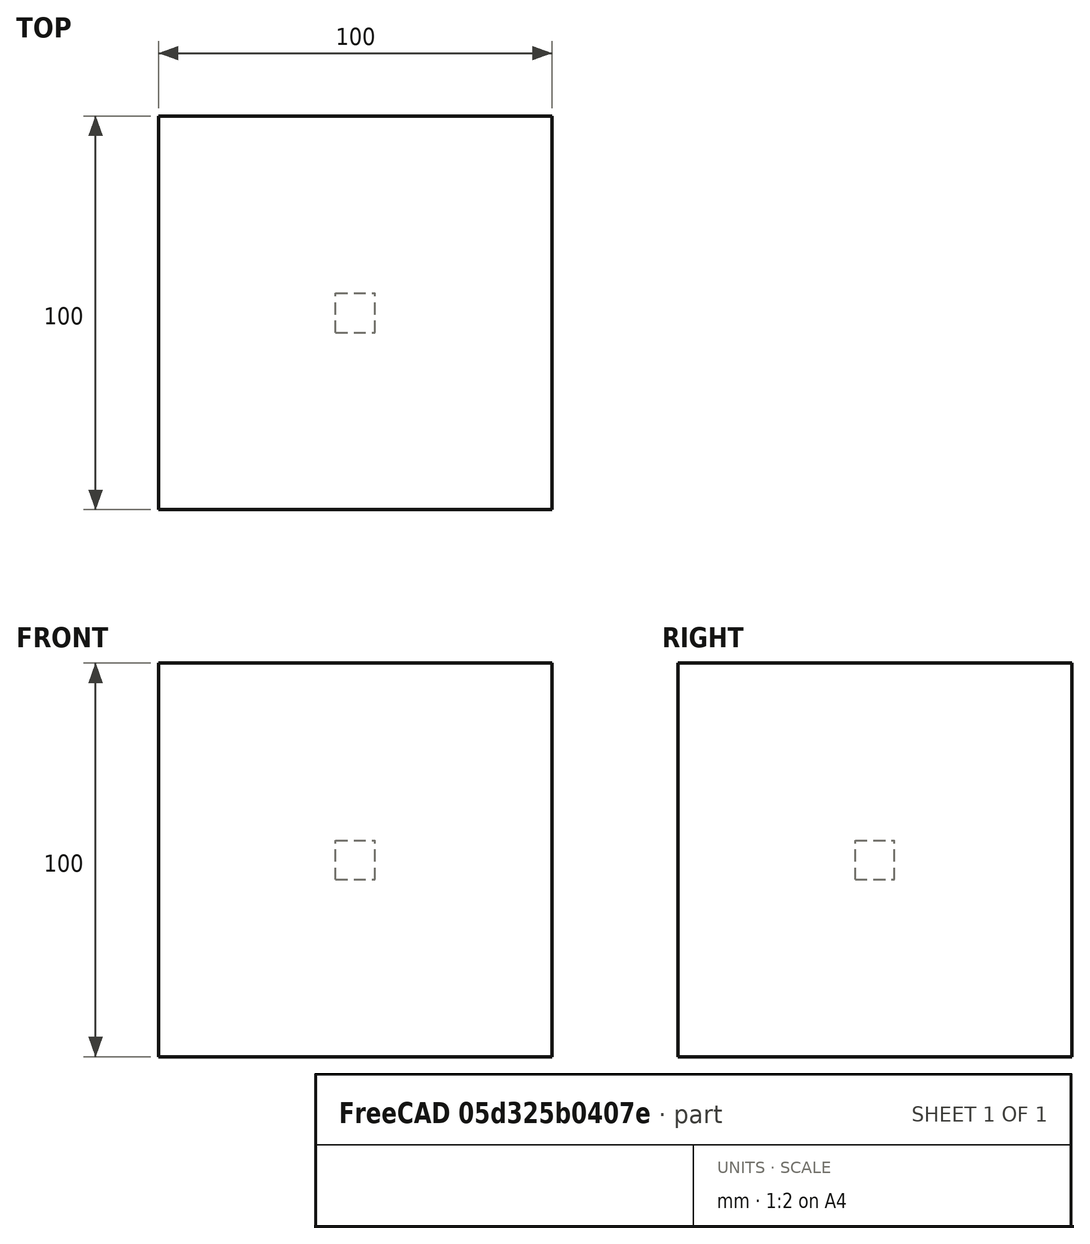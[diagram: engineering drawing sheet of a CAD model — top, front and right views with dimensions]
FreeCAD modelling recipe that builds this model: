
FCSTD DOCUMENT  (FreeCAD 0.20R29603 (Git))
Label: testCase2
License: All rights reserved
LicenseURL: http://en.wikipedia.org/wiki/All_rights_reserved
objects: App::DocumentObjectGroupPython×1251, Part::FeaturePython×3, App::Part×2
note: 2 computed .brp shape members not serialized (recipe doc carries the construction recipe); baked Part::Feature solids carry a one-line shape summary decoded from their .brp

FEATURE [App::DocumentObjectGroupPython] HALFPI  # scripted group (container) (typed FeaturePython)
  name = HALFPI
  value = pi/2.
FEATURE [App::DocumentObjectGroupPython] PI  # scripted group (container) (typed FeaturePython)
  name = PI
  value = 1.*pi
FEATURE [App::DocumentObjectGroupPython] TWOPI  # scripted group (container) (typed FeaturePython)
  name = TWOPI
  value = 2.*pi
FEATURE [App::DocumentObjectGroupPython] Constants  # scripted group (container) (typed FeaturePython)
  Group = -> [HALFPI,PI,TWOPI]
FEATURE [App::DocumentObjectGroupPython] Variables  # scripted group (container) (typed FeaturePython)
FEATURE [App::DocumentObjectGroupPython] Quantities  # scripted group (container) (typed FeaturePython)
FEATURE [App::DocumentObjectGroupPython] Isotopes  # scripted group (container) (typed FeaturePython)
FEATURE [App::DocumentObjectGroupPython] Elements  # scripted group (container) (typed FeaturePython)
FEATURE [App::DocumentObjectGroupPython] Matrix  # scripted group (container) (typed FeaturePython)
FEATURE [App::DocumentObjectGroupPython] Surfaces  # scripted group (container) (typed FeaturePython)
FEATURE [App::DocumentObjectGroupPython] Opticals  # scripted group (container) (typed FeaturePython)
  Group = -> [Matrix,Surfaces]
FEATURE [App::DocumentObjectGroupPython] G4Isotopes  # scripted group (container) (typed FeaturePython)
FEATURE [App::DocumentObjectGroupPython] H_element  # scripted group (container) (typed FeaturePython)
  Z = 1
  atom_value = 1.008
  formula = H
  name = H_element
FEATURE [App::DocumentObjectGroupPython] He_element  # scripted group (container) (typed FeaturePython)
  Z = 2
  atom_value = 4.0026
  formula = He
  name = He_element
FEATURE [App::DocumentObjectGroupPython] Li_element  # scripted group (container) (typed FeaturePython)
  Z = 3
  atom_value = 6.94
  formula = Li
  name = Li_element
FEATURE [App::DocumentObjectGroupPython] Be_element  # scripted group (container) (typed FeaturePython)
  Z = 4
  atom_value = 9.01218
  formula = Be
  name = Be_element
FEATURE [App::DocumentObjectGroupPython] B_element  # scripted group (container) (typed FeaturePython)
  Z = 5
  atom_value = 10.81
  formula = B
  name = B_element
FEATURE [App::DocumentObjectGroupPython] C_element  # scripted group (container) (typed FeaturePython)
  Z = 6
  atom_value = 12.011
  formula = C
  name = C_element
FEATURE [App::DocumentObjectGroupPython] N_element  # scripted group (container) (typed FeaturePython)
  Z = 7
  atom_value = 14.007
  formula = N
  name = N_element
FEATURE [App::DocumentObjectGroupPython] O_element  # scripted group (container) (typed FeaturePython)
  Z = 8
  atom_value = 15.999
  formula = O
  name = O_element
FEATURE [App::DocumentObjectGroupPython] F_element  # scripted group (container) (typed FeaturePython)
  Z = 9
  atom_value = 18.9984
  formula = F
  name = F_element
FEATURE [App::DocumentObjectGroupPython] Ne_element  # scripted group (container) (typed FeaturePython)
  Z = 10
  atom_value = 20.1797
  formula = Ne
  name = Ne_element
FEATURE [App::DocumentObjectGroupPython] Na_element  # scripted group (container) (typed FeaturePython)
  Z = 11
  atom_value = 22.9898
  formula = Na
  name = Na_element
FEATURE [App::DocumentObjectGroupPython] Mg_element  # scripted group (container) (typed FeaturePython)
  Z = 12
  atom_value = 24.305
  formula = Mg
  name = Mg_element
FEATURE [App::DocumentObjectGroupPython] Al_element  # scripted group (container) (typed FeaturePython)
  Z = 13
  atom_value = 26.9815
  formula = Al
  name = Al_element
FEATURE [App::DocumentObjectGroupPython] Si_element  # scripted group (container) (typed FeaturePython)
  Z = 14
  atom_value = 28.085
  formula = Si
  name = Si_element
FEATURE [App::DocumentObjectGroupPython] P_element  # scripted group (container) (typed FeaturePython)
  Z = 15
  atom_value = 30.9738
  formula = P
  name = P_element
FEATURE [App::DocumentObjectGroupPython] S_element  # scripted group (container) (typed FeaturePython)
  Z = 16
  atom_value = 32.06
  formula = S
  name = S_element
FEATURE [App::DocumentObjectGroupPython] Cl_element  # scripted group (container) (typed FeaturePython)
  Z = 17
  atom_value = 35.45
  formula = Cl
  name = Cl_element
FEATURE [App::DocumentObjectGroupPython] Ar_element  # scripted group (container) (typed FeaturePython)
  Z = 18
  atom_value = 39.95
  formula = Ar
  name = Ar_element
FEATURE [App::DocumentObjectGroupPython] K_element  # scripted group (container) (typed FeaturePython)
  Z = 19
  atom_value = 39.0983
  formula = K
  name = K_element
FEATURE [App::DocumentObjectGroupPython] Ca_element  # scripted group (container) (typed FeaturePython)
  Z = 20
  atom_value = 40.078
  formula = Ca
  name = Ca_element
FEATURE [App::DocumentObjectGroupPython] Sc_element  # scripted group (container) (typed FeaturePython)
  Z = 21
  atom_value = 44.9559
  formula = Sc
  name = Sc_element
FEATURE [App::DocumentObjectGroupPython] Ti_element  # scripted group (container) (typed FeaturePython)
  Z = 22
  atom_value = 47.867
  formula = Ti
  name = Ti_element
FEATURE [App::DocumentObjectGroupPython] V_element  # scripted group (container) (typed FeaturePython)
  Z = 23
  atom_value = 50.9415
  formula = V
  name = V_element
FEATURE [App::DocumentObjectGroupPython] Cr_element  # scripted group (container) (typed FeaturePython)
  Z = 24
  atom_value = 51.9961
  formula = Cr
  name = Cr_element
FEATURE [App::DocumentObjectGroupPython] Mn_element  # scripted group (container) (typed FeaturePython)
  Z = 25
  atom_value = 54.938
  formula = Mn
  name = Mn_element
FEATURE [App::DocumentObjectGroupPython] Fe_element  # scripted group (container) (typed FeaturePython)
  Z = 26
  atom_value = 55.845
  formula = Fe
  name = Fe_element
FEATURE [App::DocumentObjectGroupPython] Co_element  # scripted group (container) (typed FeaturePython)
  Z = 27
  atom_value = 58.9332
  formula = Co
  name = Co_element
FEATURE [App::DocumentObjectGroupPython] Ni_element  # scripted group (container) (typed FeaturePython)
  Z = 28
  atom_value = 58.6934
  formula = Ni
  name = Ni_element
FEATURE [App::DocumentObjectGroupPython] Cu_element  # scripted group (container) (typed FeaturePython)
  Z = 29
  atom_value = 63.546
  formula = Cu
  name = Cu_element
FEATURE [App::DocumentObjectGroupPython] Zn_element  # scripted group (container) (typed FeaturePython)
  Z = 30
  atom_value = 65.38
  formula = Zn
  name = Zn_element
FEATURE [App::DocumentObjectGroupPython] Ga_element  # scripted group (container) (typed FeaturePython)
  Z = 31
  atom_value = 69.723
  formula = Ga
  name = Ga_element
FEATURE [App::DocumentObjectGroupPython] Ge_element  # scripted group (container) (typed FeaturePython)
  Z = 32
  atom_value = 72.63
  formula = Ge
  name = Ge_element
FEATURE [App::DocumentObjectGroupPython] As_element  # scripted group (container) (typed FeaturePython)
  Z = 33
  atom_value = 74.9216
  formula = As
  name = As_element
FEATURE [App::DocumentObjectGroupPython] Se_element  # scripted group (container) (typed FeaturePython)
  Z = 34
  atom_value = 78.971
  formula = Se
  name = Se_element
FEATURE [App::DocumentObjectGroupPython] Br_element  # scripted group (container) (typed FeaturePython)
  Z = 35
  atom_value = 79.904
  formula = Br
  name = Br_element
FEATURE [App::DocumentObjectGroupPython] Kr_element  # scripted group (container) (typed FeaturePython)
  Z = 36
  atom_value = 83.798
  formula = Kr
  name = Kr_element
FEATURE [App::DocumentObjectGroupPython] Rb_element  # scripted group (container) (typed FeaturePython)
  Z = 37
  atom_value = 85.4678
  formula = Rb
  name = Rb_element
FEATURE [App::DocumentObjectGroupPython] Sr_element  # scripted group (container) (typed FeaturePython)
  Z = 38
  atom_value = 87.62
  formula = Sr
  name = Sr_element
FEATURE [App::DocumentObjectGroupPython] Y_element  # scripted group (container) (typed FeaturePython)
  Z = 39
  atom_value = 88.9058
  formula = Y
  name = Y_element
FEATURE [App::DocumentObjectGroupPython] Zr_element  # scripted group (container) (typed FeaturePython)
  Z = 40
  atom_value = 91.224
  formula = Zr
  name = Zr_element
FEATURE [App::DocumentObjectGroupPython] Nb_element  # scripted group (container) (typed FeaturePython)
  Z = 41
  atom_value = 92.9064
  formula = Nb
  name = Nb_element
FEATURE [App::DocumentObjectGroupPython] Mo_element  # scripted group (container) (typed FeaturePython)
  Z = 42
  atom_value = 95.95
  formula = Mo
  name = Mo_element
FEATURE [App::DocumentObjectGroupPython] Tc_element  # scripted group (container) (typed FeaturePython)
  Z = 43
  atom_value = 97
  formula = Tc
  name = Tc_element
FEATURE [App::DocumentObjectGroupPython] Ru_element  # scripted group (container) (typed FeaturePython)
  Z = 44
  atom_value = 101.07
  formula = Ru
  name = Ru_element
FEATURE [App::DocumentObjectGroupPython] Rh_element  # scripted group (container) (typed FeaturePython)
  Z = 45
  atom_value = 102.905
  formula = Rh
  name = Rh_element
FEATURE [App::DocumentObjectGroupPython] Pd_element  # scripted group (container) (typed FeaturePython)
  Z = 46
  atom_value = 106.42
  formula = Pd
  name = Pd_element
FEATURE [App::DocumentObjectGroupPython] Ag_element  # scripted group (container) (typed FeaturePython)
  Z = 47
  atom_value = 107.868
  formula = Ag
  name = Ag_element
FEATURE [App::DocumentObjectGroupPython] Cd_element  # scripted group (container) (typed FeaturePython)
  Z = 48
  atom_value = 112.414
  formula = Cd
  name = Cd_element
FEATURE [App::DocumentObjectGroupPython] In_element  # scripted group (container) (typed FeaturePython)
  Z = 49
  atom_value = 114.818
  formula = In
  name = In_element
FEATURE [App::DocumentObjectGroupPython] Sn_element  # scripted group (container) (typed FeaturePython)
  Z = 50
  atom_value = 118.71
  formula = Sn
  name = Sn_element
FEATURE [App::DocumentObjectGroupPython] Sb_element  # scripted group (container) (typed FeaturePython)
  Z = 51
  atom_value = 121.76
  formula = Sb
  name = Sb_element
FEATURE [App::DocumentObjectGroupPython] Te_element  # scripted group (container) (typed FeaturePython)
  Z = 52
  atom_value = 127.6
  formula = Te
  name = Te_element
FEATURE [App::DocumentObjectGroupPython] I_element  # scripted group (container) (typed FeaturePython)
  Z = 53
  atom_value = 126.904
  formula = I
  name = I_element
FEATURE [App::DocumentObjectGroupPython] Xe_element  # scripted group (container) (typed FeaturePython)
  Z = 54
  atom_value = 131.293
  formula = Xe
  name = Xe_element
FEATURE [App::DocumentObjectGroupPython] Cs_element  # scripted group (container) (typed FeaturePython)
  Z = 55
  atom_value = 132.905
  formula = Cs
  name = Cs_element
FEATURE [App::DocumentObjectGroupPython] Ba_element  # scripted group (container) (typed FeaturePython)
  Z = 56
  atom_value = 137.327
  formula = Ba
  name = Ba_element
FEATURE [App::DocumentObjectGroupPython] La_element  # scripted group (container) (typed FeaturePython)
  Z = 57
  atom_value = 138.905
  formula = La
  name = La_element
FEATURE [App::DocumentObjectGroupPython] Ce_element  # scripted group (container) (typed FeaturePython)
  Z = 58
  atom_value = 140.116
  formula = Ce
  name = Ce_element
FEATURE [App::DocumentObjectGroupPython] Pr_element  # scripted group (container) (typed FeaturePython)
  Z = 59
  atom_value = 140.908
  formula = Pr
  name = Pr_element
FEATURE [App::DocumentObjectGroupPython] Nd_element  # scripted group (container) (typed FeaturePython)
  Z = 60
  atom_value = 144.242
  formula = Nd
  name = Nd_element
FEATURE [App::DocumentObjectGroupPython] Pm_element  # scripted group (container) (typed FeaturePython)
  Z = 61
  atom_value = 145
  formula = Pm
  name = Pm_element
FEATURE [App::DocumentObjectGroupPython] Sm_element  # scripted group (container) (typed FeaturePython)
  Z = 62
  atom_value = 150.36
  formula = Sm
  name = Sm_element
FEATURE [App::DocumentObjectGroupPython] Eu_element  # scripted group (container) (typed FeaturePython)
  Z = 63
  atom_value = 151.964
  formula = Eu
  name = Eu_element
FEATURE [App::DocumentObjectGroupPython] Gd_element  # scripted group (container) (typed FeaturePython)
  Z = 64
  atom_value = 157.25
  formula = Gd
  name = Gd_element
FEATURE [App::DocumentObjectGroupPython] Tb_element  # scripted group (container) (typed FeaturePython)
  Z = 65
  atom_value = 158.925
  formula = Tb
  name = Tb_element
FEATURE [App::DocumentObjectGroupPython] Dy_element  # scripted group (container) (typed FeaturePython)
  Z = 66
  atom_value = 162.5
  formula = Dy
  name = Dy_element
FEATURE [App::DocumentObjectGroupPython] Ho_element  # scripted group (container) (typed FeaturePython)
  Z = 67
  atom_value = 164.93
  formula = Ho
  name = Ho_element
FEATURE [App::DocumentObjectGroupPython] Er_element  # scripted group (container) (typed FeaturePython)
  Z = 68
  atom_value = 167.259
  formula = Er
  name = Er_element
FEATURE [App::DocumentObjectGroupPython] Tm_element  # scripted group (container) (typed FeaturePython)
  Z = 69
  atom_value = 168.934
  formula = Tm
  name = Tm_element
FEATURE [App::DocumentObjectGroupPython] Yb_element  # scripted group (container) (typed FeaturePython)
  Z = 70
  atom_value = 173.045
  formula = Yb
  name = Yb_element
FEATURE [App::DocumentObjectGroupPython] Lu_element  # scripted group (container) (typed FeaturePython)
  Z = 71
  atom_value = 174.967
  formula = Lu
  name = Lu_element
FEATURE [App::DocumentObjectGroupPython] Hf_element  # scripted group (container) (typed FeaturePython)
  Z = 72
  atom_value = 178.49
  formula = Hf
  name = Hf_element
FEATURE [App::DocumentObjectGroupPython] Ta_element  # scripted group (container) (typed FeaturePython)
  Z = 73
  atom_value = 180.948
  formula = Ta
  name = Ta_element
FEATURE [App::DocumentObjectGroupPython] W_element  # scripted group (container) (typed FeaturePython)
  Z = 74
  atom_value = 183.84
  formula = W
  name = W_element
FEATURE [App::DocumentObjectGroupPython] Re_element  # scripted group (container) (typed FeaturePython)
  Z = 75
  atom_value = 186.207
  formula = Re
  name = Re_element
FEATURE [App::DocumentObjectGroupPython] Os_element  # scripted group (container) (typed FeaturePython)
  Z = 76
  atom_value = 190.23
  formula = Os
  name = Os_element
FEATURE [App::DocumentObjectGroupPython] Ir_element  # scripted group (container) (typed FeaturePython)
  Z = 77
  atom_value = 192.217
  formula = Ir
  name = Ir_element
FEATURE [App::DocumentObjectGroupPython] Pt_element  # scripted group (container) (typed FeaturePython)
  Z = 78
  atom_value = 195.084
  formula = Pt
  name = Pt_element
FEATURE [App::DocumentObjectGroupPython] Au_element  # scripted group (container) (typed FeaturePython)
  Z = 79
  atom_value = 196.967
  formula = Au
  name = Au_element
FEATURE [App::DocumentObjectGroupPython] Hg_element  # scripted group (container) (typed FeaturePython)
  Z = 80
  atom_value = 200.592
  formula = Hg
  name = Hg_element
FEATURE [App::DocumentObjectGroupPython] Tl_element  # scripted group (container) (typed FeaturePython)
  Z = 81
  atom_value = 204.38
  formula = Tl
  name = Tl_element
FEATURE [App::DocumentObjectGroupPython] Pb_element  # scripted group (container) (typed FeaturePython)
  Z = 82
  atom_value = 207.2
  formula = Pb
  name = Pb_element
FEATURE [App::DocumentObjectGroupPython] Bi_element  # scripted group (container) (typed FeaturePython)
  Z = 83
  atom_value = 208.98
  formula = Bi
  name = Bi_element
FEATURE [App::DocumentObjectGroupPython] Po_element  # scripted group (container) (typed FeaturePython)
  Z = 84
  atom_value = 209
  formula = Po
  name = Po_element
FEATURE [App::DocumentObjectGroupPython] At_element  # scripted group (container) (typed FeaturePython)
  Z = 85
  atom_value = 210
  formula = At
  name = At_element
FEATURE [App::DocumentObjectGroupPython] Rn_element  # scripted group (container) (typed FeaturePython)
  Z = 86
  atom_value = 222
  formula = Rn
  name = Rn_element
FEATURE [App::DocumentObjectGroupPython] Fr_element  # scripted group (container) (typed FeaturePython)
  Z = 87
  atom_value = 223
  formula = Fr
  name = Fr_element
FEATURE [App::DocumentObjectGroupPython] Ra_element  # scripted group (container) (typed FeaturePython)
  Z = 88
  atom_value = 226
  formula = Ra
  name = Ra_element
FEATURE [App::DocumentObjectGroupPython] Ac_element  # scripted group (container) (typed FeaturePython)
  Z = 89
  atom_value = 227
  formula = Ac
  name = Ac_element
FEATURE [App::DocumentObjectGroupPython] Th_element  # scripted group (container) (typed FeaturePython)
  Z = 90
  atom_value = 232.038
  formula = Th
  name = Th_element
FEATURE [App::DocumentObjectGroupPython] Pa_element  # scripted group (container) (typed FeaturePython)
  Z = 91
  atom_value = 231.036
  formula = Pa
  name = Pa_element
FEATURE [App::DocumentObjectGroupPython] U_element  # scripted group (container) (typed FeaturePython)
  Z = 92
  atom_value = 238.029
  formula = U
  name = U_element
FEATURE [App::DocumentObjectGroupPython] Np_element  # scripted group (container) (typed FeaturePython)
  Z = 93
  atom_value = 237
  formula = Np
  name = Np_element
FEATURE [App::DocumentObjectGroupPython] Pu_element  # scripted group (container) (typed FeaturePython)
  Z = 94
  atom_value = 244
  formula = Pu
  name = Pu_element
FEATURE [App::DocumentObjectGroupPython] Am_element  # scripted group (container) (typed FeaturePython)
  Z = 95
  atom_value = 243
  formula = Am
  name = Am_element
FEATURE [App::DocumentObjectGroupPython] Cm_element  # scripted group (container) (typed FeaturePython)
  Z = 96
  atom_value = 247
  formula = Cm
  name = Cm_element
FEATURE [App::DocumentObjectGroupPython] Bk_element  # scripted group (container) (typed FeaturePython)
  Z = 97
  atom_value = 247
  formula = Bk
  name = Bk_element
FEATURE [App::DocumentObjectGroupPython] Cf_element  # scripted group (container) (typed FeaturePython)
  Z = 98
  atom_value = 251
  formula = Cf
  name = Cf_element
FEATURE [App::DocumentObjectGroupPython] G4Elements  # scripted group (container) (typed FeaturePython)
  Group = -> [H_element,He_element,Li_element,Be_element,B_element,C_element,N_element,O_element,F_element,Ne_element,Na_element,Mg_element,Al_element,Si_element,P_element,S_element,Cl_element,Ar_element,K_element,Ca_element,Sc_element,Ti_element,V_element,Cr_element,Mn_element,Fe_element,Co_element,Ni_element,Cu_element,Zn_element,Ga_element,Ge_element,As_element,Se_element,Br_element,Kr_element,Rb_element,+61 more]
FEATURE [App::DocumentObjectGroupPython] H_element001  label="H_element : 0.101"  # scripted group (container) (typed FeaturePython)
  n = 0.101327
FEATURE [App::DocumentObjectGroupPython] C_element001  label="C_element : 0.775"  # scripted group (container) (typed FeaturePython)
  n = 0.7755
FEATURE [App::DocumentObjectGroupPython] N_element001  label="N_element : 0.035"  # scripted group (container) (typed FeaturePython)
  n = 0.035057
FEATURE [App::DocumentObjectGroupPython] O_element001  label="O_element : 0.052"  # scripted group (container) (typed FeaturePython)
  n = 0.0523159
FEATURE [App::DocumentObjectGroupPython] F_element001  label="F_element : 0.017"  # scripted group (container) (typed FeaturePython)
  n = 0.017422
FEATURE [App::DocumentObjectGroupPython] Ca_element001  label="Ca_element : 0.018"  # scripted group (container) (typed FeaturePython)
  n = 0.018378
FEATURE [App::DocumentObjectGroupPython] G4_A_150_TISSUE  label="G4_A-150_TISSUE"  # scripted group (container) (typed FeaturePython)
  Dunit = g/cm3
  Dvalue = 1.127
  Group = -> [H_element001,C_element001,N_element001,O_element001,F_element001,Ca_element001]
  conduct = 2
  density = 1
  expand = 3
  formula = G4_A-150_TISSUE
  name = G4_A-150_TISSUE
  specific = 4
FEATURE [App::DocumentObjectGroupPython] C_element002  label="C_element : 3"  # scripted group (container) (typed FeaturePython)
  n = 3
  ref = C_element
FEATURE [App::DocumentObjectGroupPython] H_element002  label="H_element : 6"  # scripted group (container) (typed FeaturePython)
  n = 6
  ref = H_element
FEATURE [App::DocumentObjectGroupPython] O_element002  label="O_element : 1"  # scripted group (container) (typed FeaturePython)
  n = 1
  ref = O_element
FEATURE [App::DocumentObjectGroupPython] G4_ACETONE  # scripted group (container) (typed FeaturePython)
  Dunit = g/cm3
  Dvalue = 0.7899
  Group = -> [C_element002,H_element002,O_element002]
  conduct = 2
  density = 1
  expand = 3
  formula = G4_ACETONE
  name = G4_ACETONE
  specific = 4
FEATURE [App::DocumentObjectGroupPython] C_element003  label="C_element : 2"  # scripted group (container) (typed FeaturePython)
  n = 2
  ref = C_element
FEATURE [App::DocumentObjectGroupPython] H_element003  label="H_element : 2"  # scripted group (container) (typed FeaturePython)
  n = 2
  ref = H_element
FEATURE [App::DocumentObjectGroupPython] G4_ACETYLENE  # scripted group (container) (typed FeaturePython)
  Dunit = g/cm3
  Dvalue = 0.0010967
  Group = -> [C_element003,H_element003]
  conduct = 2
  density = 1
  expand = 3
  formula = G4_ACETYLENE
  name = G4_ACETYLENE
  specific = 4
FEATURE [App::DocumentObjectGroupPython] C_element004  label="C_element : 5"  # scripted group (container) (typed FeaturePython)
  n = 5
  ref = C_element
FEATURE [App::DocumentObjectGroupPython] H_element004  label="H_element : 5"  # scripted group (container) (typed FeaturePython)
  n = 5
  ref = H_element
FEATURE [App::DocumentObjectGroupPython] N_element002  label="N_element : 5"  # scripted group (container) (typed FeaturePython)
  n = 5
  ref = N_element
FEATURE [App::DocumentObjectGroupPython] G4_ADENINE  # scripted group (container) (typed FeaturePython)
  Dunit = g/cm3
  Dvalue = 1.6
  Group = -> [C_element004,H_element004,N_element002]
  conduct = 2
  density = 1
  expand = 3
  formula = G4_ADENINE
  name = G4_ADENINE
  specific = 4
FEATURE [App::DocumentObjectGroupPython] H_element005  label="H_element : 0.114"  # scripted group (container) (typed FeaturePython)
  n = 0.114
FEATURE [App::DocumentObjectGroupPython] C_element005  label="C_element : 0.598"  # scripted group (container) (typed FeaturePython)
  n = 0.598
FEATURE [App::DocumentObjectGroupPython] N_element003  label="N_element : 0.007"  # scripted group (container) (typed FeaturePython)
  n = 0.007
FEATURE [App::DocumentObjectGroupPython] O_element003  label="O_element : 0.278"  # scripted group (container) (typed FeaturePython)
  n = 0.278
FEATURE [App::DocumentObjectGroupPython] Na_element001  label="Na_element : 0.001"  # scripted group (container) (typed FeaturePython)
  n = 0.001
FEATURE [App::DocumentObjectGroupPython] S_element001  label="S_element : 0.001"  # scripted group (container) (typed FeaturePython)
  n = 0.001
FEATURE [App::DocumentObjectGroupPython] Cl_element001  label="Cl_element : 0.001"  # scripted group (container) (typed FeaturePython)
  n = 0.001
FEATURE [App::DocumentObjectGroupPython] G4_ADIPOSE_TISSUE_ICRP  # scripted group (container) (typed FeaturePython)
  Dunit = g/cm3
  Dvalue = 0.95
  Group = -> [H_element005,C_element005,N_element003,O_element003,Na_element001,S_element001,Cl_element001]
  conduct = 2
  density = 1
  expand = 3
  formula = G4_ADIPOSE_TISSUE_ICRP
  name = G4_ADIPOSE_TISSUE_ICRP
  specific = 4
FEATURE [App::DocumentObjectGroupPython] C_element006  label="C_element : 0.000"  # scripted group (container) (typed FeaturePython)
  n = 0.000124
FEATURE [App::DocumentObjectGroupPython] N_element004  label="N_element : 0.755"  # scripted group (container) (typed FeaturePython)
  n = 0.755268
FEATURE [App::DocumentObjectGroupPython] O_element004  label="O_element : 0.232"  # scripted group (container) (typed FeaturePython)
  n = 0.231781
FEATURE [App::DocumentObjectGroupPython] Ar_element001  label="Ar_element : 0.013"  # scripted group (container) (typed FeaturePython)
  n = 0.012827
FEATURE [App::DocumentObjectGroupPython] G4_AIR  # scripted group (container) (typed FeaturePython)
  Dunit = g/cm3
  Dvalue = 0.00120479
  Group = -> [C_element006,N_element004,O_element004,Ar_element001]
  conduct = 2
  density = 1
  expand = 3
  formula = G4_AIR
  name = G4_AIR
  specific = 4
FEATURE [App::DocumentObjectGroupPython] C_element007  label="C_element : 006"  # scripted group (container) (typed FeaturePython)
  n = 3
  ref = C_element
FEATURE [App::DocumentObjectGroupPython] H_element006  label="H_element : 7"  # scripted group (container) (typed FeaturePython)
  n = 7
  ref = H_element
FEATURE [App::DocumentObjectGroupPython] N_element005  label="N_element : 1"  # scripted group (container) (typed FeaturePython)
  n = 1
  ref = N_element
FEATURE [App::DocumentObjectGroupPython] O_element005  label="O_element : 2"  # scripted group (container) (typed FeaturePython)
  n = 2
  ref = O_element
FEATURE [App::DocumentObjectGroupPython] G4_ALANINE  # scripted group (container) (typed FeaturePython)
  Dunit = g/cm3
  Dvalue = 1.42
  Group = -> [C_element007,H_element006,N_element005,O_element005]
  conduct = 2
  density = 1
  expand = 3
  formula = G4_ALANINE
  name = G4_ALANINE
  specific = 4
FEATURE [App::DocumentObjectGroupPython] Al_element001  label="Al_element : 2"  # scripted group (container) (typed FeaturePython)
  n = 2
  ref = Al_element
FEATURE [App::DocumentObjectGroupPython] O_element006  label="O_element : 3"  # scripted group (container) (typed FeaturePython)
  n = 3
  ref = O_element
FEATURE [App::DocumentObjectGroupPython] G4_ALUMINUM_OXIDE  # scripted group (container) (typed FeaturePython)
  Dunit = g/cm3
  Dvalue = 3.97
  Group = -> [Al_element001,O_element006]
  conduct = 2
  density = 1
  expand = 3
  formula = G4_ALUMINUM_OXIDE
  name = G4_ALUMINUM_OXIDE
  specific = 4
FEATURE [App::DocumentObjectGroupPython] H_element007  label="H_element : 0.106"  # scripted group (container) (typed FeaturePython)
  n = 0.10593
FEATURE [App::DocumentObjectGroupPython] C_element008  label="C_element : 0.789"  # scripted group (container) (typed FeaturePython)
  n = 0.788974
FEATURE [App::DocumentObjectGroupPython] O_element007  label="O_element : 0.105"  # scripted group (container) (typed FeaturePython)
  n = 0.105096
FEATURE [App::DocumentObjectGroupPython] G4_AMBER  # scripted group (container) (typed FeaturePython)
  Dunit = g/cm3
  Dvalue = 1.1
  Group = -> [H_element007,C_element008,O_element007]
  conduct = 2
  density = 1
  expand = 3
  formula = G4_AMBER
  name = G4_AMBER
  specific = 4
FEATURE [App::DocumentObjectGroupPython] N_element006  label="N_element : 006"  # scripted group (container) (typed FeaturePython)
  n = 1
  ref = N_element
FEATURE [App::DocumentObjectGroupPython] H_element008  label="H_element : 3"  # scripted group (container) (typed FeaturePython)
  n = 3
  ref = H_element
FEATURE [App::DocumentObjectGroupPython] G4_AMMONIA  # scripted group (container) (typed FeaturePython)
  Dunit = g/cm3
  Dvalue = 0.000826019
  Group = -> [N_element006,H_element008]
  conduct = 2
  density = 1
  expand = 3
  formula = G4_AMMONIA
  name = G4_AMMONIA
  specific = 4
FEATURE [App::DocumentObjectGroupPython] C_element009  label="C_element : 6"  # scripted group (container) (typed FeaturePython)
  n = 6
  ref = C_element
FEATURE [App::DocumentObjectGroupPython] H_element009  label="H_element : 008"  # scripted group (container) (typed FeaturePython)
  n = 7
  ref = H_element
FEATURE [App::DocumentObjectGroupPython] N_element007  label="N_element : 007"  # scripted group (container) (typed FeaturePython)
  n = 1
  ref = N_element
FEATURE [App::DocumentObjectGroupPython] G4_ANILINE  # scripted group (container) (typed FeaturePython)
  Dunit = g/cm3
  Dvalue = 1.0235
  Group = -> [C_element009,H_element009,N_element007]
  conduct = 2
  density = 1
  expand = 3
  formula = G4_ANILINE
  name = G4_ANILINE
  specific = 4
FEATURE [App::DocumentObjectGroupPython] C_element010  label="C_element : 14"  # scripted group (container) (typed FeaturePython)
  n = 14
  ref = C_element
FEATURE [App::DocumentObjectGroupPython] H_element010  label="H_element : 10"  # scripted group (container) (typed FeaturePython)
  n = 10
  ref = H_element
FEATURE [App::DocumentObjectGroupPython] G4_ANTHRACENE  # scripted group (container) (typed FeaturePython)
  Dunit = g/cm3
  Dvalue = 1.283
  Group = -> [C_element010,H_element010]
  conduct = 2
  density = 1
  expand = 3
  formula = G4_ANTHRACENE
  name = G4_ANTHRACENE
  specific = 4
FEATURE [App::DocumentObjectGroupPython] H_element011  label="H_element : 0.065"  # scripted group (container) (typed FeaturePython)
  n = 0.0654709
FEATURE [App::DocumentObjectGroupPython] C_element011  label="C_element : 0.537"  # scripted group (container) (typed FeaturePython)
  n = 0.536944
FEATURE [App::DocumentObjectGroupPython] N_element008  label="N_element : 0.021"  # scripted group (container) (typed FeaturePython)
  n = 0.0215
FEATURE [App::DocumentObjectGroupPython] O_element008  label="O_element : 0.032"  # scripted group (container) (typed FeaturePython)
  n = 0.032085
FEATURE [App::DocumentObjectGroupPython] F_element002  label="F_element : 0.167"  # scripted group (container) (typed FeaturePython)
  n = 0.167411
FEATURE [App::DocumentObjectGroupPython] Ca_element002  label="Ca_element : 0.177"  # scripted group (container) (typed FeaturePython)
  n = 0.176589
FEATURE [App::DocumentObjectGroupPython] G4_B_100_BONE  label="G4_B-100_BONE"  # scripted group (container) (typed FeaturePython)
  Dunit = g/cm3
  Dvalue = 1.45
  Group = -> [H_element011,C_element011,N_element008,O_element008,F_element002,Ca_element002]
  conduct = 2
  density = 1
  expand = 3
  formula = G4_B-100_BONE
  name = G4_B-100_BONE
  specific = 4
FEATURE [App::DocumentObjectGroupPython] H_element012  label="H_element : 0.057"  # scripted group (container) (typed FeaturePython)
  n = 0.057441
FEATURE [App::DocumentObjectGroupPython] C_element012  label="C_element : 0.790"  # scripted group (container) (typed FeaturePython)
  n = 0.774591
FEATURE [App::DocumentObjectGroupPython] O_element009  label="O_element : 0.168"  # scripted group (container) (typed FeaturePython)
  n = 0.167968
FEATURE [App::DocumentObjectGroupPython] G4_BAKELITE  # scripted group (container) (typed FeaturePython)
  Dunit = g/cm3
  Dvalue = 1.25
  Group = -> [H_element012,C_element012,O_element009]
  conduct = 2
  density = 1
  expand = 3
  formula = G4_BAKELITE
  name = G4_BAKELITE
  specific = 4
FEATURE [App::DocumentObjectGroupPython] Ba_element001  label="Ba_element : 1"  # scripted group (container) (typed FeaturePython)
  n = 1
  ref = Ba_element
FEATURE [App::DocumentObjectGroupPython] F_element003  label="F_element : 2"  # scripted group (container) (typed FeaturePython)
  n = 2
  ref = F_element
FEATURE [App::DocumentObjectGroupPython] G4_BARIUM_FLUORIDE  # scripted group (container) (typed FeaturePython)
  Dunit = g/cm3
  Dvalue = 4.89
  Group = -> [Ba_element001,F_element003]
  conduct = 2
  density = 1
  expand = 3
  formula = G4_BARIUM_FLUORIDE
  name = G4_BARIUM_FLUORIDE
  specific = 4
FEATURE [App::DocumentObjectGroupPython] Ba_element002  label="Ba_element : 002"  # scripted group (container) (typed FeaturePython)
  n = 1
  ref = Ba_element
FEATURE [App::DocumentObjectGroupPython] S_element002  label="S_element : 1"  # scripted group (container) (typed FeaturePython)
  n = 1
  ref = S_element
FEATURE [App::DocumentObjectGroupPython] O_element010  label="O_element : 4"  # scripted group (container) (typed FeaturePython)
  n = 4
  ref = O_element
FEATURE [App::DocumentObjectGroupPython] G4_BARIUM_SULFATE  # scripted group (container) (typed FeaturePython)
  Dunit = g/cm3
  Dvalue = 4.5
  Group = -> [Ba_element002,S_element002,O_element010]
  conduct = 2
  density = 1
  expand = 3
  formula = G4_BARIUM_SULFATE
  name = G4_BARIUM_SULFATE
  specific = 4
FEATURE [App::DocumentObjectGroupPython] C_element013  label="C_element : 007"  # scripted group (container) (typed FeaturePython)
  n = 6
  ref = C_element
FEATURE [App::DocumentObjectGroupPython] H_element013  label="H_element : 009"  # scripted group (container) (typed FeaturePython)
  n = 6
  ref = H_element
FEATURE [App::DocumentObjectGroupPython] G4_BENZENE  # scripted group (container) (typed FeaturePython)
  Dunit = g/cm3
  Dvalue = 0.87865
  Group = -> [C_element013,H_element013]
  conduct = 2
  density = 1
  expand = 3
  formula = G4_BENZENE
  name = G4_BENZENE
  specific = 4
FEATURE [App::DocumentObjectGroupPython] Be_element001  label="Be_element : 1"  # scripted group (container) (typed FeaturePython)
  n = 1
  ref = Be_element
FEATURE [App::DocumentObjectGroupPython] O_element011  label="O_element : 005"  # scripted group (container) (typed FeaturePython)
  n = 1
  ref = O_element
FEATURE [App::DocumentObjectGroupPython] G4_BERYLLIUM_OXIDE  # scripted group (container) (typed FeaturePython)
  Dunit = g/cm3
  Dvalue = 3.01
  Group = -> [Be_element001,O_element011]
  conduct = 2
  density = 1
  expand = 3
  formula = G4_BERYLLIUM_OXIDE
  name = G4_BERYLLIUM_OXIDE
  specific = 4
FEATURE [App::DocumentObjectGroupPython] Bi_element001  label="Bi_element : 4"  # scripted group (container) (typed FeaturePython)
  n = 4
  ref = Bi_element
FEATURE [App::DocumentObjectGroupPython] Ge_element001  label="Ge_element : 3"  # scripted group (container) (typed FeaturePython)
  n = 3
  ref = Ge_element
FEATURE [App::DocumentObjectGroupPython] O_element012  label="O_element : 12"  # scripted group (container) (typed FeaturePython)
  n = 12
  ref = O_element
FEATURE [App::DocumentObjectGroupPython] G4_BGO  # scripted group (container) (typed FeaturePython)
  Dunit = g/cm3
  Dvalue = 7.13
  Group = -> [Bi_element001,Ge_element001,O_element012]
  conduct = 2
  density = 1
  expand = 3
  formula = G4_BGO
  name = G4_BGO
  specific = 4
FEATURE [App::DocumentObjectGroupPython] H_element014  label="H_element : 0.102"  # scripted group (container) (typed FeaturePython)
  n = 0.102
FEATURE [App::DocumentObjectGroupPython] C_element014  label="C_element : 0.110"  # scripted group (container) (typed FeaturePython)
  n = 0.11
FEATURE [App::DocumentObjectGroupPython] N_element009  label="N_element : 0.033"  # scripted group (container) (typed FeaturePython)
  n = 0.033
FEATURE [App::DocumentObjectGroupPython] O_element013  label="O_element : 0.745"  # scripted group (container) (typed FeaturePython)
  n = 0.745
FEATURE [App::DocumentObjectGroupPython] Na_element002  label="Na_element : 0.002"  # scripted group (container) (typed FeaturePython)
  n = 0.001
FEATURE [App::DocumentObjectGroupPython] P_element001  label="P_element : 0.001"  # scripted group (container) (typed FeaturePython)
  n = 0.001
FEATURE [App::DocumentObjectGroupPython] S_element003  label="S_element : 0.002"  # scripted group (container) (typed FeaturePython)
  n = 0.002
FEATURE [App::DocumentObjectGroupPython] Cl_element002  label="Cl_element : 0.003"  # scripted group (container) (typed FeaturePython)
  n = 0.003
FEATURE [App::DocumentObjectGroupPython] K_element001  label="K_element : 0.002"  # scripted group (container) (typed FeaturePython)
  n = 0.002
FEATURE [App::DocumentObjectGroupPython] Fe_element001  label="Fe_element : 0.001"  # scripted group (container) (typed FeaturePython)
  n = 0.001
FEATURE [App::DocumentObjectGroupPython] G4_BLOOD_ICRP  # scripted group (container) (typed FeaturePython)
  Dunit = g/cm3
  Dvalue = 1.06
  Group = -> [H_element014,C_element014,N_element009,O_element013,Na_element002,P_element001,S_element003,Cl_element002,K_element001,Fe_element001]
  conduct = 2
  density = 1
  expand = 3
  formula = G4_BLOOD_ICRP
  name = G4_BLOOD_ICRP
  specific = 4
FEATURE [App::DocumentObjectGroupPython] H_element015  label="H_element : 0.064"  # scripted group (container) (typed FeaturePython)
  n = 0.064
FEATURE [App::DocumentObjectGroupPython] C_element015  label="C_element : 0.278"  # scripted group (container) (typed FeaturePython)
  n = 0.278
FEATURE [App::DocumentObjectGroupPython] N_element010  label="N_element : 0.027"  # scripted group (container) (typed FeaturePython)
  n = 0.027
FEATURE [App::DocumentObjectGroupPython] O_element014  label="O_element : 0.410"  # scripted group (container) (typed FeaturePython)
  n = 0.41
FEATURE [App::DocumentObjectGroupPython] Mg_element001  label="Mg_element : 0.002"  # scripted group (container) (typed FeaturePython)
  n = 0.002
FEATURE [App::DocumentObjectGroupPython] P_element002  label="P_element : 0.070"  # scripted group (container) (typed FeaturePython)
  n = 0.07
FEATURE [App::DocumentObjectGroupPython] S_element004  label="S_element : 0.003"  # scripted group (container) (typed FeaturePython)
  n = 0.002
FEATURE [App::DocumentObjectGroupPython] Ca_element003  label="Ca_element : 0.147"  # scripted group (container) (typed FeaturePython)
  n = 0.147
FEATURE [App::DocumentObjectGroupPython] G4_BONE_COMPACT_ICRU  # scripted group (container) (typed FeaturePython)
  Dunit = g/cm3
  Dvalue = 1.85
  Group = -> [H_element015,C_element015,N_element010,O_element014,Mg_element001,P_element002,S_element004,Ca_element003]
  conduct = 2
  density = 1
  expand = 3
  formula = G4_BONE_COMPACT_ICRU
  name = G4_BONE_COMPACT_ICRU
  specific = 4
FEATURE [App::DocumentObjectGroupPython] H_element016  label="H_element : 0.034"  # scripted group (container) (typed FeaturePython)
  n = 0.034
FEATURE [App::DocumentObjectGroupPython] C_element016  label="C_element : 0.155"  # scripted group (container) (typed FeaturePython)
  n = 0.155
FEATURE [App::DocumentObjectGroupPython] N_element011  label="N_element : 0.042"  # scripted group (container) (typed FeaturePython)
  n = 0.042
FEATURE [App::DocumentObjectGroupPython] O_element015  label="O_element : 0.435"  # scripted group (container) (typed FeaturePython)
  n = 0.435
FEATURE [App::DocumentObjectGroupPython] Na_element003  label="Na_element : 0.003"  # scripted group (container) (typed FeaturePython)
  n = 0.001
FEATURE [App::DocumentObjectGroupPython] Mg_element002  label="Mg_element : 0.003"  # scripted group (container) (typed FeaturePython)
  n = 0.002
FEATURE [App::DocumentObjectGroupPython] P_element003  label="P_element : 0.103"  # scripted group (container) (typed FeaturePython)
  n = 0.103
FEATURE [App::DocumentObjectGroupPython] S_element005  label="S_element : 0.004"  # scripted group (container) (typed FeaturePython)
  n = 0.003
FEATURE [App::DocumentObjectGroupPython] Ca_element004  label="Ca_element : 0.225"  # scripted group (container) (typed FeaturePython)
  n = 0.225
FEATURE [App::DocumentObjectGroupPython] G4_BONE_CORTICAL_ICRP  # scripted group (container) (typed FeaturePython)
  Dunit = g/cm3
  Dvalue = 1.92
  Group = -> [H_element016,C_element016,N_element011,O_element015,Na_element003,Mg_element002,P_element003,S_element005,Ca_element004]
  conduct = 2
  density = 1
  expand = 3
  formula = G4_BONE_CORTICAL_ICRP
  name = G4_BONE_CORTICAL_ICRP
  specific = 4
FEATURE [App::DocumentObjectGroupPython] B_element001  label="B_element : 4"  # scripted group (container) (typed FeaturePython)
  n = 4
  ref = B_element
FEATURE [App::DocumentObjectGroupPython] C_element017  label="C_element : 1"  # scripted group (container) (typed FeaturePython)
  n = 1
  ref = C_element
FEATURE [App::DocumentObjectGroupPython] G4_BORON_CARBIDE  # scripted group (container) (typed FeaturePython)
  Dunit = g/cm3
  Dvalue = 2.52
  Group = -> [B_element001,C_element017]
  conduct = 2
  density = 1
  expand = 3
  formula = G4_BORON_CARBIDE
  name = G4_BORON_CARBIDE
  specific = 4
FEATURE [App::DocumentObjectGroupPython] B_element002  label="B_element : 2"  # scripted group (container) (typed FeaturePython)
  n = 2
  ref = B_element
FEATURE [App::DocumentObjectGroupPython] O_element016  label="O_element : 006"  # scripted group (container) (typed FeaturePython)
  n = 3
  ref = O_element
FEATURE [App::DocumentObjectGroupPython] G4_BORON_OXIDE  # scripted group (container) (typed FeaturePython)
  Dunit = g/cm3
  Dvalue = 1.812
  Group = -> [B_element002,O_element016]
  conduct = 2
  density = 1
  expand = 3
  formula = G4_BORON_OXIDE
  name = G4_BORON_OXIDE
  specific = 4
FEATURE [App::DocumentObjectGroupPython] H_element017  label="H_element : 0.107"  # scripted group (container) (typed FeaturePython)
  n = 0.107
FEATURE [App::DocumentObjectGroupPython] C_element018  label="C_element : 0.145"  # scripted group (container) (typed FeaturePython)
  n = 0.145
FEATURE [App::DocumentObjectGroupPython] N_element012  label="N_element : 0.022"  # scripted group (container) (typed FeaturePython)
  n = 0.022
FEATURE [App::DocumentObjectGroupPython] O_element017  label="O_element : 0.712"  # scripted group (container) (typed FeaturePython)
  n = 0.712
FEATURE [App::DocumentObjectGroupPython] Na_element004  label="Na_element : 0.004"  # scripted group (container) (typed FeaturePython)
  n = 0.002
FEATURE [App::DocumentObjectGroupPython] P_element004  label="P_element : 0.004"  # scripted group (container) (typed FeaturePython)
  n = 0.004
FEATURE [App::DocumentObjectGroupPython] S_element006  label="S_element : 0.005"  # scripted group (container) (typed FeaturePython)
  n = 0.002
FEATURE [App::DocumentObjectGroupPython] Cl_element003  label="Cl_element : 0.004"  # scripted group (container) (typed FeaturePython)
  n = 0.003
FEATURE [App::DocumentObjectGroupPython] K_element002  label="K_element : 0.003"  # scripted group (container) (typed FeaturePython)
  n = 0.003
FEATURE [App::DocumentObjectGroupPython] G4_BRAIN_ICRP  # scripted group (container) (typed FeaturePython)
  Dunit = g/cm3
  Dvalue = 1.04
  Group = -> [H_element017,C_element018,N_element012,O_element017,Na_element004,P_element004,S_element006,Cl_element003,K_element002]
  conduct = 2
  density = 1
  expand = 3
  formula = G4_BRAIN_ICRP
  name = G4_BRAIN_ICRP
  specific = 4
FEATURE [App::DocumentObjectGroupPython] C_element019  label="C_element : 4"  # scripted group (container) (typed FeaturePython)
  n = 4
  ref = C_element
FEATURE [App::DocumentObjectGroupPython] H_element018  label="H_element : 010"  # scripted group (container) (typed FeaturePython)
  n = 10
  ref = H_element
FEATURE [App::DocumentObjectGroupPython] G4_BUTANE  # scripted group (container) (typed FeaturePython)
  Dunit = g/cm3
  Dvalue = 0.00249343
  Group = -> [C_element019,H_element018]
  conduct = 2
  density = 1
  expand = 3
  formula = G4_BUTANE
  name = G4_BUTANE
  specific = 4
FEATURE [App::DocumentObjectGroupPython] C_element020  label="C_element : 008"  # scripted group (container) (typed FeaturePython)
  n = 4
  ref = C_element
FEATURE [App::DocumentObjectGroupPython] H_element019  label="H_element : 011"  # scripted group (container) (typed FeaturePython)
  n = 10
  ref = H_element
FEATURE [App::DocumentObjectGroupPython] O_element018  label="O_element : 007"  # scripted group (container) (typed FeaturePython)
  n = 1
  ref = O_element
FEATURE [App::DocumentObjectGroupPython] G4_N_BUTYL_ALCOHOL  label="G4_N-BUTYL_ALCOHOL"  # scripted group (container) (typed FeaturePython)
  Dunit = g/cm3
  Dvalue = 0.8098
  Group = -> [C_element020,H_element019,O_element018]
  conduct = 2
  density = 1
  expand = 3
  formula = G4_N-BUTYL_ALCOHOL
  name = G4_N-BUTYL_ALCOHOL
  specific = 4
FEATURE [App::DocumentObjectGroupPython] H_element020  label="H_element : 0.025"  # scripted group (container) (typed FeaturePython)
  n = 0.02468
FEATURE [App::DocumentObjectGroupPython] C_element021  label="C_element : 0.502"  # scripted group (container) (typed FeaturePython)
  n = 0.501611
FEATURE [App::DocumentObjectGroupPython] O_element019  label="O_element : 0.005"  # scripted group (container) (typed FeaturePython)
  n = 0.004527
FEATURE [App::DocumentObjectGroupPython] F_element004  label="F_element : 0.465"  # scripted group (container) (typed FeaturePython)
  n = 0.465209
FEATURE [App::DocumentObjectGroupPython] Si_element001  label="Si_element : 0.004"  # scripted group (container) (typed FeaturePython)
  n = 0.003973
FEATURE [App::DocumentObjectGroupPython] G4_C_552  label="G4_C-552"  # scripted group (container) (typed FeaturePython)
  Dunit = g/cm3
  Dvalue = 1.76
  Group = -> [H_element020,C_element021,O_element019,F_element004,Si_element001]
  conduct = 2
  density = 1
  expand = 3
  formula = G4_C-552
  name = G4_C-552
  specific = 4
FEATURE [App::DocumentObjectGroupPython] Cd_element001  label="Cd_element : 1"  # scripted group (container) (typed FeaturePython)
  n = 1
  ref = Cd_element
FEATURE [App::DocumentObjectGroupPython] Te_element001  label="Te_element : 1"  # scripted group (container) (typed FeaturePython)
  n = 1
  ref = Te_element
FEATURE [App::DocumentObjectGroupPython] G4_CADMIUM_TELLURIDE  # scripted group (container) (typed FeaturePython)
  Dunit = g/cm3
  Dvalue = 6.2
  Group = -> [Cd_element001,Te_element001]
  conduct = 2
  density = 1
  expand = 3
  formula = G4_CADMIUM_TELLURIDE
  name = G4_CADMIUM_TELLURIDE
  specific = 4
FEATURE [App::DocumentObjectGroupPython] Cd_element002  label="Cd_element : 002"  # scripted group (container) (typed FeaturePython)
  n = 1
  ref = Cd_element
FEATURE [App::DocumentObjectGroupPython] W_element001  label="W_element : 1"  # scripted group (container) (typed FeaturePython)
  n = 1
  ref = W_element
FEATURE [App::DocumentObjectGroupPython] O_element020  label="O_element : 008"  # scripted group (container) (typed FeaturePython)
  n = 4
  ref = O_element
FEATURE [App::DocumentObjectGroupPython] G4_CADMIUM_TUNGSTATE  # scripted group (container) (typed FeaturePython)
  Dunit = g/cm3
  Dvalue = 7.9
  Group = -> [Cd_element002,W_element001,O_element020]
  conduct = 2
  density = 1
  expand = 3
  formula = G4_CADMIUM_TUNGSTATE
  name = G4_CADMIUM_TUNGSTATE
  specific = 4
FEATURE [App::DocumentObjectGroupPython] Ca_element005  label="Ca_element : 1"  # scripted group (container) (typed FeaturePython)
  n = 1
  ref = Ca_element
FEATURE [App::DocumentObjectGroupPython] C_element022  label="C_element : 009"  # scripted group (container) (typed FeaturePython)
  n = 1
  ref = C_element
FEATURE [App::DocumentObjectGroupPython] O_element021  label="O_element : 009"  # scripted group (container) (typed FeaturePython)
  n = 3
  ref = O_element
FEATURE [App::DocumentObjectGroupPython] G4_CALCIUM_CARBONATE  # scripted group (container) (typed FeaturePython)
  Dunit = g/cm3
  Dvalue = 2.8
  Group = -> [Ca_element005,C_element022,O_element021]
  conduct = 2
  density = 1
  expand = 3
  formula = G4_CALCIUM_CARBONATE
  name = G4_CALCIUM_CARBONATE
  specific = 4
FEATURE [App::DocumentObjectGroupPython] Ca_element006  label="Ca_element : 002"  # scripted group (container) (typed FeaturePython)
  n = 1
  ref = Ca_element
FEATURE [App::DocumentObjectGroupPython] F_element005  label="F_element : 003"  # scripted group (container) (typed FeaturePython)
  n = 2
  ref = F_element
FEATURE [App::DocumentObjectGroupPython] G4_CALCIUM_FLUORIDE  # scripted group (container) (typed FeaturePython)
  Dunit = g/cm3
  Dvalue = 3.18
  Group = -> [Ca_element006,F_element005]
  conduct = 2
  density = 1
  expand = 3
  formula = G4_CALCIUM_FLUORIDE
  name = G4_CALCIUM_FLUORIDE
  specific = 4
FEATURE [App::DocumentObjectGroupPython] Ca_element007  label="Ca_element : 003"  # scripted group (container) (typed FeaturePython)
  n = 1
  ref = Ca_element
FEATURE [App::DocumentObjectGroupPython] O_element022  label="O_element : 010"  # scripted group (container) (typed FeaturePython)
  n = 1
  ref = O_element
FEATURE [App::DocumentObjectGroupPython] G4_CALCIUM_OXIDE  # scripted group (container) (typed FeaturePython)
  Dunit = g/cm3
  Dvalue = 3.3
  Group = -> [Ca_element007,O_element022]
  conduct = 2
  density = 1
  expand = 3
  formula = G4_CALCIUM_OXIDE
  name = G4_CALCIUM_OXIDE
  specific = 4
FEATURE [App::DocumentObjectGroupPython] Ca_element008  label="Ca_element : 004"  # scripted group (container) (typed FeaturePython)
  n = 1
  ref = Ca_element
FEATURE [App::DocumentObjectGroupPython] S_element007  label="S_element : 002"  # scripted group (container) (typed FeaturePython)
  n = 1
  ref = S_element
FEATURE [App::DocumentObjectGroupPython] O_element023  label="O_element : 011"  # scripted group (container) (typed FeaturePython)
  n = 4
  ref = O_element
FEATURE [App::DocumentObjectGroupPython] G4_CALCIUM_SULFATE  # scripted group (container) (typed FeaturePython)
  Dunit = g/cm3
  Dvalue = 2.96
  Group = -> [Ca_element008,S_element007,O_element023]
  conduct = 2
  density = 1
  expand = 3
  formula = G4_CALCIUM_SULFATE
  name = G4_CALCIUM_SULFATE
  specific = 4
FEATURE [App::DocumentObjectGroupPython] Ca_element009  label="Ca_element : 005"  # scripted group (container) (typed FeaturePython)
  n = 1
  ref = Ca_element
FEATURE [App::DocumentObjectGroupPython] W_element002  label="W_element : 002"  # scripted group (container) (typed FeaturePython)
  n = 1
  ref = W_element
FEATURE [App::DocumentObjectGroupPython] O_element024  label="O_element : 012"  # scripted group (container) (typed FeaturePython)
  n = 4
  ref = O_element
FEATURE [App::DocumentObjectGroupPython] G4_CALCIUM_TUNGSTATE  # scripted group (container) (typed FeaturePython)
  Dunit = g/cm3
  Dvalue = 6.062
  Group = -> [Ca_element009,W_element002,O_element024]
  conduct = 2
  density = 1
  expand = 3
  formula = G4_CALCIUM_TUNGSTATE
  name = G4_CALCIUM_TUNGSTATE
  specific = 4
FEATURE [App::DocumentObjectGroupPython] C_element023  label="C_element : 010"  # scripted group (container) (typed FeaturePython)
  n = 1
  ref = C_element
FEATURE [App::DocumentObjectGroupPython] O_element025  label="O_element : 013"  # scripted group (container) (typed FeaturePython)
  n = 2
  ref = O_element
FEATURE [App::DocumentObjectGroupPython] G4_CARBON_DIOXIDE  # scripted group (container) (typed FeaturePython)
  Dunit = g/cm3
  Dvalue = 0.00184212
  Group = -> [C_element023,O_element025]
  conduct = 2
  density = 1
  expand = 3
  formula = G4_CARBON_DIOXIDE
  name = G4_CARBON_DIOXIDE
  specific = 4
FEATURE [App::DocumentObjectGroupPython] C_element024  label="C_element : 011"  # scripted group (container) (typed FeaturePython)
  n = 1
  ref = C_element
FEATURE [App::DocumentObjectGroupPython] Cl_element004  label="Cl_element : 4"  # scripted group (container) (typed FeaturePython)
  n = 4
  ref = Cl_element
FEATURE [App::DocumentObjectGroupPython] G4_CARBON_TETRACHLORIDE  # scripted group (container) (typed FeaturePython)
  Dunit = g/cm3
  Dvalue = 1.594
  Group = -> [C_element024,Cl_element004]
  conduct = 2
  density = 1
  expand = 3
  formula = G4_CARBON_TETRACHLORIDE
  name = G4_CARBON_TETRACHLORIDE
  specific = 4
FEATURE [App::DocumentObjectGroupPython] C_element025  label="C_element : 012"  # scripted group (container) (typed FeaturePython)
  n = 6
  ref = C_element
FEATURE [App::DocumentObjectGroupPython] H_element021  label="H_element : 012"  # scripted group (container) (typed FeaturePython)
  n = 10
  ref = H_element
FEATURE [App::DocumentObjectGroupPython] O_element026  label="O_element : 5"  # scripted group (container) (typed FeaturePython)
  n = 5
  ref = O_element
FEATURE [App::DocumentObjectGroupPython] G4_CELLULOSE_CELLOPHANE  # scripted group (container) (typed FeaturePython)
  Dunit = g/cm3
  Dvalue = 1.42
  Group = -> [C_element025,H_element021,O_element026]
  conduct = 2
  density = 1
  expand = 3
  formula = G4_CELLULOSE_CELLOPHANE
  name = G4_CELLULOSE_CELLOPHANE
  specific = 4
FEATURE [App::DocumentObjectGroupPython] H_element022  label="H_element : 0.067"  # scripted group (container) (typed FeaturePython)
  n = 0.067125
FEATURE [App::DocumentObjectGroupPython] C_element026  label="C_element : 0.545"  # scripted group (container) (typed FeaturePython)
  n = 0.545403
FEATURE [App::DocumentObjectGroupPython] O_element027  label="O_element : 0.387"  # scripted group (container) (typed FeaturePython)
  n = 0.387472
FEATURE [App::DocumentObjectGroupPython] G4_CELLULOSE_BUTYRATE  # scripted group (container) (typed FeaturePython)
  Dunit = g/cm3
  Dvalue = 1.2
  Group = -> [H_element022,C_element026,O_element027]
  conduct = 2
  density = 1
  expand = 3
  formula = G4_CELLULOSE_BUTYRATE
  name = G4_CELLULOSE_BUTYRATE
  specific = 4
FEATURE [App::DocumentObjectGroupPython] H_element023  label="H_element : 0.029"  # scripted group (container) (typed FeaturePython)
  n = 0.029216
FEATURE [App::DocumentObjectGroupPython] C_element027  label="C_element : 0.271"  # scripted group (container) (typed FeaturePython)
  n = 0.271296
FEATURE [App::DocumentObjectGroupPython] N_element013  label="N_element : 0.121"  # scripted group (container) (typed FeaturePython)
  n = 0.121276
FEATURE [App::DocumentObjectGroupPython] O_element028  label="O_element : 0.578"  # scripted group (container) (typed FeaturePython)
  n = 0.578212
FEATURE [App::DocumentObjectGroupPython] G4_CELLULOSE_NITRATE  # scripted group (container) (typed FeaturePython)
  Dunit = g/cm3
  Dvalue = 1.49
  Group = -> [H_element023,C_element027,N_element013,O_element028]
  conduct = 2
  density = 1
  expand = 3
  formula = G4_CELLULOSE_NITRATE
  name = G4_CELLULOSE_NITRATE
  specific = 4
FEATURE [App::DocumentObjectGroupPython] H_element024  label="H_element : 0.108"  # scripted group (container) (typed FeaturePython)
  n = 0.107596
FEATURE [App::DocumentObjectGroupPython] N_element014  label="N_element : 0.001"  # scripted group (container) (typed FeaturePython)
  n = 0.0008
FEATURE [App::DocumentObjectGroupPython] O_element029  label="O_element : 0.875"  # scripted group (container) (typed FeaturePython)
  n = 0.874976
FEATURE [App::DocumentObjectGroupPython] S_element008  label="S_element : 0.015"  # scripted group (container) (typed FeaturePython)
  n = 0.014627
FEATURE [App::DocumentObjectGroupPython] Ce_element001  label="Ce_element : 0.002"  # scripted group (container) (typed FeaturePython)
  n = 0.002001
FEATURE [App::DocumentObjectGroupPython] G4_CERIC_SULFATE  # scripted group (container) (typed FeaturePython)
  Dunit = g/cm3
  Dvalue = 1.03
  Group = -> [H_element024,N_element014,O_element029,S_element008,Ce_element001]
  conduct = 2
  density = 1
  expand = 3
  formula = G4_CERIC_SULFATE
  name = G4_CERIC_SULFATE
  specific = 4
FEATURE [App::DocumentObjectGroupPython] Cs_element001  label="Cs_element : 1"  # scripted group (container) (typed FeaturePython)
  n = 1
  ref = Cs_element
FEATURE [App::DocumentObjectGroupPython] F_element006  label="F_element : 1"  # scripted group (container) (typed FeaturePython)
  n = 1
  ref = F_element
FEATURE [App::DocumentObjectGroupPython] G4_CESIUM_FLUORIDE  # scripted group (container) (typed FeaturePython)
  Dunit = g/cm3
  Dvalue = 4.115
  Group = -> [Cs_element001,F_element006]
  conduct = 2
  density = 1
  expand = 3
  formula = G4_CESIUM_FLUORIDE
  name = G4_CESIUM_FLUORIDE
  specific = 4
FEATURE [App::DocumentObjectGroupPython] Cs_element002  label="Cs_element : 002"  # scripted group (container) (typed FeaturePython)
  n = 1
  ref = Cs_element
FEATURE [App::DocumentObjectGroupPython] I_element001  label="I_element : 1"  # scripted group (container) (typed FeaturePython)
  n = 1
  ref = I_element
FEATURE [App::DocumentObjectGroupPython] G4_CESIUM_IODIDE  # scripted group (container) (typed FeaturePython)
  Dunit = g/cm3
  Dvalue = 4.51
  Group = -> [Cs_element002,I_element001]
  conduct = 2
  density = 1
  expand = 3
  formula = G4_CESIUM_IODIDE
  name = G4_CESIUM_IODIDE
  specific = 4
FEATURE [App::DocumentObjectGroupPython] C_element028  label="C_element : 013"  # scripted group (container) (typed FeaturePython)
  n = 6
  ref = C_element
FEATURE [App::DocumentObjectGroupPython] H_element025  label="H_element : 013"  # scripted group (container) (typed FeaturePython)
  n = 5
  ref = H_element
FEATURE [App::DocumentObjectGroupPython] Cl_element005  label="Cl_element : 1"  # scripted group (container) (typed FeaturePython)
  n = 1
  ref = Cl_element
FEATURE [App::DocumentObjectGroupPython] G4_CHLOROBENZENE  # scripted group (container) (typed FeaturePython)
  Dunit = g/cm3
  Dvalue = 1.1058
  Group = -> [C_element028,H_element025,Cl_element005]
  conduct = 2
  density = 1
  expand = 3
  formula = G4_CHLOROBENZENE
  name = G4_CHLOROBENZENE
  specific = 4
FEATURE [App::DocumentObjectGroupPython] C_element029  label="C_element : 014"  # scripted group (container) (typed FeaturePython)
  n = 1
  ref = C_element
FEATURE [App::DocumentObjectGroupPython] H_element026  label="H_element : 1"  # scripted group (container) (typed FeaturePython)
  n = 1
  ref = H_element
FEATURE [App::DocumentObjectGroupPython] Cl_element006  label="Cl_element : 3"  # scripted group (container) (typed FeaturePython)
  n = 3
  ref = Cl_element
FEATURE [App::DocumentObjectGroupPython] G4_CHLOROFORM  # scripted group (container) (typed FeaturePython)
  Dunit = g/cm3
  Dvalue = 1.4832
  Group = -> [C_element029,H_element026,Cl_element006]
  conduct = 2
  density = 1
  expand = 3
  formula = G4_CHLOROFORM
  name = G4_CHLOROFORM
  specific = 4
FEATURE [App::DocumentObjectGroupPython] H_element027  label="H_element : 0.010"  # scripted group (container) (typed FeaturePython)
  n = 0.01
FEATURE [App::DocumentObjectGroupPython] C_element030  label="C_element : 0.001"  # scripted group (container) (typed FeaturePython)
  n = 0.001
FEATURE [App::DocumentObjectGroupPython] O_element030  label="O_element : 0.529"  # scripted group (container) (typed FeaturePython)
  n = 0.529107
FEATURE [App::DocumentObjectGroupPython] Na_element005  label="Na_element : 0.016"  # scripted group (container) (typed FeaturePython)
  n = 0.016
FEATURE [App::DocumentObjectGroupPython] Mg_element003  label="Mg_element : 0.004"  # scripted group (container) (typed FeaturePython)
  n = 0.002
FEATURE [App::DocumentObjectGroupPython] Al_element002  label="Al_element : 0.034"  # scripted group (container) (typed FeaturePython)
  n = 0.033872
FEATURE [App::DocumentObjectGroupPython] Si_element002  label="Si_element : 0.337"  # scripted group (container) (typed FeaturePython)
  n = 0.337021
FEATURE [App::DocumentObjectGroupPython] K_element003  label="K_element : 0.013"  # scripted group (container) (typed FeaturePython)
  n = 0.013
FEATURE [App::DocumentObjectGroupPython] Ca_element010  label="Ca_element : 0.044"  # scripted group (container) (typed FeaturePython)
  n = 0.044
FEATURE [App::DocumentObjectGroupPython] Fe_element002  label="Fe_element : 0.014"  # scripted group (container) (typed FeaturePython)
  n = 0.014
FEATURE [App::DocumentObjectGroupPython] G4_CONCRETE  # scripted group (container) (typed FeaturePython)
  Dunit = g/cm3
  Dvalue = 2.3
  Group = -> [H_element027,C_element030,O_element030,Na_element005,Mg_element003,Al_element002,Si_element002,K_element003,Ca_element010,Fe_element002]
  conduct = 2
  density = 1
  expand = 3
  formula = G4_CONCRETE
  name = G4_CONCRETE
  specific = 4
FEATURE [App::DocumentObjectGroupPython] C_element031  label="C_element : 015"  # scripted group (container) (typed FeaturePython)
  n = 6
  ref = C_element
FEATURE [App::DocumentObjectGroupPython] H_element028  label="H_element : 12"  # scripted group (container) (typed FeaturePython)
  n = 12
  ref = H_element
FEATURE [App::DocumentObjectGroupPython] G4_CYCLOHEXANE  # scripted group (container) (typed FeaturePython)
  Dunit = g/cm3
  Dvalue = 0.779
  Group = -> [C_element031,H_element028]
  conduct = 2
  density = 1
  expand = 3
  formula = G4_CYCLOHEXANE
  name = G4_CYCLOHEXANE
  specific = 4
FEATURE [App::DocumentObjectGroupPython] C_element032  label="C_element : 016"  # scripted group (container) (typed FeaturePython)
  n = 6
  ref = C_element
FEATURE [App::DocumentObjectGroupPython] H_element029  label="H_element : 4"  # scripted group (container) (typed FeaturePython)
  n = 4
  ref = H_element
FEATURE [App::DocumentObjectGroupPython] Cl_element007  label="Cl_element : 2"  # scripted group (container) (typed FeaturePython)
  n = 2
  ref = Cl_element
FEATURE [App::DocumentObjectGroupPython] G4_1_2_DICHLOROBENZENE  label="G4_1.2-DICHLOROBENZENE"  # scripted group (container) (typed FeaturePython)
  Dunit = g/cm3
  Dvalue = 1.3048
  Group = -> [C_element032,H_element029,Cl_element007]
  conduct = 2
  density = 1
  expand = 3
  formula = G4_1.2-DICHLOROBENZENE
  name = G4_1.2-DICHLOROBENZENE
  specific = 4
FEATURE [App::DocumentObjectGroupPython] C_element033  label="C_element : 017"  # scripted group (container) (typed FeaturePython)
  n = 4
  ref = C_element
FEATURE [App::DocumentObjectGroupPython] H_element030  label="H_element : 8"  # scripted group (container) (typed FeaturePython)
  n = 8
  ref = H_element
FEATURE [App::DocumentObjectGroupPython] O_element031  label="O_element : 014"  # scripted group (container) (typed FeaturePython)
  n = 1
  ref = O_element
FEATURE [App::DocumentObjectGroupPython] Cl_element008  label="Cl_element : 005"  # scripted group (container) (typed FeaturePython)
  n = 2
  ref = Cl_element
FEATURE [App::DocumentObjectGroupPython] G4_DICHLORODIETHYL_ETHER  # scripted group (container) (typed FeaturePython)
  Dunit = g/cm3
  Dvalue = 1.2199
  Group = -> [C_element033,H_element030,O_element031,Cl_element008]
  conduct = 2
  density = 1
  expand = 3
  formula = G4_DICHLORODIETHYL_ETHER
  name = G4_DICHLORODIETHYL_ETHER
  specific = 4
FEATURE [App::DocumentObjectGroupPython] C_element034  label="C_element : 018"  # scripted group (container) (typed FeaturePython)
  n = 2
  ref = C_element
FEATURE [App::DocumentObjectGroupPython] H_element031  label="H_element : 014"  # scripted group (container) (typed FeaturePython)
  n = 4
  ref = H_element
FEATURE [App::DocumentObjectGroupPython] Cl_element009  label="Cl_element : 006"  # scripted group (container) (typed FeaturePython)
  n = 2
  ref = Cl_element
FEATURE [App::DocumentObjectGroupPython] G4_1_2_DICHLOROETHANE  label="G4_1.2-DICHLOROETHANE"  # scripted group (container) (typed FeaturePython)
  Dunit = g/cm3
  Dvalue = 1.2351
  Group = -> [C_element034,H_element031,Cl_element009]
  conduct = 2
  density = 1
  expand = 3
  formula = G4_1.2-DICHLOROETHANE
  name = G4_1.2-DICHLOROETHANE
  specific = 4
FEATURE [App::DocumentObjectGroupPython] C_element035  label="C_element : 019"  # scripted group (container) (typed FeaturePython)
  n = 4
  ref = C_element
FEATURE [App::DocumentObjectGroupPython] H_element032  label="H_element : 015"  # scripted group (container) (typed FeaturePython)
  n = 10
  ref = H_element
FEATURE [App::DocumentObjectGroupPython] O_element032  label="O_element : 015"  # scripted group (container) (typed FeaturePython)
  n = 1
  ref = O_element
FEATURE [App::DocumentObjectGroupPython] G4_DIETHYL_ETHER  # scripted group (container) (typed FeaturePython)
  Dunit = g/cm3
  Dvalue = 0.71378
  Group = -> [C_element035,H_element032,O_element032]
  conduct = 2
  density = 1
  expand = 3
  formula = G4_DIETHYL_ETHER
  name = G4_DIETHYL_ETHER
  specific = 4
FEATURE [App::DocumentObjectGroupPython] C_element036  label="C_element : 020"  # scripted group (container) (typed FeaturePython)
  n = 3
  ref = C_element
FEATURE [App::DocumentObjectGroupPython] H_element033  label="H_element : 016"  # scripted group (container) (typed FeaturePython)
  n = 7
  ref = H_element
FEATURE [App::DocumentObjectGroupPython] N_element015  label="N_element : 008"  # scripted group (container) (typed FeaturePython)
  n = 1
  ref = N_element
FEATURE [App::DocumentObjectGroupPython] O_element033  label="O_element : 016"  # scripted group (container) (typed FeaturePython)
  n = 1
  ref = O_element
FEATURE [App::DocumentObjectGroupPython] G4_N_N_DIMETHYL_FORMAMIDE  label="G4_N.N-DIMETHYL_FORMAMIDE"  # scripted group (container) (typed FeaturePython)
  Dunit = g/cm3
  Dvalue = 0.9487
  Group = -> [C_element036,H_element033,N_element015,O_element033]
  conduct = 2
  density = 1
  expand = 3
  formula = G4_N.N-DIMETHYL_FORMAMIDE
  name = G4_N.N-DIMETHYL_FORMAMIDE
  specific = 4
FEATURE [App::DocumentObjectGroupPython] C_element037  label="C_element : 021"  # scripted group (container) (typed FeaturePython)
  n = 2
  ref = C_element
FEATURE [App::DocumentObjectGroupPython] H_element034  label="H_element : 017"  # scripted group (container) (typed FeaturePython)
  n = 6
  ref = H_element
FEATURE [App::DocumentObjectGroupPython] O_element034  label="O_element : 017"  # scripted group (container) (typed FeaturePython)
  n = 1
  ref = O_element
FEATURE [App::DocumentObjectGroupPython] S_element009  label="S_element : 003"  # scripted group (container) (typed FeaturePython)
  n = 1
  ref = S_element
FEATURE [App::DocumentObjectGroupPython] G4_DIMETHYL_SULFOXIDE  # scripted group (container) (typed FeaturePython)
  Dunit = g/cm3
  Dvalue = 1.1014
  Group = -> [C_element037,H_element034,O_element034,S_element009]
  conduct = 2
  density = 1
  expand = 3
  formula = G4_DIMETHYL_SULFOXIDE
  name = G4_DIMETHYL_SULFOXIDE
  specific = 4
FEATURE [App::DocumentObjectGroupPython] C_element038  label="C_element : 022"  # scripted group (container) (typed FeaturePython)
  n = 2
  ref = C_element
FEATURE [App::DocumentObjectGroupPython] H_element035  label="H_element : 018"  # scripted group (container) (typed FeaturePython)
  n = 6
  ref = H_element
FEATURE [App::DocumentObjectGroupPython] G4_ETHANE  # scripted group (container) (typed FeaturePython)
  Dunit = g/cm3
  Dvalue = 0.00125324
  Group = -> [C_element038,H_element035]
  conduct = 2
  density = 1
  expand = 3
  formula = G4_ETHANE
  name = G4_ETHANE
  specific = 4
FEATURE [App::DocumentObjectGroupPython] C_element039  label="C_element : 023"  # scripted group (container) (typed FeaturePython)
  n = 2
  ref = C_element
FEATURE [App::DocumentObjectGroupPython] H_element036  label="H_element : 019"  # scripted group (container) (typed FeaturePython)
  n = 6
  ref = H_element
FEATURE [App::DocumentObjectGroupPython] O_element035  label="O_element : 018"  # scripted group (container) (typed FeaturePython)
  n = 1
  ref = O_element
FEATURE [App::DocumentObjectGroupPython] G4_ETHYL_ALCOHOL  # scripted group (container) (typed FeaturePython)
  Dunit = g/cm3
  Dvalue = 0.7893
  Group = -> [C_element039,H_element036,O_element035]
  conduct = 2
  density = 1
  expand = 3
  formula = G4_ETHYL_ALCOHOL
  name = G4_ETHYL_ALCOHOL
  specific = 4
FEATURE [App::DocumentObjectGroupPython] H_element037  label="H_element : 0.090"  # scripted group (container) (typed FeaturePython)
  n = 0.090027
FEATURE [App::DocumentObjectGroupPython] C_element040  label="C_element : 0.585"  # scripted group (container) (typed FeaturePython)
  n = 0.585182
FEATURE [App::DocumentObjectGroupPython] O_element036  label="O_element : 0.325"  # scripted group (container) (typed FeaturePython)
  n = 0.324791
FEATURE [App::DocumentObjectGroupPython] G4_ETHYL_CELLULOSE  # scripted group (container) (typed FeaturePython)
  Dunit = g/cm3
  Dvalue = 1.13
  Group = -> [H_element037,C_element040,O_element036]
  conduct = 2
  density = 1
  expand = 3
  formula = G4_ETHYL_CELLULOSE
  name = G4_ETHYL_CELLULOSE
  specific = 4
FEATURE [App::DocumentObjectGroupPython] C_element041  label="C_element : 024"  # scripted group (container) (typed FeaturePython)
  n = 2
  ref = C_element
FEATURE [App::DocumentObjectGroupPython] H_element038  label="H_element : 020"  # scripted group (container) (typed FeaturePython)
  n = 4
  ref = H_element
FEATURE [App::DocumentObjectGroupPython] G4_ETHYLENE  # scripted group (container) (typed FeaturePython)
  Dunit = g/cm3
  Dvalue = 0.00117497
  Group = -> [C_element041,H_element038]
  conduct = 2
  density = 1
  expand = 3
  formula = G4_ETHYLENE
  name = G4_ETHYLENE
  specific = 4
FEATURE [App::DocumentObjectGroupPython] H_element039  label="H_element : 0.096"  # scripted group (container) (typed FeaturePython)
  n = 0.096
FEATURE [App::DocumentObjectGroupPython] C_element042  label="C_element : 0.195"  # scripted group (container) (typed FeaturePython)
  n = 0.195
FEATURE [App::DocumentObjectGroupPython] N_element016  label="N_element : 0.057"  # scripted group (container) (typed FeaturePython)
  n = 0.057
FEATURE [App::DocumentObjectGroupPython] O_element037  label="O_element : 0.646"  # scripted group (container) (typed FeaturePython)
  n = 0.646
FEATURE [App::DocumentObjectGroupPython] Na_element006  label="Na_element : 0.017"  # scripted group (container) (typed FeaturePython)
  n = 0.001
FEATURE [App::DocumentObjectGroupPython] P_element005  label="P_element : 0.104"  # scripted group (container) (typed FeaturePython)
  n = 0.001
FEATURE [App::DocumentObjectGroupPython] S_element010  label="S_element : 0.016"  # scripted group (container) (typed FeaturePython)
  n = 0.003
FEATURE [App::DocumentObjectGroupPython] Cl_element010  label="Cl_element : 0.005"  # scripted group (container) (typed FeaturePython)
  n = 0.001
FEATURE [App::DocumentObjectGroupPython] G4_EYE_LENS_ICRP  # scripted group (container) (typed FeaturePython)
  Dunit = g/cm3
  Dvalue = 1.07
  Group = -> [H_element039,C_element042,N_element016,O_element037,Na_element006,P_element005,S_element010,Cl_element010]
  conduct = 2
  density = 1
  expand = 3
  formula = G4_EYE_LENS_ICRP
  name = G4_EYE_LENS_ICRP
  specific = 4
FEATURE [App::DocumentObjectGroupPython] Fe_element003  label="Fe_element : 2"  # scripted group (container) (typed FeaturePython)
  n = 2
  ref = Fe_element
FEATURE [App::DocumentObjectGroupPython] O_element038  label="O_element : 019"  # scripted group (container) (typed FeaturePython)
  n = 3
  ref = O_element
FEATURE [App::DocumentObjectGroupPython] G4_FERRIC_OXIDE  # scripted group (container) (typed FeaturePython)
  Dunit = g/cm3
  Dvalue = 5.2
  Group = -> [Fe_element003,O_element038]
  conduct = 2
  density = 1
  expand = 3
  formula = G4_FERRIC_OXIDE
  name = G4_FERRIC_OXIDE
  specific = 4
FEATURE [App::DocumentObjectGroupPython] Fe_element004  label="Fe_element : 1"  # scripted group (container) (typed FeaturePython)
  n = 1
  ref = Fe_element
FEATURE [App::DocumentObjectGroupPython] B_element003  label="B_element : 1"  # scripted group (container) (typed FeaturePython)
  n = 1
  ref = B_element
FEATURE [App::DocumentObjectGroupPython] G4_FERROBORIDE  # scripted group (container) (typed FeaturePython)
  Dunit = g/cm3
  Dvalue = 7.15
  Group = -> [Fe_element004,B_element003]
  conduct = 2
  density = 1
  expand = 3
  formula = G4_FERROBORIDE
  name = G4_FERROBORIDE
  specific = 4
FEATURE [App::DocumentObjectGroupPython] Fe_element005  label="Fe_element : 003"  # scripted group (container) (typed FeaturePython)
  n = 1
  ref = Fe_element
FEATURE [App::DocumentObjectGroupPython] O_element039  label="O_element : 020"  # scripted group (container) (typed FeaturePython)
  n = 1
  ref = O_element
FEATURE [App::DocumentObjectGroupPython] G4_FERROUS_OXIDE  # scripted group (container) (typed FeaturePython)
  Dunit = g/cm3
  Dvalue = 5.7
  Group = -> [Fe_element005,O_element039]
  conduct = 2
  density = 1
  expand = 3
  formula = G4_FERROUS_OXIDE
  name = G4_FERROUS_OXIDE
  specific = 4
FEATURE [App::DocumentObjectGroupPython] H_element040  label="H_element : 0.115"  # scripted group (container) (typed FeaturePython)
  n = 0.108259
FEATURE [App::DocumentObjectGroupPython] N_element017  label="N_element : 0.000"  # scripted group (container) (typed FeaturePython)
  n = 2.7e-05
FEATURE [App::DocumentObjectGroupPython] O_element040  label="O_element : 0.879"  # scripted group (container) (typed FeaturePython)
  n = 0.878636
FEATURE [App::DocumentObjectGroupPython] Na_element007  label="Na_element : 0.000"  # scripted group (container) (typed FeaturePython)
  n = 2.2e-05
FEATURE [App::DocumentObjectGroupPython] S_element011  label="S_element : 0.013"  # scripted group (container) (typed FeaturePython)
  n = 0.012968
FEATURE [App::DocumentObjectGroupPython] Cl_element011  label="Cl_element : 0.000"  # scripted group (container) (typed FeaturePython)
  n = 3.4e-05
FEATURE [App::DocumentObjectGroupPython] Fe_element006  label="Fe_element : 0.000"  # scripted group (container) (typed FeaturePython)
  n = 5.4e-05
FEATURE [App::DocumentObjectGroupPython] G4_FERROUS_SULFATE  # scripted group (container) (typed FeaturePython)
  Dunit = g/cm3
  Dvalue = 1.024
  Group = -> [H_element040,N_element017,O_element040,Na_element007,S_element011,Cl_element011,Fe_element006]
  conduct = 2
  density = 1
  expand = 3
  formula = G4_FERROUS_SULFATE
  name = G4_FERROUS_SULFATE
  specific = 4
FEATURE [App::DocumentObjectGroupPython] C_element043  label="C_element : 0.099"  # scripted group (container) (typed FeaturePython)
  n = 0.099335
FEATURE [App::DocumentObjectGroupPython] F_element007  label="F_element : 0.314"  # scripted group (container) (typed FeaturePython)
  n = 0.314247
FEATURE [App::DocumentObjectGroupPython] Cl_element012  label="Cl_element : 0.586"  # scripted group (container) (typed FeaturePython)
  n = 0.586418
FEATURE [App::DocumentObjectGroupPython] G4_FREON_12  label="G4_FREON-12"  # scripted group (container) (typed FeaturePython)
  Dunit = g/cm3
  Dvalue = 1.12
  Group = -> [C_element043,F_element007,Cl_element012]
  conduct = 2
  density = 1
  expand = 3
  formula = G4_FREON-12
  name = G4_FREON-12
  specific = 4
FEATURE [App::DocumentObjectGroupPython] C_element044  label="C_element : 0.057"  # scripted group (container) (typed FeaturePython)
  n = 0.057245
FEATURE [App::DocumentObjectGroupPython] F_element008  label="F_element : 0.181"  # scripted group (container) (typed FeaturePython)
  n = 0.181096
FEATURE [App::DocumentObjectGroupPython] Br_element001  label="Br_element : 0.762"  # scripted group (container) (typed FeaturePython)
  n = 0.761659
FEATURE [App::DocumentObjectGroupPython] G4_FREON_12B2  label="G4_FREON-12B2"  # scripted group (container) (typed FeaturePython)
  Dunit = g/cm3
  Dvalue = 1.8
  Group = -> [C_element044,F_element008,Br_element001]
  conduct = 2
  density = 1
  expand = 3
  formula = G4_FREON-12B2
  name = G4_FREON-12B2
  specific = 4
FEATURE [App::DocumentObjectGroupPython] C_element045  label="C_element : 0.115"  # scripted group (container) (typed FeaturePython)
  n = 0.114983
FEATURE [App::DocumentObjectGroupPython] F_element009  label="F_element : 0.546"  # scripted group (container) (typed FeaturePython)
  n = 0.545621
FEATURE [App::DocumentObjectGroupPython] Cl_element013  label="Cl_element : 0.339"  # scripted group (container) (typed FeaturePython)
  n = 0.339396
FEATURE [App::DocumentObjectGroupPython] G4_FREON_13  label="G4_FREON-13"  # scripted group (container) (typed FeaturePython)
  Dunit = g/cm3
  Dvalue = 0.95
  Group = -> [C_element045,F_element009,Cl_element013]
  conduct = 2
  density = 1
  expand = 3
  formula = G4_FREON-13
  name = G4_FREON-13
  specific = 4
FEATURE [App::DocumentObjectGroupPython] C_element046  label="C_element : 025"  # scripted group (container) (typed FeaturePython)
  n = 1
  ref = C_element
FEATURE [App::DocumentObjectGroupPython] F_element010  label="F_element : 3"  # scripted group (container) (typed FeaturePython)
  n = 3
  ref = F_element
FEATURE [App::DocumentObjectGroupPython] Br_element002  label="Br_element : 1"  # scripted group (container) (typed FeaturePython)
  n = 1
  ref = Br_element
FEATURE [App::DocumentObjectGroupPython] G4_FREON_13B1  label="G4_FREON-13B1"  # scripted group (container) (typed FeaturePython)
  Dunit = g/cm3
  Dvalue = 1.5
  Group = -> [C_element046,F_element010,Br_element002]
  conduct = 2
  density = 1
  expand = 3
  formula = G4_FREON-13B1
  name = G4_FREON-13B1
  specific = 4
FEATURE [App::DocumentObjectGroupPython] C_element047  label="C_element : 0.061"  # scripted group (container) (typed FeaturePython)
  n = 0.061309
FEATURE [App::DocumentObjectGroupPython] F_element011  label="F_element : 0.291"  # scripted group (container) (typed FeaturePython)
  n = 0.290924
FEATURE [App::DocumentObjectGroupPython] I_element002  label="I_element : 0.648"  # scripted group (container) (typed FeaturePython)
  n = 0.647767
FEATURE [App::DocumentObjectGroupPython] G4_FREON_13I1  label="G4_FREON-13I1"  # scripted group (container) (typed FeaturePython)
  Dunit = g/cm3
  Dvalue = 1.8
  Group = -> [C_element047,F_element011,I_element002]
  conduct = 2
  density = 1
  expand = 3
  formula = G4_FREON-13I1
  name = G4_FREON-13I1
  specific = 4
FEATURE [App::DocumentObjectGroupPython] Gd_element001  label="Gd_element : 2"  # scripted group (container) (typed FeaturePython)
  n = 2
  ref = Gd_element
FEATURE [App::DocumentObjectGroupPython] O_element041  label="O_element : 021"  # scripted group (container) (typed FeaturePython)
  n = 2
  ref = O_element
FEATURE [App::DocumentObjectGroupPython] S_element012  label="S_element : 004"  # scripted group (container) (typed FeaturePython)
  n = 1
  ref = S_element
FEATURE [App::DocumentObjectGroupPython] G4_GADOLINIUM_OXYSULFIDE  # scripted group (container) (typed FeaturePython)
  Dunit = g/cm3
  Dvalue = 7.44
  Group = -> [Gd_element001,O_element041,S_element012]
  conduct = 2
  density = 1
  expand = 3
  formula = G4_GADOLINIUM_OXYSULFIDE
  name = G4_GADOLINIUM_OXYSULFIDE
  specific = 4
FEATURE [App::DocumentObjectGroupPython] Ga_element001  label="Ga_element : 1"  # scripted group (container) (typed FeaturePython)
  n = 1
  ref = Ga_element
FEATURE [App::DocumentObjectGroupPython] As_element001  label="As_element : 1"  # scripted group (container) (typed FeaturePython)
  n = 1
  ref = As_element
FEATURE [App::DocumentObjectGroupPython] G4_GALLIUM_ARSENIDE  # scripted group (container) (typed FeaturePython)
  Dunit = g/cm3
  Dvalue = 5.31
  Group = -> [Ga_element001,As_element001]
  conduct = 2
  density = 1
  expand = 3
  formula = G4_GALLIUM_ARSENIDE
  name = G4_GALLIUM_ARSENIDE
  specific = 4
FEATURE [App::DocumentObjectGroupPython] H_element041  label="H_element : 0.081"  # scripted group (container) (typed FeaturePython)
  n = 0.08118
FEATURE [App::DocumentObjectGroupPython] C_element048  label="C_element : 0.416"  # scripted group (container) (typed FeaturePython)
  n = 0.41606
FEATURE [App::DocumentObjectGroupPython] N_element018  label="N_element : 0.111"  # scripted group (container) (typed FeaturePython)
  n = 0.11124
FEATURE [App::DocumentObjectGroupPython] O_element042  label="O_element : 0.381"  # scripted group (container) (typed FeaturePython)
  n = 0.38064
FEATURE [App::DocumentObjectGroupPython] S_element013  label="S_element : 0.011"  # scripted group (container) (typed FeaturePython)
  n = 0.01088
FEATURE [App::DocumentObjectGroupPython] G4_GEL_PHOTO_EMULSION  # scripted group (container) (typed FeaturePython)
  Dunit = g/cm3
  Dvalue = 1.2914
  Group = -> [H_element041,C_element048,N_element018,O_element042,S_element013]
  conduct = 2
  density = 1
  expand = 3
  formula = G4_GEL_PHOTO_EMULSION
  name = G4_GEL_PHOTO_EMULSION
  specific = 4
FEATURE [App::DocumentObjectGroupPython] B_element004  label="B_element : 0.040"  # scripted group (container) (typed FeaturePython)
  n = 0.0400639
FEATURE [App::DocumentObjectGroupPython] O_element043  label="O_element : 0.540"  # scripted group (container) (typed FeaturePython)
  n = 0.539561
FEATURE [App::DocumentObjectGroupPython] Na_element008  label="Na_element : 0.028"  # scripted group (container) (typed FeaturePython)
  n = 0.0281909
FEATURE [App::DocumentObjectGroupPython] Al_element003  label="Al_element : 0.012"  # scripted group (container) (typed FeaturePython)
  n = 0.011644
FEATURE [App::DocumentObjectGroupPython] Si_element003  label="Si_element : 0.377"  # scripted group (container) (typed FeaturePython)
  n = 0.377219
FEATURE [App::DocumentObjectGroupPython] K_element004  label="K_element : 0.014"  # scripted group (container) (typed FeaturePython)
  n = 0.00332099
FEATURE [App::DocumentObjectGroupPython] G4_Pyrex_Glass  # scripted group (container) (typed FeaturePython)
  Dunit = g/cm3
  Dvalue = 2.23
  Group = -> [B_element004,O_element043,Na_element008,Al_element003,Si_element003,K_element004]
  conduct = 2
  density = 1
  expand = 3
  formula = G4_Pyrex_Glass
  name = G4_Pyrex_Glass
  specific = 4
FEATURE [App::DocumentObjectGroupPython] O_element044  label="O_element : 0.156"  # scripted group (container) (typed FeaturePython)
  n = 0.156453
FEATURE [App::DocumentObjectGroupPython] Si_element004  label="Si_element : 0.081"  # scripted group (container) (typed FeaturePython)
  n = 0.080866
FEATURE [App::DocumentObjectGroupPython] Ti_element001  label="Ti_element : 0.008"  # scripted group (container) (typed FeaturePython)
  n = 0.008092
FEATURE [App::DocumentObjectGroupPython] As_element002  label="As_element : 0.003"  # scripted group (container) (typed FeaturePython)
  n = 0.002651
FEATURE [App::DocumentObjectGroupPython] Pb_element001  label="Pb_element : 0.752"  # scripted group (container) (typed FeaturePython)
  n = 0.751938
FEATURE [App::DocumentObjectGroupPython] G4_GLASS_LEAD  # scripted group (container) (typed FeaturePython)
  Dunit = g/cm3
  Dvalue = 6.22
  Group = -> [O_element044,Si_element004,Ti_element001,As_element002,Pb_element001]
  conduct = 2
  density = 1
  expand = 3
  formula = G4_GLASS_LEAD
  name = G4_GLASS_LEAD
  specific = 4
FEATURE [App::DocumentObjectGroupPython] O_element045  label="O_element : 0.460"  # scripted group (container) (typed FeaturePython)
  n = 0.4598
FEATURE [App::DocumentObjectGroupPython] Na_element009  label="Na_element : 0.096"  # scripted group (container) (typed FeaturePython)
  n = 0.0964411
FEATURE [App::DocumentObjectGroupPython] Si_element005  label="Si_element : 0.378"  # scripted group (container) (typed FeaturePython)
  n = 0.336553
FEATURE [App::DocumentObjectGroupPython] Ca_element011  label="Ca_element : 0.107"  # scripted group (container) (typed FeaturePython)
  n = 0.107205
FEATURE [App::DocumentObjectGroupPython] G4_GLASS_PLATE  # scripted group (container) (typed FeaturePython)
  Dunit = g/cm3
  Dvalue = 2.4
  Group = -> [O_element045,Na_element009,Si_element005,Ca_element011]
  conduct = 2
  density = 1
  expand = 3
  formula = G4_GLASS_PLATE
  name = G4_GLASS_PLATE
  specific = 4
FEATURE [App::DocumentObjectGroupPython] C_element049  label="C_element : 026"  # scripted group (container) (typed FeaturePython)
  n = 5
  ref = C_element
FEATURE [App::DocumentObjectGroupPython] H_element042  label="H_element : 021"  # scripted group (container) (typed FeaturePython)
  n = 10
  ref = H_element
FEATURE [App::DocumentObjectGroupPython] N_element019  label="N_element : 2"  # scripted group (container) (typed FeaturePython)
  n = 2
  ref = N_element
FEATURE [App::DocumentObjectGroupPython] O_element046  label="O_element : 022"  # scripted group (container) (typed FeaturePython)
  n = 3
  ref = O_element
FEATURE [App::DocumentObjectGroupPython] G4_GLUTAMINE  # scripted group (container) (typed FeaturePython)
  Dunit = g/cm3
  Dvalue = 1.46
  Group = -> [C_element049,H_element042,N_element019,O_element046]
  conduct = 2
  density = 1
  expand = 3
  formula = G4_GLUTAMINE
  name = G4_GLUTAMINE
  specific = 4
FEATURE [App::DocumentObjectGroupPython] C_element050  label="C_element : 027"  # scripted group (container) (typed FeaturePython)
  n = 3
  ref = C_element
FEATURE [App::DocumentObjectGroupPython] H_element043  label="H_element : 022"  # scripted group (container) (typed FeaturePython)
  n = 8
  ref = H_element
FEATURE [App::DocumentObjectGroupPython] O_element047  label="O_element : 023"  # scripted group (container) (typed FeaturePython)
  n = 3
  ref = O_element
FEATURE [App::DocumentObjectGroupPython] G4_GLYCEROL  # scripted group (container) (typed FeaturePython)
  Dunit = g/cm3
  Dvalue = 1.2613
  Group = -> [C_element050,H_element043,O_element047]
  conduct = 2
  density = 1
  expand = 3
  formula = G4_GLYCEROL
  name = G4_GLYCEROL
  specific = 4
FEATURE [App::DocumentObjectGroupPython] C_element051  label="C_element : 028"  # scripted group (container) (typed FeaturePython)
  n = 5
  ref = C_element
FEATURE [App::DocumentObjectGroupPython] H_element044  label="H_element : 023"  # scripted group (container) (typed FeaturePython)
  n = 5
  ref = H_element
FEATURE [App::DocumentObjectGroupPython] N_element020  label="N_element : 009"  # scripted group (container) (typed FeaturePython)
  n = 5
  ref = N_element
FEATURE [App::DocumentObjectGroupPython] O_element048  label="O_element : 024"  # scripted group (container) (typed FeaturePython)
  n = 1
  ref = O_element
FEATURE [App::DocumentObjectGroupPython] G4_GUANINE  # scripted group (container) (typed FeaturePython)
  Dunit = g/cm3
  Dvalue = 2.2
  Group = -> [C_element051,H_element044,N_element020,O_element048]
  conduct = 2
  density = 1
  expand = 3
  formula = G4_GUANINE
  name = G4_GUANINE
  specific = 4
FEATURE [App::DocumentObjectGroupPython] Ca_element012  label="Ca_element : 006"  # scripted group (container) (typed FeaturePython)
  n = 1
  ref = Ca_element
FEATURE [App::DocumentObjectGroupPython] S_element014  label="S_element : 005"  # scripted group (container) (typed FeaturePython)
  n = 1
  ref = S_element
FEATURE [App::DocumentObjectGroupPython] O_element049  label="O_element : 6"  # scripted group (container) (typed FeaturePython)
  n = 6
  ref = O_element
FEATURE [App::DocumentObjectGroupPython] H_element045  label="H_element : 024"  # scripted group (container) (typed FeaturePython)
  n = 4
  ref = H_element
FEATURE [App::DocumentObjectGroupPython] G4_GYPSUM  # scripted group (container) (typed FeaturePython)
  Dunit = g/cm3
  Dvalue = 2.32
  Group = -> [Ca_element012,S_element014,O_element049,H_element045]
  conduct = 2
  density = 1
  expand = 3
  formula = G4_GYPSUM
  name = G4_GYPSUM
  specific = 4
FEATURE [App::DocumentObjectGroupPython] C_element052  label="C_element : 7"  # scripted group (container) (typed FeaturePython)
  n = 7
  ref = C_element
FEATURE [App::DocumentObjectGroupPython] H_element046  label="H_element : 16"  # scripted group (container) (typed FeaturePython)
  n = 16
  ref = H_element
FEATURE [App::DocumentObjectGroupPython] G4_N_HEPTANE  label="G4_N-HEPTANE"  # scripted group (container) (typed FeaturePython)
  Dunit = g/cm3
  Dvalue = 0.68376
  Group = -> [C_element052,H_element046]
  conduct = 2
  density = 1
  expand = 3
  formula = G4_N-HEPTANE
  name = G4_N-HEPTANE
  specific = 4
FEATURE [App::DocumentObjectGroupPython] C_element053  label="C_element : 029"  # scripted group (container) (typed FeaturePython)
  n = 6
  ref = C_element
FEATURE [App::DocumentObjectGroupPython] H_element047  label="H_element : 14"  # scripted group (container) (typed FeaturePython)
  n = 14
  ref = H_element
FEATURE [App::DocumentObjectGroupPython] G4_N_HEXANE  label="G4_N-HEXANE"  # scripted group (container) (typed FeaturePython)
  Dunit = g/cm3
  Dvalue = 0.6603
  Group = -> [C_element053,H_element047]
  conduct = 2
  density = 1
  expand = 3
  formula = G4_N-HEXANE
  name = G4_N-HEXANE
  specific = 4
FEATURE [App::DocumentObjectGroupPython] C_element054  label="C_element : 22"  # scripted group (container) (typed FeaturePython)
  n = 22
  ref = C_element
FEATURE [App::DocumentObjectGroupPython] H_element048  label="H_element : 025"  # scripted group (container) (typed FeaturePython)
  n = 10
  ref = H_element
FEATURE [App::DocumentObjectGroupPython] N_element021  label="N_element : 010"  # scripted group (container) (typed FeaturePython)
  n = 2
  ref = N_element
FEATURE [App::DocumentObjectGroupPython] O_element050  label="O_element : 025"  # scripted group (container) (typed FeaturePython)
  n = 5
  ref = O_element
FEATURE [App::DocumentObjectGroupPython] G4_KAPTON  # scripted group (container) (typed FeaturePython)
  Dunit = g/cm3
  Dvalue = 1.42
  Group = -> [C_element054,H_element048,N_element021,O_element050]
  conduct = 2
  density = 1
  expand = 3
  formula = G4_KAPTON
  name = G4_KAPTON
  specific = 4
FEATURE [App::DocumentObjectGroupPython] La_element001  label="La_element : 1"  # scripted group (container) (typed FeaturePython)
  n = 1
  ref = La_element
FEATURE [App::DocumentObjectGroupPython] Br_element003  label="Br_element : 002"  # scripted group (container) (typed FeaturePython)
  n = 1
  ref = Br_element
FEATURE [App::DocumentObjectGroupPython] O_element051  label="O_element : 026"  # scripted group (container) (typed FeaturePython)
  n = 1
  ref = O_element
FEATURE [App::DocumentObjectGroupPython] G4_LANTHANUM_OXYBROMIDE  # scripted group (container) (typed FeaturePython)
  Dunit = g/cm3
  Dvalue = 6.28
  Group = -> [La_element001,Br_element003,O_element051]
  conduct = 2
  density = 1
  expand = 3
  formula = G4_LANTHANUM_OXYBROMIDE
  name = G4_LANTHANUM_OXYBROMIDE
  specific = 4
FEATURE [App::DocumentObjectGroupPython] La_element002  label="La_element : 2"  # scripted group (container) (typed FeaturePython)
  n = 2
  ref = La_element
FEATURE [App::DocumentObjectGroupPython] O_element052  label="O_element : 027"  # scripted group (container) (typed FeaturePython)
  n = 2
  ref = O_element
FEATURE [App::DocumentObjectGroupPython] S_element015  label="S_element : 006"  # scripted group (container) (typed FeaturePython)
  n = 1
  ref = S_element
FEATURE [App::DocumentObjectGroupPython] G4_LANTHANUM_OXYSULFIDE  # scripted group (container) (typed FeaturePython)
  Dunit = g/cm3
  Dvalue = 5.86
  Group = -> [La_element002,O_element052,S_element015]
  conduct = 2
  density = 1
  expand = 3
  formula = G4_LANTHANUM_OXYSULFIDE
  name = G4_LANTHANUM_OXYSULFIDE
  specific = 4
FEATURE [App::DocumentObjectGroupPython] O_element053  label="O_element : 0.072"  # scripted group (container) (typed FeaturePython)
  n = 0.071682
FEATURE [App::DocumentObjectGroupPython] Pb_element002  label="Pb_element : 0.928"  # scripted group (container) (typed FeaturePython)
  n = 0.928318
FEATURE [App::DocumentObjectGroupPython] G4_LEAD_OXIDE  # scripted group (container) (typed FeaturePython)
  Dunit = g/cm3
  Dvalue = 9.53
  Group = -> [O_element053,Pb_element002]
  conduct = 2
  density = 1
  expand = 3
  formula = G4_LEAD_OXIDE
  name = G4_LEAD_OXIDE
  specific = 4
FEATURE [App::DocumentObjectGroupPython] Li_element001  label="Li_element : 1"  # scripted group (container) (typed FeaturePython)
  n = 1
  ref = Li_element
FEATURE [App::DocumentObjectGroupPython] N_element022  label="N_element : 011"  # scripted group (container) (typed FeaturePython)
  n = 1
  ref = N_element
FEATURE [App::DocumentObjectGroupPython] H_element049  label="H_element : 026"  # scripted group (container) (typed FeaturePython)
  n = 2
  ref = H_element
FEATURE [App::DocumentObjectGroupPython] G4_LITHIUM_AMIDE  # scripted group (container) (typed FeaturePython)
  Dunit = g/cm3
  Dvalue = 1.178
  Group = -> [Li_element001,N_element022,H_element049]
  conduct = 2
  density = 1
  expand = 3
  formula = G4_LITHIUM_AMIDE
  name = G4_LITHIUM_AMIDE
  specific = 4
FEATURE [App::DocumentObjectGroupPython] Li_element002  label="Li_element : 2"  # scripted group (container) (typed FeaturePython)
  n = 2
  ref = Li_element
FEATURE [App::DocumentObjectGroupPython] C_element055  label="C_element : 030"  # scripted group (container) (typed FeaturePython)
  n = 1
  ref = C_element
FEATURE [App::DocumentObjectGroupPython] O_element054  label="O_element : 028"  # scripted group (container) (typed FeaturePython)
  n = 3
  ref = O_element
FEATURE [App::DocumentObjectGroupPython] G4_LITHIUM_CARBONATE  # scripted group (container) (typed FeaturePython)
  Dunit = g/cm3
  Dvalue = 2.11
  Group = -> [Li_element002,C_element055,O_element054]
  conduct = 2
  density = 1
  expand = 3
  formula = G4_LITHIUM_CARBONATE
  name = G4_LITHIUM_CARBONATE
  specific = 4
FEATURE [App::DocumentObjectGroupPython] Li_element003  label="Li_element : 003"  # scripted group (container) (typed FeaturePython)
  n = 1
  ref = Li_element
FEATURE [App::DocumentObjectGroupPython] F_element012  label="F_element : 004"  # scripted group (container) (typed FeaturePython)
  n = 1
  ref = F_element
FEATURE [App::DocumentObjectGroupPython] G4_LITHIUM_FLUORIDE  # scripted group (container) (typed FeaturePython)
  Dunit = g/cm3
  Dvalue = 2.635
  Group = -> [Li_element003,F_element012]
  conduct = 2
  density = 1
  expand = 3
  formula = G4_LITHIUM_FLUORIDE
  name = G4_LITHIUM_FLUORIDE
  specific = 4
FEATURE [App::DocumentObjectGroupPython] Li_element004  label="Li_element : 004"  # scripted group (container) (typed FeaturePython)
  n = 1
  ref = Li_element
FEATURE [App::DocumentObjectGroupPython] H_element050  label="H_element : 027"  # scripted group (container) (typed FeaturePython)
  n = 1
  ref = H_element
FEATURE [App::DocumentObjectGroupPython] G4_LITHIUM_HYDRIDE  # scripted group (container) (typed FeaturePython)
  Dunit = g/cm3
  Dvalue = 0.82
  Group = -> [Li_element004,H_element050]
  conduct = 2
  density = 1
  expand = 3
  formula = G4_LITHIUM_HYDRIDE
  name = G4_LITHIUM_HYDRIDE
  specific = 4
FEATURE [App::DocumentObjectGroupPython] Li_element005  label="Li_element : 005"  # scripted group (container) (typed FeaturePython)
  n = 1
  ref = Li_element
FEATURE [App::DocumentObjectGroupPython] I_element003  label="I_element : 002"  # scripted group (container) (typed FeaturePython)
  n = 1
  ref = I_element
FEATURE [App::DocumentObjectGroupPython] G4_LITHIUM_IODIDE  # scripted group (container) (typed FeaturePython)
  Dunit = g/cm3
  Dvalue = 3.494
  Group = -> [Li_element005,I_element003]
  conduct = 2
  density = 1
  expand = 3
  formula = G4_LITHIUM_IODIDE
  name = G4_LITHIUM_IODIDE
  specific = 4
FEATURE [App::DocumentObjectGroupPython] Li_element006  label="Li_element : 006"  # scripted group (container) (typed FeaturePython)
  n = 2
  ref = Li_element
FEATURE [App::DocumentObjectGroupPython] O_element055  label="O_element : 029"  # scripted group (container) (typed FeaturePython)
  n = 1
  ref = O_element
FEATURE [App::DocumentObjectGroupPython] G4_LITHIUM_OXIDE  # scripted group (container) (typed FeaturePython)
  Dunit = g/cm3
  Dvalue = 2.013
  Group = -> [Li_element006,O_element055]
  conduct = 2
  density = 1
  expand = 3
  formula = G4_LITHIUM_OXIDE
  name = G4_LITHIUM_OXIDE
  specific = 4
FEATURE [App::DocumentObjectGroupPython] Li_element007  label="Li_element : 007"  # scripted group (container) (typed FeaturePython)
  n = 2
  ref = Li_element
FEATURE [App::DocumentObjectGroupPython] B_element005  label="B_element : 005"  # scripted group (container) (typed FeaturePython)
  n = 4
  ref = B_element
FEATURE [App::DocumentObjectGroupPython] O_element056  label="O_element : 7"  # scripted group (container) (typed FeaturePython)
  n = 7
  ref = O_element
FEATURE [App::DocumentObjectGroupPython] G4_LITHIUM_TETRABORATE  # scripted group (container) (typed FeaturePython)
  Dunit = g/cm3
  Dvalue = 2.44
  Group = -> [Li_element007,B_element005,O_element056]
  conduct = 2
  density = 1
  expand = 3
  formula = G4_LITHIUM_TETRABORATE
  name = G4_LITHIUM_TETRABORATE
  specific = 4
FEATURE [App::DocumentObjectGroupPython] H_element051  label="H_element : 0.105"  # scripted group (container) (typed FeaturePython)
  n = 0.105
FEATURE [App::DocumentObjectGroupPython] C_element056  label="C_element : 0.083"  # scripted group (container) (typed FeaturePython)
  n = 0.083
FEATURE [App::DocumentObjectGroupPython] N_element023  label="N_element : 0.023"  # scripted group (container) (typed FeaturePython)
  n = 0.023
FEATURE [App::DocumentObjectGroupPython] O_element057  label="O_element : 0.779"  # scripted group (container) (typed FeaturePython)
  n = 0.779
FEATURE [App::DocumentObjectGroupPython] Na_element010  label="Na_element : 0.097"  # scripted group (container) (typed FeaturePython)
  n = 0.002
FEATURE [App::DocumentObjectGroupPython] P_element006  label="P_element : 0.105"  # scripted group (container) (typed FeaturePython)
  n = 0.001
FEATURE [App::DocumentObjectGroupPython] S_element016  label="S_element : 0.017"  # scripted group (container) (typed FeaturePython)
  n = 0.002
FEATURE [App::DocumentObjectGroupPython] Cl_element014  label="Cl_element : 0.587"  # scripted group (container) (typed FeaturePython)
  n = 0.003
FEATURE [App::DocumentObjectGroupPython] K_element005  label="K_element : 0.015"  # scripted group (container) (typed FeaturePython)
  n = 0.002
FEATURE [App::DocumentObjectGroupPython] G4_LUNG_ICRP  # scripted group (container) (typed FeaturePython)
  Dunit = g/cm3
  Dvalue = 1.04
  Group = -> [H_element051,C_element056,N_element023,O_element057,Na_element010,P_element006,S_element016,Cl_element014,K_element005]
  conduct = 2
  density = 1
  expand = 3
  formula = G4_LUNG_ICRP
  name = G4_LUNG_ICRP
  specific = 4
FEATURE [App::DocumentObjectGroupPython] H_element052  label="H_element : 0.116"  # scripted group (container) (typed FeaturePython)
  n = 0.114318
FEATURE [App::DocumentObjectGroupPython] C_element057  label="C_element : 0.656"  # scripted group (container) (typed FeaturePython)
  n = 0.655824
FEATURE [App::DocumentObjectGroupPython] O_element058  label="O_element : 0.092"  # scripted group (container) (typed FeaturePython)
  n = 0.0921831
FEATURE [App::DocumentObjectGroupPython] Mg_element004  label="Mg_element : 0.135"  # scripted group (container) (typed FeaturePython)
  n = 0.134792
FEATURE [App::DocumentObjectGroupPython] Ca_element013  label="Ca_element : 0.003"  # scripted group (container) (typed FeaturePython)
  n = 0.002883
FEATURE [App::DocumentObjectGroupPython] G4_M3_WAX  # scripted group (container) (typed FeaturePython)
  Dunit = g/cm3
  Dvalue = 1.05
  Group = -> [H_element052,C_element057,O_element058,Mg_element004,Ca_element013]
  conduct = 2
  density = 1
  expand = 3
  formula = G4_M3_WAX
  name = G4_M3_WAX
  specific = 4
FEATURE [App::DocumentObjectGroupPython] Mg_element005  label="Mg_element : 1"  # scripted group (container) (typed FeaturePython)
  n = 1
  ref = Mg_element
FEATURE [App::DocumentObjectGroupPython] C_element058  label="C_element : 031"  # scripted group (container) (typed FeaturePython)
  n = 1
  ref = C_element
FEATURE [App::DocumentObjectGroupPython] O_element059  label="O_element : 030"  # scripted group (container) (typed FeaturePython)
  n = 3
  ref = O_element
FEATURE [App::DocumentObjectGroupPython] G4_MAGNESIUM_CARBONATE  # scripted group (container) (typed FeaturePython)
  Dunit = g/cm3
  Dvalue = 2.958
  Group = -> [Mg_element005,C_element058,O_element059]
  conduct = 2
  density = 1
  expand = 3
  formula = G4_MAGNESIUM_CARBONATE
  name = G4_MAGNESIUM_CARBONATE
  specific = 4
FEATURE [App::DocumentObjectGroupPython] Mg_element006  label="Mg_element : 002"  # scripted group (container) (typed FeaturePython)
  n = 1
  ref = Mg_element
FEATURE [App::DocumentObjectGroupPython] F_element013  label="F_element : 005"  # scripted group (container) (typed FeaturePython)
  n = 2
  ref = F_element
FEATURE [App::DocumentObjectGroupPython] G4_MAGNESIUM_FLUORIDE  # scripted group (container) (typed FeaturePython)
  Dunit = g/cm3
  Dvalue = 3
  Group = -> [Mg_element006,F_element013]
  conduct = 2
  density = 1
  expand = 3
  formula = G4_MAGNESIUM_FLUORIDE
  name = G4_MAGNESIUM_FLUORIDE
  specific = 4
FEATURE [App::DocumentObjectGroupPython] Mg_element007  label="Mg_element : 003"  # scripted group (container) (typed FeaturePython)
  n = 1
  ref = Mg_element
FEATURE [App::DocumentObjectGroupPython] O_element060  label="O_element : 031"  # scripted group (container) (typed FeaturePython)
  n = 1
  ref = O_element
FEATURE [App::DocumentObjectGroupPython] G4_MAGNESIUM_OXIDE  # scripted group (container) (typed FeaturePython)
  Dunit = g/cm3
  Dvalue = 3.58
  Group = -> [Mg_element007,O_element060]
  conduct = 2
  density = 1
  expand = 3
  formula = G4_MAGNESIUM_OXIDE
  name = G4_MAGNESIUM_OXIDE
  specific = 4
FEATURE [App::DocumentObjectGroupPython] Mg_element008  label="Mg_element : 004"  # scripted group (container) (typed FeaturePython)
  n = 1
  ref = Mg_element
FEATURE [App::DocumentObjectGroupPython] B_element006  label="B_element : 006"  # scripted group (container) (typed FeaturePython)
  n = 4
  ref = B_element
FEATURE [App::DocumentObjectGroupPython] O_element061  label="O_element : 032"  # scripted group (container) (typed FeaturePython)
  n = 7
  ref = O_element
FEATURE [App::DocumentObjectGroupPython] G4_MAGNESIUM_TETRABORATE  # scripted group (container) (typed FeaturePython)
  Dunit = g/cm3
  Dvalue = 2.53
  Group = -> [Mg_element008,B_element006,O_element061]
  conduct = 2
  density = 1
  expand = 3
  formula = G4_MAGNESIUM_TETRABORATE
  name = G4_MAGNESIUM_TETRABORATE
  specific = 4
FEATURE [App::DocumentObjectGroupPython] Hg_element001  label="Hg_element : 1"  # scripted group (container) (typed FeaturePython)
  n = 1
  ref = Hg_element
FEATURE [App::DocumentObjectGroupPython] I_element004  label="I_element : 2"  # scripted group (container) (typed FeaturePython)
  n = 2
  ref = I_element
FEATURE [App::DocumentObjectGroupPython] G4_MERCURIC_IODIDE  # scripted group (container) (typed FeaturePython)
  Dunit = g/cm3
  Dvalue = 6.36
  Group = -> [Hg_element001,I_element004]
  conduct = 2
  density = 1
  expand = 3
  formula = G4_MERCURIC_IODIDE
  name = G4_MERCURIC_IODIDE
  specific = 4
FEATURE [App::DocumentObjectGroupPython] C_element059  label="C_element : 032"  # scripted group (container) (typed FeaturePython)
  n = 1
  ref = C_element
FEATURE [App::DocumentObjectGroupPython] H_element053  label="H_element : 028"  # scripted group (container) (typed FeaturePython)
  n = 4
  ref = H_element
FEATURE [App::DocumentObjectGroupPython] G4_METHANE  # scripted group (container) (typed FeaturePython)
  Dunit = g/cm3
  Dvalue = 0.000667151
  Group = -> [C_element059,H_element053]
  conduct = 2
  density = 1
  expand = 3
  formula = G4_METHANE
  name = G4_METHANE
  specific = 4
FEATURE [App::DocumentObjectGroupPython] C_element060  label="C_element : 033"  # scripted group (container) (typed FeaturePython)
  n = 1
  ref = C_element
FEATURE [App::DocumentObjectGroupPython] H_element054  label="H_element : 029"  # scripted group (container) (typed FeaturePython)
  n = 4
  ref = H_element
FEATURE [App::DocumentObjectGroupPython] O_element062  label="O_element : 033"  # scripted group (container) (typed FeaturePython)
  n = 1
  ref = O_element
FEATURE [App::DocumentObjectGroupPython] G4_METHANOL  # scripted group (container) (typed FeaturePython)
  Dunit = g/cm3
  Dvalue = 0.7914
  Group = -> [C_element060,H_element054,O_element062]
  conduct = 2
  density = 1
  expand = 3
  formula = G4_METHANOL
  name = G4_METHANOL
  specific = 4
FEATURE [App::DocumentObjectGroupPython] H_element055  label="H_element : 0.134"  # scripted group (container) (typed FeaturePython)
  n = 0.13404
FEATURE [App::DocumentObjectGroupPython] C_element061  label="C_element : 0.778"  # scripted group (container) (typed FeaturePython)
  n = 0.77796
FEATURE [App::DocumentObjectGroupPython] O_element063  label="O_element : 0.035"  # scripted group (container) (typed FeaturePython)
  n = 0.03502
FEATURE [App::DocumentObjectGroupPython] Mg_element009  label="Mg_element : 0.039"  # scripted group (container) (typed FeaturePython)
  n = 0.038594
FEATURE [App::DocumentObjectGroupPython] Ti_element002  label="Ti_element : 0.014"  # scripted group (container) (typed FeaturePython)
  n = 0.014386
FEATURE [App::DocumentObjectGroupPython] G4_MIX_D_WAX  # scripted group (container) (typed FeaturePython)
  Dunit = g/cm3
  Dvalue = 0.99
  Group = -> [H_element055,C_element061,O_element063,Mg_element009,Ti_element002]
  conduct = 2
  density = 1
  expand = 3
  formula = G4_MIX_D_WAX
  name = G4_MIX_D_WAX
  specific = 4
FEATURE [App::DocumentObjectGroupPython] H_element056  label="H_element : 0.135"  # scripted group (container) (typed FeaturePython)
  n = 0.081192
FEATURE [App::DocumentObjectGroupPython] C_element062  label="C_element : 0.583"  # scripted group (container) (typed FeaturePython)
  n = 0.583442
FEATURE [App::DocumentObjectGroupPython] N_element024  label="N_element : 0.018"  # scripted group (container) (typed FeaturePython)
  n = 0.017798
FEATURE [App::DocumentObjectGroupPython] O_element064  label="O_element : 0.186"  # scripted group (container) (typed FeaturePython)
  n = 0.186381
FEATURE [App::DocumentObjectGroupPython] Mg_element010  label="Mg_element : 0.130"  # scripted group (container) (typed FeaturePython)
  n = 0.130287
FEATURE [App::DocumentObjectGroupPython] Cl_element015  label="Cl_element : 0.588"  # scripted group (container) (typed FeaturePython)
  n = 0.0009
FEATURE [App::DocumentObjectGroupPython] G4_MS20_TISSUE  # scripted group (container) (typed FeaturePython)
  Dunit = g/cm3
  Dvalue = 1
  Group = -> [H_element056,C_element062,N_element024,O_element064,Mg_element010,Cl_element015]
  conduct = 2
  density = 1
  expand = 3
  formula = G4_MS20_TISSUE
  name = G4_MS20_TISSUE
  specific = 4
FEATURE [App::DocumentObjectGroupPython] H_element057  label="H_element : 0.136"  # scripted group (container) (typed FeaturePython)
  n = 0.102
FEATURE [App::DocumentObjectGroupPython] C_element063  label="C_element : 0.143"  # scripted group (container) (typed FeaturePython)
  n = 0.143
FEATURE [App::DocumentObjectGroupPython] N_element025  label="N_element : 0.034"  # scripted group (container) (typed FeaturePython)
  n = 0.034
FEATURE [App::DocumentObjectGroupPython] O_element065  label="O_element : 0.710"  # scripted group (container) (typed FeaturePython)
  n = 0.71
FEATURE [App::DocumentObjectGroupPython] Na_element011  label="Na_element : 0.098"  # scripted group (container) (typed FeaturePython)
  n = 0.001
FEATURE [App::DocumentObjectGroupPython] P_element007  label="P_element : 0.002"  # scripted group (container) (typed FeaturePython)
  n = 0.002
FEATURE [App::DocumentObjectGroupPython] S_element017  label="S_element : 0.018"  # scripted group (container) (typed FeaturePython)
  n = 0.003
FEATURE [App::DocumentObjectGroupPython] Cl_element016  label="Cl_element : 0.589"  # scripted group (container) (typed FeaturePython)
  n = 0.001
FEATURE [App::DocumentObjectGroupPython] K_element006  label="K_element : 0.004"  # scripted group (container) (typed FeaturePython)
  n = 0.004
FEATURE [App::DocumentObjectGroupPython] G4_MUSCLE_SKELETAL_ICRP  # scripted group (container) (typed FeaturePython)
  Dunit = g/cm3
  Dvalue = 1.05
  Group = -> [H_element057,C_element063,N_element025,O_element065,Na_element011,P_element007,S_element017,Cl_element016,K_element006]
  conduct = 2
  density = 1
  expand = 3
  formula = G4_MUSCLE_SKELETAL_ICRP
  name = G4_MUSCLE_SKELETAL_ICRP
  specific = 4
FEATURE [App::DocumentObjectGroupPython] H_element058  label="H_element : 0.137"  # scripted group (container) (typed FeaturePython)
  n = 0.102102
FEATURE [App::DocumentObjectGroupPython] C_element064  label="C_element : 0.123"  # scripted group (container) (typed FeaturePython)
  n = 0.123123
FEATURE [App::DocumentObjectGroupPython] N_element026  label="N_element : 0.756"  # scripted group (container) (typed FeaturePython)
  n = 0.035035
FEATURE [App::DocumentObjectGroupPython] O_element066  label="O_element : 0.730"  # scripted group (container) (typed FeaturePython)
  n = 0.72973
FEATURE [App::DocumentObjectGroupPython] Na_element012  label="Na_element : 0.099"  # scripted group (container) (typed FeaturePython)
  n = 0.001001
FEATURE [App::DocumentObjectGroupPython] P_element008  label="P_element : 0.106"  # scripted group (container) (typed FeaturePython)
  n = 0.002002
FEATURE [App::DocumentObjectGroupPython] S_element018  label="S_element : 0.019"  # scripted group (container) (typed FeaturePython)
  n = 0.004004
FEATURE [App::DocumentObjectGroupPython] K_element007  label="K_element : 0.016"  # scripted group (container) (typed FeaturePython)
  n = 0.003003
FEATURE [App::DocumentObjectGroupPython] G4_MUSCLE_STRIATED_ICRU  # scripted group (container) (typed FeaturePython)
  Dunit = g/cm3
  Dvalue = 1.04
  Group = -> [H_element058,C_element064,N_element026,O_element066,Na_element012,P_element008,S_element018,K_element007]
  conduct = 2
  density = 1
  expand = 3
  formula = G4_MUSCLE_STRIATED_ICRU
  name = G4_MUSCLE_STRIATED_ICRU
  specific = 4
FEATURE [App::DocumentObjectGroupPython] H_element059  label="H_element : 0.098"  # scripted group (container) (typed FeaturePython)
  n = 0.0982341
FEATURE [App::DocumentObjectGroupPython] C_element065  label="C_element : 0.156"  # scripted group (container) (typed FeaturePython)
  n = 0.156214
FEATURE [App::DocumentObjectGroupPython] N_element027  label="N_element : 0.757"  # scripted group (container) (typed FeaturePython)
  n = 0.035451
FEATURE [App::DocumentObjectGroupPython] O_element067  label="O_element : 0.880"  # scripted group (container) (typed FeaturePython)
  n = 0.710101
FEATURE [App::DocumentObjectGroupPython] G4_MUSCLE_WITH_SUCROSE  # scripted group (container) (typed FeaturePython)
  Dunit = g/cm3
  Dvalue = 1.11
  Group = -> [H_element059,C_element065,N_element027,O_element067]
  conduct = 2
  density = 1
  expand = 3
  formula = G4_MUSCLE_WITH_SUCROSE
  name = G4_MUSCLE_WITH_SUCROSE
  specific = 4
FEATURE [App::DocumentObjectGroupPython] H_element060  label="H_element : 0.138"  # scripted group (container) (typed FeaturePython)
  n = 0.101969
FEATURE [App::DocumentObjectGroupPython] C_element066  label="C_element : 0.120"  # scripted group (container) (typed FeaturePython)
  n = 0.120058
FEATURE [App::DocumentObjectGroupPython] N_element028  label="N_element : 0.758"  # scripted group (container) (typed FeaturePython)
  n = 0.035451
FEATURE [App::DocumentObjectGroupPython] O_element068  label="O_element : 0.743"  # scripted group (container) (typed FeaturePython)
  n = 0.742522
FEATURE [App::DocumentObjectGroupPython] G4_MUSCLE_WITHOUT_SUCROSE  # scripted group (container) (typed FeaturePython)
  Dunit = g/cm3
  Dvalue = 1.07
  Group = -> [H_element060,C_element066,N_element028,O_element068]
  conduct = 2
  density = 1
  expand = 3
  formula = G4_MUSCLE_WITHOUT_SUCROSE
  name = G4_MUSCLE_WITHOUT_SUCROSE
  specific = 4
FEATURE [App::DocumentObjectGroupPython] C_element067  label="C_element : 10"  # scripted group (container) (typed FeaturePython)
  n = 10
  ref = C_element
FEATURE [App::DocumentObjectGroupPython] H_element061  label="H_element : 030"  # scripted group (container) (typed FeaturePython)
  n = 8
  ref = H_element
FEATURE [App::DocumentObjectGroupPython] G4_NAPHTHALENE  # scripted group (container) (typed FeaturePython)
  Dunit = g/cm3
  Dvalue = 1.145
  Group = -> [C_element067,H_element061]
  conduct = 2
  density = 1
  expand = 3
  formula = G4_NAPHTHALENE
  name = G4_NAPHTHALENE
  specific = 4
FEATURE [App::DocumentObjectGroupPython] C_element068  label="C_element : 034"  # scripted group (container) (typed FeaturePython)
  n = 6
  ref = C_element
FEATURE [App::DocumentObjectGroupPython] H_element062  label="H_element : 031"  # scripted group (container) (typed FeaturePython)
  n = 5
  ref = H_element
FEATURE [App::DocumentObjectGroupPython] N_element029  label="N_element : 012"  # scripted group (container) (typed FeaturePython)
  n = 1
  ref = N_element
FEATURE [App::DocumentObjectGroupPython] O_element069  label="O_element : 034"  # scripted group (container) (typed FeaturePython)
  n = 2
  ref = O_element
FEATURE [App::DocumentObjectGroupPython] G4_NITROBENZENE  # scripted group (container) (typed FeaturePython)
  Dunit = g/cm3
  Dvalue = 1.19867
  Group = -> [C_element068,H_element062,N_element029,O_element069]
  conduct = 2
  density = 1
  expand = 3
  formula = G4_NITROBENZENE
  name = G4_NITROBENZENE
  specific = 4
FEATURE [App::DocumentObjectGroupPython] N_element030  label="N_element : 013"  # scripted group (container) (typed FeaturePython)
  n = 2
  ref = N_element
FEATURE [App::DocumentObjectGroupPython] O_element070  label="O_element : 035"  # scripted group (container) (typed FeaturePython)
  n = 1
  ref = O_element
FEATURE [App::DocumentObjectGroupPython] G4_NITROUS_OXIDE  # scripted group (container) (typed FeaturePython)
  Dunit = g/cm3
  Dvalue = 0.00183094
  Group = -> [N_element030,O_element070]
  conduct = 2
  density = 1
  expand = 3
  formula = G4_NITROUS_OXIDE
  name = G4_NITROUS_OXIDE
  specific = 4
FEATURE [App::DocumentObjectGroupPython] H_element063  label="H_element : 0.104"  # scripted group (container) (typed FeaturePython)
  n = 0.103509
FEATURE [App::DocumentObjectGroupPython] C_element069  label="C_element : 0.648"  # scripted group (container) (typed FeaturePython)
  n = 0.648416
FEATURE [App::DocumentObjectGroupPython] N_element031  label="N_element : 0.100"  # scripted group (container) (typed FeaturePython)
  n = 0.0995361
FEATURE [App::DocumentObjectGroupPython] O_element071  label="O_element : 0.149"  # scripted group (container) (typed FeaturePython)
  n = 0.148539
FEATURE [App::DocumentObjectGroupPython] G4_NYLON_8062  label="G4_NYLON-8062"  # scripted group (container) (typed FeaturePython)
  Dunit = g/cm3
  Dvalue = 1.08
  Group = -> [H_element063,C_element069,N_element031,O_element071]
  conduct = 2
  density = 1
  expand = 3
  formula = G4_NYLON-8062
  name = G4_NYLON-8062
  specific = 4
FEATURE [App::DocumentObjectGroupPython] C_element070  label="C_element : 035"  # scripted group (container) (typed FeaturePython)
  n = 6
  ref = C_element
FEATURE [App::DocumentObjectGroupPython] H_element064  label="H_element : 11"  # scripted group (container) (typed FeaturePython)
  n = 11
  ref = H_element
FEATURE [App::DocumentObjectGroupPython] N_element032  label="N_element : 014"  # scripted group (container) (typed FeaturePython)
  n = 1
  ref = N_element
FEATURE [App::DocumentObjectGroupPython] O_element072  label="O_element : 036"  # scripted group (container) (typed FeaturePython)
  n = 1
  ref = O_element
FEATURE [App::DocumentObjectGroupPython] G4_NYLON_6_6  label="G4_NYLON-6-6"  # scripted group (container) (typed FeaturePython)
  Dunit = g/cm3
  Dvalue = 1.14
  Group = -> [C_element070,H_element064,N_element032,O_element072]
  conduct = 2
  density = 1
  expand = 3
  formula = G4_NYLON-6-6
  name = G4_NYLON-6-6
  specific = 4
FEATURE [App::DocumentObjectGroupPython] H_element065  label="H_element : 0.139"  # scripted group (container) (typed FeaturePython)
  n = 0.107062
FEATURE [App::DocumentObjectGroupPython] C_element071  label="C_element : 0.680"  # scripted group (container) (typed FeaturePython)
  n = 0.680449
FEATURE [App::DocumentObjectGroupPython] N_element033  label="N_element : 0.099"  # scripted group (container) (typed FeaturePython)
  n = 0.099189
FEATURE [App::DocumentObjectGroupPython] O_element073  label="O_element : 0.113"  # scripted group (container) (typed FeaturePython)
  n = 0.1133
FEATURE [App::DocumentObjectGroupPython] G4_NYLON_6_10  label="G4_NYLON-6-10"  # scripted group (container) (typed FeaturePython)
  Dunit = g/cm3
  Dvalue = 1.14
  Group = -> [H_element065,C_element071,N_element033,O_element073]
  conduct = 2
  density = 1
  expand = 3
  formula = G4_NYLON-6-10
  name = G4_NYLON-6-10
  specific = 4
FEATURE [App::DocumentObjectGroupPython] H_element066  label="H_element : 0.140"  # scripted group (container) (typed FeaturePython)
  n = 0.115476
FEATURE [App::DocumentObjectGroupPython] C_element072  label="C_element : 0.721"  # scripted group (container) (typed FeaturePython)
  n = 0.720818
FEATURE [App::DocumentObjectGroupPython] N_element034  label="N_element : 0.076"  # scripted group (container) (typed FeaturePython)
  n = 0.0764169
FEATURE [App::DocumentObjectGroupPython] O_element074  label="O_element : 0.087"  # scripted group (container) (typed FeaturePython)
  n = 0.0872889
FEATURE [App::DocumentObjectGroupPython] G4_NYLON_11_RILSAN  label="G4_NYLON-11_RILSAN"  # scripted group (container) (typed FeaturePython)
  Dunit = g/cm3
  Dvalue = 1.425
  Group = -> [H_element066,C_element072,N_element034,O_element074]
  conduct = 2
  density = 1
  expand = 3
  formula = G4_NYLON-11_RILSAN
  name = G4_NYLON-11_RILSAN
  specific = 4
FEATURE [App::DocumentObjectGroupPython] C_element073  label="C_element : 8"  # scripted group (container) (typed FeaturePython)
  n = 8
  ref = C_element
FEATURE [App::DocumentObjectGroupPython] H_element067  label="H_element : 18"  # scripted group (container) (typed FeaturePython)
  n = 18
  ref = H_element
FEATURE [App::DocumentObjectGroupPython] G4_OCTANE  # scripted group (container) (typed FeaturePython)
  Dunit = g/cm3
  Dvalue = 0.7026
  Group = -> [C_element073,H_element067]
  conduct = 2
  density = 1
  expand = 3
  formula = G4_OCTANE
  name = G4_OCTANE
  specific = 4
FEATURE [App::DocumentObjectGroupPython] C_element074  label="C_element : 25"  # scripted group (container) (typed FeaturePython)
  n = 25
  ref = C_element
FEATURE [App::DocumentObjectGroupPython] H_element068  label="H_element : 52"  # scripted group (container) (typed FeaturePython)
  n = 52
  ref = H_element
FEATURE [App::DocumentObjectGroupPython] G4_PARAFFIN  # scripted group (container) (typed FeaturePython)
  Dunit = g/cm3
  Dvalue = 0.93
  Group = -> [C_element074,H_element068]
  conduct = 2
  density = 1
  expand = 3
  formula = G4_PARAFFIN
  name = G4_PARAFFIN
  specific = 4
FEATURE [App::DocumentObjectGroupPython] C_element075  label="C_element : 036"  # scripted group (container) (typed FeaturePython)
  n = 5
  ref = C_element
FEATURE [App::DocumentObjectGroupPython] H_element069  label="H_element : 032"  # scripted group (container) (typed FeaturePython)
  n = 12
  ref = H_element
FEATURE [App::DocumentObjectGroupPython] G4_N_PENTANE  label="G4_N-PENTANE"  # scripted group (container) (typed FeaturePython)
  Dunit = g/cm3
  Dvalue = 0.6262
  Group = -> [C_element075,H_element069]
  conduct = 2
  density = 1
  expand = 3
  formula = G4_N-PENTANE
  name = G4_N-PENTANE
  specific = 4
FEATURE [App::DocumentObjectGroupPython] H_element070  label="H_element : 0.014"  # scripted group (container) (typed FeaturePython)
  n = 0.0141
FEATURE [App::DocumentObjectGroupPython] C_element076  label="C_element : 0.072"  # scripted group (container) (typed FeaturePython)
  n = 0.072261
FEATURE [App::DocumentObjectGroupPython] N_element035  label="N_element : 0.019"  # scripted group (container) (typed FeaturePython)
  n = 0.01932
FEATURE [App::DocumentObjectGroupPython] O_element075  label="O_element : 0.066"  # scripted group (container) (typed FeaturePython)
  n = 0.066101
FEATURE [App::DocumentObjectGroupPython] S_element019  label="S_element : 0.020"  # scripted group (container) (typed FeaturePython)
  n = 0.00189
FEATURE [App::DocumentObjectGroupPython] Br_element004  label="Br_element : 0.349"  # scripted group (container) (typed FeaturePython)
  n = 0.349103
FEATURE [App::DocumentObjectGroupPython] Ag_element001  label="Ag_element : 0.474"  # scripted group (container) (typed FeaturePython)
  n = 0.474105
FEATURE [App::DocumentObjectGroupPython] I_element005  label="I_element : 0.003"  # scripted group (container) (typed FeaturePython)
  n = 0.00312
FEATURE [App::DocumentObjectGroupPython] G4_PHOTO_EMULSION  # scripted group (container) (typed FeaturePython)
  Dunit = g/cm3
  Dvalue = 3.815
  Group = -> [H_element070,C_element076,N_element035,O_element075,S_element019,Br_element004,Ag_element001,I_element005]
  conduct = 2
  density = 1
  expand = 3
  formula = G4_PHOTO_EMULSION
  name = G4_PHOTO_EMULSION
  specific = 4
FEATURE [App::DocumentObjectGroupPython] C_element077  label="C_element : 9"  # scripted group (container) (typed FeaturePython)
  n = 9
  ref = C_element
FEATURE [App::DocumentObjectGroupPython] H_element071  label="H_element : 033"  # scripted group (container) (typed FeaturePython)
  n = 10
  ref = H_element
FEATURE [App::DocumentObjectGroupPython] G4_PLASTIC_SC_VINYLTOLUENE  # scripted group (container) (typed FeaturePython)
  Dunit = g/cm3
  Dvalue = 1.032
  Group = -> [C_element077,H_element071]
  conduct = 2
  density = 1
  expand = 3
  formula = G4_PLASTIC_SC_VINYLTOLUENE
  name = G4_PLASTIC_SC_VINYLTOLUENE
  specific = 4
FEATURE [App::DocumentObjectGroupPython] Pu_element001  label="Pu_element : 1"  # scripted group (container) (typed FeaturePython)
  n = 1
  ref = Pu_element
FEATURE [App::DocumentObjectGroupPython] O_element076  label="O_element : 037"  # scripted group (container) (typed FeaturePython)
  n = 2
  ref = O_element
FEATURE [App::DocumentObjectGroupPython] G4_PLUTONIUM_DIOXIDE  # scripted group (container) (typed FeaturePython)
  Dunit = g/cm3
  Dvalue = 11.46
  Group = -> [Pu_element001,O_element076]
  conduct = 2
  density = 1
  expand = 3
  formula = G4_PLUTONIUM_DIOXIDE
  name = G4_PLUTONIUM_DIOXIDE
  specific = 4
FEATURE [App::DocumentObjectGroupPython] C_element078  label="C_element : 037"  # scripted group (container) (typed FeaturePython)
  n = 3
  ref = C_element
FEATURE [App::DocumentObjectGroupPython] H_element072  label="H_element : 034"  # scripted group (container) (typed FeaturePython)
  n = 3
  ref = H_element
FEATURE [App::DocumentObjectGroupPython] N_element036  label="N_element : 015"  # scripted group (container) (typed FeaturePython)
  n = 1
  ref = N_element
FEATURE [App::DocumentObjectGroupPython] G4_POLYACRYLONITRILE  # scripted group (container) (typed FeaturePython)
  Dunit = g/cm3
  Dvalue = 1.17
  Group = -> [C_element078,H_element072,N_element036]
  conduct = 2
  density = 1
  expand = 3
  formula = G4_POLYACRYLONITRILE
  name = G4_POLYACRYLONITRILE
  specific = 4
FEATURE [App::DocumentObjectGroupPython] C_element079  label="C_element : 16"  # scripted group (container) (typed FeaturePython)
  n = 16
  ref = C_element
FEATURE [App::DocumentObjectGroupPython] H_element073  label="H_element : 035"  # scripted group (container) (typed FeaturePython)
  n = 14
  ref = H_element
FEATURE [App::DocumentObjectGroupPython] O_element077  label="O_element : 038"  # scripted group (container) (typed FeaturePython)
  n = 3
  ref = O_element
FEATURE [App::DocumentObjectGroupPython] G4_POLYCARBONATE  # scripted group (container) (typed FeaturePython)
  Dunit = g/cm3
  Dvalue = 1.2
  Group = -> [C_element079,H_element073,O_element077]
  conduct = 2
  density = 1
  expand = 3
  formula = G4_POLYCARBONATE
  name = G4_POLYCARBONATE
  specific = 4
FEATURE [App::DocumentObjectGroupPython] C_element080  label="C_element : 038"  # scripted group (container) (typed FeaturePython)
  n = 8
  ref = C_element
FEATURE [App::DocumentObjectGroupPython] H_element074  label="H_element : 036"  # scripted group (container) (typed FeaturePython)
  n = 7
  ref = H_element
FEATURE [App::DocumentObjectGroupPython] Cl_element017  label="Cl_element : 007"  # scripted group (container) (typed FeaturePython)
  n = 1
  ref = Cl_element
FEATURE [App::DocumentObjectGroupPython] G4_POLYCHLOROSTYRENE  # scripted group (container) (typed FeaturePython)
  Dunit = g/cm3
  Dvalue = 1.3
  Group = -> [C_element080,H_element074,Cl_element017]
  conduct = 2
  density = 1
  expand = 3
  formula = G4_POLYCHLOROSTYRENE
  name = G4_POLYCHLOROSTYRENE
  specific = 4
FEATURE [App::DocumentObjectGroupPython] C_element081  label="C_element : 039"  # scripted group (container) (typed FeaturePython)
  n = 1
  ref = C_element
FEATURE [App::DocumentObjectGroupPython] H_element075  label="H_element : 037"  # scripted group (container) (typed FeaturePython)
  n = 2
  ref = H_element
FEATURE [App::DocumentObjectGroupPython] G4_POLYETHYLENE  # scripted group (container) (typed FeaturePython)
  Dunit = g/cm3
  Dvalue = 0.94
  Group = -> [C_element081,H_element075]
  conduct = 2
  density = 1
  expand = 3
  formula = G4_POLYETHYLENE
  name = G4_POLYETHYLENE
  specific = 4
FEATURE [App::DocumentObjectGroupPython] C_element082  label="C_element : 040"  # scripted group (container) (typed FeaturePython)
  n = 10
  ref = C_element
FEATURE [App::DocumentObjectGroupPython] H_element076  label="H_element : 038"  # scripted group (container) (typed FeaturePython)
  n = 8
  ref = H_element
FEATURE [App::DocumentObjectGroupPython] O_element078  label="O_element : 039"  # scripted group (container) (typed FeaturePython)
  n = 4
  ref = O_element
FEATURE [App::DocumentObjectGroupPython] G4_MYLAR  # scripted group (container) (typed FeaturePython)
  Dunit = g/cm3
  Dvalue = 1.4
  Group = -> [C_element082,H_element076,O_element078]
  conduct = 2
  density = 1
  expand = 3
  formula = G4_MYLAR
  name = G4_MYLAR
  specific = 4
FEATURE [App::DocumentObjectGroupPython] C_element083  label="C_element : 041"  # scripted group (container) (typed FeaturePython)
  n = 5
  ref = C_element
FEATURE [App::DocumentObjectGroupPython] H_element077  label="H_element : 039"  # scripted group (container) (typed FeaturePython)
  n = 8
  ref = H_element
FEATURE [App::DocumentObjectGroupPython] O_element079  label="O_element : 040"  # scripted group (container) (typed FeaturePython)
  n = 2
  ref = O_element
FEATURE [App::DocumentObjectGroupPython] G4_PLEXIGLASS  # scripted group (container) (typed FeaturePython)
  Dunit = g/cm3
  Dvalue = 1.19
  Group = -> [C_element083,H_element077,O_element079]
  conduct = 2
  density = 1
  expand = 3
  formula = G4_PLEXIGLASS
  name = G4_PLEXIGLASS
  specific = 4
FEATURE [App::DocumentObjectGroupPython] C_element084  label="C_element : 042"  # scripted group (container) (typed FeaturePython)
  n = 1
  ref = C_element
FEATURE [App::DocumentObjectGroupPython] H_element078  label="H_element : 040"  # scripted group (container) (typed FeaturePython)
  n = 2
  ref = H_element
FEATURE [App::DocumentObjectGroupPython] O_element080  label="O_element : 041"  # scripted group (container) (typed FeaturePython)
  n = 1
  ref = O_element
FEATURE [App::DocumentObjectGroupPython] G4_POLYOXYMETHYLENE  # scripted group (container) (typed FeaturePython)
  Dunit = g/cm3
  Dvalue = 1.425
  Group = -> [C_element084,H_element078,O_element080]
  conduct = 2
  density = 1
  expand = 3
  formula = G4_POLYOXYMETHYLENE
  name = G4_POLYOXYMETHYLENE
  specific = 4
FEATURE [App::DocumentObjectGroupPython] C_element085  label="C_element : 043"  # scripted group (container) (typed FeaturePython)
  n = 2
  ref = C_element
FEATURE [App::DocumentObjectGroupPython] H_element079  label="H_element : 041"  # scripted group (container) (typed FeaturePython)
  n = 4
  ref = H_element
FEATURE [App::DocumentObjectGroupPython] G4_POLYPROPYLENE  # scripted group (container) (typed FeaturePython)
  Dunit = g/cm3
  Dvalue = 0.9
  Group = -> [C_element085,H_element079]
  conduct = 2
  density = 1
  expand = 3
  formula = G4_POLYPROPYLENE
  name = G4_POLYPROPYLENE
  specific = 4
FEATURE [App::DocumentObjectGroupPython] C_element086  label="C_element : 044"  # scripted group (container) (typed FeaturePython)
  n = 8
  ref = C_element
FEATURE [App::DocumentObjectGroupPython] H_element080  label="H_element : 042"  # scripted group (container) (typed FeaturePython)
  n = 8
  ref = H_element
FEATURE [App::DocumentObjectGroupPython] G4_POLYSTYRENE  # scripted group (container) (typed FeaturePython)
  Dunit = g/cm3
  Dvalue = 1.06
  Group = -> [C_element086,H_element080]
  conduct = 2
  density = 1
  expand = 3
  formula = G4_POLYSTYRENE
  name = G4_POLYSTYRENE
  specific = 4
FEATURE [App::DocumentObjectGroupPython] C_element087  label="C_element : 045"  # scripted group (container) (typed FeaturePython)
  n = 2
  ref = C_element
FEATURE [App::DocumentObjectGroupPython] F_element014  label="F_element : 4"  # scripted group (container) (typed FeaturePython)
  n = 4
  ref = F_element
FEATURE [App::DocumentObjectGroupPython] G4_TEFLON  # scripted group (container) (typed FeaturePython)
  Dunit = g/cm3
  Dvalue = 2.2
  Group = -> [C_element087,F_element014]
  conduct = 2
  density = 1
  expand = 3
  formula = G4_TEFLON
  name = G4_TEFLON
  specific = 4
FEATURE [App::DocumentObjectGroupPython] C_element088  label="C_element : 046"  # scripted group (container) (typed FeaturePython)
  n = 2
  ref = C_element
FEATURE [App::DocumentObjectGroupPython] F_element015  label="F_element : 006"  # scripted group (container) (typed FeaturePython)
  n = 3
  ref = F_element
FEATURE [App::DocumentObjectGroupPython] Cl_element018  label="Cl_element : 008"  # scripted group (container) (typed FeaturePython)
  n = 1
  ref = Cl_element
FEATURE [App::DocumentObjectGroupPython] G4_POLYTRIFLUOROCHLOROETHYLENE  # scripted group (container) (typed FeaturePython)
  Dunit = g/cm3
  Dvalue = 2.1
  Group = -> [C_element088,F_element015,Cl_element018]
  conduct = 2
  density = 1
  expand = 3
  formula = G4_POLYTRIFLUOROCHLOROETHYLENE
  name = G4_POLYTRIFLUOROCHLOROETHYLENE
  specific = 4
FEATURE [App::DocumentObjectGroupPython] C_element089  label="C_element : 047"  # scripted group (container) (typed FeaturePython)
  n = 4
  ref = C_element
FEATURE [App::DocumentObjectGroupPython] H_element081  label="H_element : 043"  # scripted group (container) (typed FeaturePython)
  n = 6
  ref = H_element
FEATURE [App::DocumentObjectGroupPython] O_element081  label="O_element : 042"  # scripted group (container) (typed FeaturePython)
  n = 2
  ref = O_element
FEATURE [App::DocumentObjectGroupPython] G4_POLYVINYL_ACETATE  # scripted group (container) (typed FeaturePython)
  Dunit = g/cm3
  Dvalue = 1.19
  Group = -> [C_element089,H_element081,O_element081]
  conduct = 2
  density = 1
  expand = 3
  formula = G4_POLYVINYL_ACETATE
  name = G4_POLYVINYL_ACETATE
  specific = 4
FEATURE [App::DocumentObjectGroupPython] C_element090  label="C_element : 048"  # scripted group (container) (typed FeaturePython)
  n = 2
  ref = C_element
FEATURE [App::DocumentObjectGroupPython] H_element082  label="H_element : 044"  # scripted group (container) (typed FeaturePython)
  n = 4
  ref = H_element
FEATURE [App::DocumentObjectGroupPython] O_element082  label="O_element : 043"  # scripted group (container) (typed FeaturePython)
  n = 1
  ref = O_element
FEATURE [App::DocumentObjectGroupPython] G4_POLYVINYL_ALCOHOL  # scripted group (container) (typed FeaturePython)
  Dunit = g/cm3
  Dvalue = 1.3
  Group = -> [C_element090,H_element082,O_element082]
  conduct = 2
  density = 1
  expand = 3
  formula = G4_POLYVINYL_ALCOHOL
  name = G4_POLYVINYL_ALCOHOL
  specific = 4
FEATURE [App::DocumentObjectGroupPython] C_element091  label="C_element : 049"  # scripted group (container) (typed FeaturePython)
  n = 8
  ref = C_element
FEATURE [App::DocumentObjectGroupPython] H_element083  label="H_element : 045"  # scripted group (container) (typed FeaturePython)
  n = 14
  ref = H_element
FEATURE [App::DocumentObjectGroupPython] O_element083  label="O_element : 044"  # scripted group (container) (typed FeaturePython)
  n = 2
  ref = O_element
FEATURE [App::DocumentObjectGroupPython] G4_POLYVINYL_BUTYRAL  # scripted group (container) (typed FeaturePython)
  Dunit = g/cm3
  Dvalue = 1.12
  Group = -> [C_element091,H_element083,O_element083]
  conduct = 2
  density = 1
  expand = 3
  formula = G4_POLYVINYL_BUTYRAL
  name = G4_POLYVINYL_BUTYRAL
  specific = 4
FEATURE [App::DocumentObjectGroupPython] C_element092  label="C_element : 050"  # scripted group (container) (typed FeaturePython)
  n = 2
  ref = C_element
FEATURE [App::DocumentObjectGroupPython] H_element084  label="H_element : 046"  # scripted group (container) (typed FeaturePython)
  n = 3
  ref = H_element
FEATURE [App::DocumentObjectGroupPython] Cl_element019  label="Cl_element : 009"  # scripted group (container) (typed FeaturePython)
  n = 1
  ref = Cl_element
FEATURE [App::DocumentObjectGroupPython] G4_POLYVINYL_CHLORIDE  # scripted group (container) (typed FeaturePython)
  Dunit = g/cm3
  Dvalue = 1.3
  Group = -> [C_element092,H_element084,Cl_element019]
  conduct = 2
  density = 1
  expand = 3
  formula = G4_POLYVINYL_CHLORIDE
  name = G4_POLYVINYL_CHLORIDE
  specific = 4
FEATURE [App::DocumentObjectGroupPython] C_element093  label="C_element : 051"  # scripted group (container) (typed FeaturePython)
  n = 2
  ref = C_element
FEATURE [App::DocumentObjectGroupPython] H_element085  label="H_element : 047"  # scripted group (container) (typed FeaturePython)
  n = 2
  ref = H_element
FEATURE [App::DocumentObjectGroupPython] Cl_element020  label="Cl_element : 010"  # scripted group (container) (typed FeaturePython)
  n = 2
  ref = Cl_element
FEATURE [App::DocumentObjectGroupPython] G4_POLYVINYLIDENE_CHLORIDE  # scripted group (container) (typed FeaturePython)
  Dunit = g/cm3
  Dvalue = 1.7
  Group = -> [C_element093,H_element085,Cl_element020]
  conduct = 2
  density = 1
  expand = 3
  formula = G4_POLYVINYLIDENE_CHLORIDE
  name = G4_POLYVINYLIDENE_CHLORIDE
  specific = 4
FEATURE [App::DocumentObjectGroupPython] C_element094  label="C_element : 052"  # scripted group (container) (typed FeaturePython)
  n = 2
  ref = C_element
FEATURE [App::DocumentObjectGroupPython] H_element086  label="H_element : 048"  # scripted group (container) (typed FeaturePython)
  n = 2
  ref = H_element
FEATURE [App::DocumentObjectGroupPython] F_element016  label="F_element : 007"  # scripted group (container) (typed FeaturePython)
  n = 2
  ref = F_element
FEATURE [App::DocumentObjectGroupPython] G4_POLYVINYLIDENE_FLUORIDE  # scripted group (container) (typed FeaturePython)
  Dunit = g/cm3
  Dvalue = 1.76
  Group = -> [C_element094,H_element086,F_element016]
  conduct = 2
  density = 1
  expand = 3
  formula = G4_POLYVINYLIDENE_FLUORIDE
  name = G4_POLYVINYLIDENE_FLUORIDE
  specific = 4
FEATURE [App::DocumentObjectGroupPython] C_element095  label="C_element : 053"  # scripted group (container) (typed FeaturePython)
  n = 6
  ref = C_element
FEATURE [App::DocumentObjectGroupPython] H_element087  label="H_element : 9"  # scripted group (container) (typed FeaturePython)
  n = 9
  ref = H_element
FEATURE [App::DocumentObjectGroupPython] N_element037  label="N_element : 016"  # scripted group (container) (typed FeaturePython)
  n = 1
  ref = N_element
FEATURE [App::DocumentObjectGroupPython] O_element084  label="O_element : 045"  # scripted group (container) (typed FeaturePython)
  n = 1
  ref = O_element
FEATURE [App::DocumentObjectGroupPython] G4_POLYVINYL_PYRROLIDONE  # scripted group (container) (typed FeaturePython)
  Dunit = g/cm3
  Dvalue = 1.25
  Group = -> [C_element095,H_element087,N_element037,O_element084]
  conduct = 2
  density = 1
  expand = 3
  formula = G4_POLYVINYL_PYRROLIDONE
  name = G4_POLYVINYL_PYRROLIDONE
  specific = 4
FEATURE [App::DocumentObjectGroupPython] K_element008  label="K_element : 1"  # scripted group (container) (typed FeaturePython)
  n = 1
  ref = K_element
FEATURE [App::DocumentObjectGroupPython] I_element006  label="I_element : 003"  # scripted group (container) (typed FeaturePython)
  n = 1
  ref = I_element
FEATURE [App::DocumentObjectGroupPython] G4_POTASSIUM_IODIDE  # scripted group (container) (typed FeaturePython)
  Dunit = g/cm3
  Dvalue = 3.13
  Group = -> [K_element008,I_element006]
  conduct = 2
  density = 1
  expand = 3
  formula = G4_POTASSIUM_IODIDE
  name = G4_POTASSIUM_IODIDE
  specific = 4
FEATURE [App::DocumentObjectGroupPython] K_element009  label="K_element : 2"  # scripted group (container) (typed FeaturePython)
  n = 2
  ref = K_element
FEATURE [App::DocumentObjectGroupPython] O_element085  label="O_element : 046"  # scripted group (container) (typed FeaturePython)
  n = 1
  ref = O_element
FEATURE [App::DocumentObjectGroupPython] G4_POTASSIUM_OXIDE  # scripted group (container) (typed FeaturePython)
  Dunit = g/cm3
  Dvalue = 2.32
  Group = -> [K_element009,O_element085]
  conduct = 2
  density = 1
  expand = 3
  formula = G4_POTASSIUM_OXIDE
  name = G4_POTASSIUM_OXIDE
  specific = 4
FEATURE [App::DocumentObjectGroupPython] C_element096  label="C_element : 054"  # scripted group (container) (typed FeaturePython)
  n = 3
  ref = C_element
FEATURE [App::DocumentObjectGroupPython] H_element088  label="H_element : 049"  # scripted group (container) (typed FeaturePython)
  n = 8
  ref = H_element
FEATURE [App::DocumentObjectGroupPython] G4_PROPANE  # scripted group (container) (typed FeaturePython)
  Dunit = g/cm3
  Dvalue = 0.00187939
  Group = -> [C_element096,H_element088]
  conduct = 2
  density = 1
  expand = 3
  formula = G4_PROPANE
  name = G4_PROPANE
  specific = 4
FEATURE [App::DocumentObjectGroupPython] C_element097  label="C_element : 055"  # scripted group (container) (typed FeaturePython)
  n = 3
  ref = C_element
FEATURE [App::DocumentObjectGroupPython] H_element089  label="H_element : 050"  # scripted group (container) (typed FeaturePython)
  n = 8
  ref = H_element
FEATURE [App::DocumentObjectGroupPython] G4_lPROPANE  # scripted group (container) (typed FeaturePython)
  Dunit = g/cm3
  Dvalue = 0.43
  Group = -> [C_element097,H_element089]
  conduct = 2
  density = 1
  expand = 3
  formula = G4_lPROPANE
  name = G4_lPROPANE
  specific = 4
FEATURE [App::DocumentObjectGroupPython] C_element098  label="C_element : 056"  # scripted group (container) (typed FeaturePython)
  n = 3
  ref = C_element
FEATURE [App::DocumentObjectGroupPython] H_element090  label="H_element : 051"  # scripted group (container) (typed FeaturePython)
  n = 8
  ref = H_element
FEATURE [App::DocumentObjectGroupPython] O_element086  label="O_element : 047"  # scripted group (container) (typed FeaturePython)
  n = 1
  ref = O_element
FEATURE [App::DocumentObjectGroupPython] G4_N_PROPYL_ALCOHOL  label="G4_N-PROPYL_ALCOHOL"  # scripted group (container) (typed FeaturePython)
  Dunit = g/cm3
  Dvalue = 0.8035
  Group = -> [C_element098,H_element090,O_element086]
  conduct = 2
  density = 1
  expand = 3
  formula = G4_N-PROPYL_ALCOHOL
  name = G4_N-PROPYL_ALCOHOL
  specific = 4
FEATURE [App::DocumentObjectGroupPython] C_element099  label="C_element : 057"  # scripted group (container) (typed FeaturePython)
  n = 5
  ref = C_element
FEATURE [App::DocumentObjectGroupPython] H_element091  label="H_element : 052"  # scripted group (container) (typed FeaturePython)
  n = 5
  ref = H_element
FEATURE [App::DocumentObjectGroupPython] N_element038  label="N_element : 017"  # scripted group (container) (typed FeaturePython)
  n = 1
  ref = N_element
FEATURE [App::DocumentObjectGroupPython] G4_PYRIDINE  # scripted group (container) (typed FeaturePython)
  Dunit = g/cm3
  Dvalue = 0.9819
  Group = -> [C_element099,H_element091,N_element038]
  conduct = 2
  density = 1
  expand = 3
  formula = G4_PYRIDINE
  name = G4_PYRIDINE
  specific = 4
FEATURE [App::DocumentObjectGroupPython] H_element092  label="H_element : 0.144"  # scripted group (container) (typed FeaturePython)
  n = 0.143711
FEATURE [App::DocumentObjectGroupPython] C_element100  label="C_element : 0.856"  # scripted group (container) (typed FeaturePython)
  n = 0.856289
FEATURE [App::DocumentObjectGroupPython] G4_RUBBER_BUTYL  # scripted group (container) (typed FeaturePython)
  Dunit = g/cm3
  Dvalue = 0.92
  Group = -> [H_element092,C_element100]
  conduct = 2
  density = 1
  expand = 3
  formula = G4_RUBBER_BUTYL
  name = G4_RUBBER_BUTYL
  specific = 4
FEATURE [App::DocumentObjectGroupPython] H_element093  label="H_element : 0.118"  # scripted group (container) (typed FeaturePython)
  n = 0.118371
FEATURE [App::DocumentObjectGroupPython] C_element101  label="C_element : 0.882"  # scripted group (container) (typed FeaturePython)
  n = 0.881629
FEATURE [App::DocumentObjectGroupPython] G4_RUBBER_NATURAL  # scripted group (container) (typed FeaturePython)
  Dunit = g/cm3
  Dvalue = 0.92
  Group = -> [H_element093,C_element101]
  conduct = 2
  density = 1
  expand = 3
  formula = G4_RUBBER_NATURAL
  name = G4_RUBBER_NATURAL
  specific = 4
FEATURE [App::DocumentObjectGroupPython] H_element094  label="H_element : 0.145"  # scripted group (container) (typed FeaturePython)
  n = 0.05692
FEATURE [App::DocumentObjectGroupPython] C_element102  label="C_element : 0.543"  # scripted group (container) (typed FeaturePython)
  n = 0.542646
FEATURE [App::DocumentObjectGroupPython] Cl_element021  label="Cl_element : 0.400"  # scripted group (container) (typed FeaturePython)
  n = 0.400434
FEATURE [App::DocumentObjectGroupPython] G4_RUBBER_NEOPRENE  # scripted group (container) (typed FeaturePython)
  Dunit = g/cm3
  Dvalue = 1.23
  Group = -> [H_element094,C_element102,Cl_element021]
  conduct = 2
  density = 1
  expand = 3
  formula = G4_RUBBER_NEOPRENE
  name = G4_RUBBER_NEOPRENE
  specific = 4
FEATURE [App::DocumentObjectGroupPython] Si_element006  label="Si_element : 1"  # scripted group (container) (typed FeaturePython)
  n = 1
  ref = Si_element
FEATURE [App::DocumentObjectGroupPython] O_element087  label="O_element : 048"  # scripted group (container) (typed FeaturePython)
  n = 2
  ref = O_element
FEATURE [App::DocumentObjectGroupPython] G4_SILICON_DIOXIDE  # scripted group (container) (typed FeaturePython)
  Dunit = g/cm3
  Dvalue = 2.32
  Group = -> [Si_element006,O_element087]
  conduct = 2
  density = 1
  expand = 3
  formula = G4_SILICON_DIOXIDE
  name = G4_SILICON_DIOXIDE
  specific = 4
FEATURE [App::DocumentObjectGroupPython] Ag_element002  label="Ag_element : 1"  # scripted group (container) (typed FeaturePython)
  n = 1
  ref = Ag_element
FEATURE [App::DocumentObjectGroupPython] Br_element005  label="Br_element : 003"  # scripted group (container) (typed FeaturePython)
  n = 1
  ref = Br_element
FEATURE [App::DocumentObjectGroupPython] G4_SILVER_BROMIDE  # scripted group (container) (typed FeaturePython)
  Dunit = g/cm3
  Dvalue = 6.473
  Group = -> [Ag_element002,Br_element005]
  conduct = 2
  density = 1
  expand = 3
  formula = G4_SILVER_BROMIDE
  name = G4_SILVER_BROMIDE
  specific = 4
FEATURE [App::DocumentObjectGroupPython] Ag_element003  label="Ag_element : 002"  # scripted group (container) (typed FeaturePython)
  n = 1
  ref = Ag_element
FEATURE [App::DocumentObjectGroupPython] Cl_element022  label="Cl_element : 011"  # scripted group (container) (typed FeaturePython)
  n = 1
  ref = Cl_element
FEATURE [App::DocumentObjectGroupPython] G4_SILVER_CHLORIDE  # scripted group (container) (typed FeaturePython)
  Dunit = g/cm3
  Dvalue = 5.56
  Group = -> [Ag_element003,Cl_element022]
  conduct = 2
  density = 1
  expand = 3
  formula = G4_SILVER_CHLORIDE
  name = G4_SILVER_CHLORIDE
  specific = 4
FEATURE [App::DocumentObjectGroupPython] Br_element006  label="Br_element : 0.423"  # scripted group (container) (typed FeaturePython)
  n = 0.422895
FEATURE [App::DocumentObjectGroupPython] Ag_element004  label="Ag_element : 0.574"  # scripted group (container) (typed FeaturePython)
  n = 0.573748
FEATURE [App::DocumentObjectGroupPython] I_element007  label="I_element : 0.649"  # scripted group (container) (typed FeaturePython)
  n = 0.003357
FEATURE [App::DocumentObjectGroupPython] G4_SILVER_HALIDES  # scripted group (container) (typed FeaturePython)
  Dunit = g/cm3
  Dvalue = 6.47
  Group = -> [Br_element006,Ag_element004,I_element007]
  conduct = 2
  density = 1
  expand = 3
  formula = G4_SILVER_HALIDES
  name = G4_SILVER_HALIDES
  specific = 4
FEATURE [App::DocumentObjectGroupPython] Ag_element005  label="Ag_element : 003"  # scripted group (container) (typed FeaturePython)
  n = 1
  ref = Ag_element
FEATURE [App::DocumentObjectGroupPython] I_element008  label="I_element : 004"  # scripted group (container) (typed FeaturePython)
  n = 1
  ref = I_element
FEATURE [App::DocumentObjectGroupPython] G4_SILVER_IODIDE  # scripted group (container) (typed FeaturePython)
  Dunit = g/cm3
  Dvalue = 6.01
  Group = -> [Ag_element005,I_element008]
  conduct = 2
  density = 1
  expand = 3
  formula = G4_SILVER_IODIDE
  name = G4_SILVER_IODIDE
  specific = 4
FEATURE [App::DocumentObjectGroupPython] H_element095  label="H_element : 0.100"  # scripted group (container) (typed FeaturePython)
  n = 0.1
FEATURE [App::DocumentObjectGroupPython] C_element103  label="C_element : 0.204"  # scripted group (container) (typed FeaturePython)
  n = 0.204
FEATURE [App::DocumentObjectGroupPython] N_element039  label="N_element : 0.759"  # scripted group (container) (typed FeaturePython)
  n = 0.042
FEATURE [App::DocumentObjectGroupPython] O_element088  label="O_element : 0.645"  # scripted group (container) (typed FeaturePython)
  n = 0.645
FEATURE [App::DocumentObjectGroupPython] Na_element013  label="Na_element : 0.100"  # scripted group (container) (typed FeaturePython)
  n = 0.002
FEATURE [App::DocumentObjectGroupPython] P_element009  label="P_element : 0.107"  # scripted group (container) (typed FeaturePython)
  n = 0.001
FEATURE [App::DocumentObjectGroupPython] S_element020  label="S_element : 0.021"  # scripted group (container) (typed FeaturePython)
  n = 0.002
FEATURE [App::DocumentObjectGroupPython] Cl_element023  label="Cl_element : 0.590"  # scripted group (container) (typed FeaturePython)
  n = 0.003
FEATURE [App::DocumentObjectGroupPython] K_element010  label="K_element : 0.001"  # scripted group (container) (typed FeaturePython)
  n = 0.001
FEATURE [App::DocumentObjectGroupPython] G4_SKIN_ICRP  # scripted group (container) (typed FeaturePython)
  Dunit = g/cm3
  Dvalue = 1.09
  Group = -> [H_element095,C_element103,N_element039,O_element088,Na_element013,P_element009,S_element020,Cl_element023,K_element010]
  conduct = 2
  density = 1
  expand = 3
  formula = G4_SKIN_ICRP
  name = G4_SKIN_ICRP
  specific = 4
FEATURE [App::DocumentObjectGroupPython] Na_element014  label="Na_element : 2"  # scripted group (container) (typed FeaturePython)
  n = 2
  ref = Na_element
FEATURE [App::DocumentObjectGroupPython] C_element104  label="C_element : 058"  # scripted group (container) (typed FeaturePython)
  n = 1
  ref = C_element
FEATURE [App::DocumentObjectGroupPython] O_element089  label="O_element : 049"  # scripted group (container) (typed FeaturePython)
  n = 3
  ref = O_element
FEATURE [App::DocumentObjectGroupPython] G4_SODIUM_CARBONATE  # scripted group (container) (typed FeaturePython)
  Dunit = g/cm3
  Dvalue = 2.532
  Group = -> [Na_element014,C_element104,O_element089]
  conduct = 2
  density = 1
  expand = 3
  formula = G4_SODIUM_CARBONATE
  name = G4_SODIUM_CARBONATE
  specific = 4
FEATURE [App::DocumentObjectGroupPython] Na_element015  label="Na_element : 1"  # scripted group (container) (typed FeaturePython)
  n = 1
  ref = Na_element
FEATURE [App::DocumentObjectGroupPython] I_element009  label="I_element : 005"  # scripted group (container) (typed FeaturePython)
  n = 1
  ref = I_element
FEATURE [App::DocumentObjectGroupPython] G4_SODIUM_IODIDE  # scripted group (container) (typed FeaturePython)
  Dunit = g/cm3
  Dvalue = 3.667
  Group = -> [Na_element015,I_element009]
  conduct = 2
  density = 1
  expand = 3
  formula = G4_SODIUM_IODIDE
  name = G4_SODIUM_IODIDE
  specific = 4
FEATURE [App::DocumentObjectGroupPython] Na_element016  label="Na_element : 003"  # scripted group (container) (typed FeaturePython)
  n = 2
  ref = Na_element
FEATURE [App::DocumentObjectGroupPython] O_element090  label="O_element : 050"  # scripted group (container) (typed FeaturePython)
  n = 1
  ref = O_element
FEATURE [App::DocumentObjectGroupPython] G4_SODIUM_MONOXIDE  # scripted group (container) (typed FeaturePython)
  Dunit = g/cm3
  Dvalue = 2.27
  Group = -> [Na_element016,O_element090]
  conduct = 2
  density = 1
  expand = 3
  formula = G4_SODIUM_MONOXIDE
  name = G4_SODIUM_MONOXIDE
  specific = 4
FEATURE [App::DocumentObjectGroupPython] Na_element017  label="Na_element : 004"  # scripted group (container) (typed FeaturePython)
  n = 1
  ref = Na_element
FEATURE [App::DocumentObjectGroupPython] N_element040  label="N_element : 018"  # scripted group (container) (typed FeaturePython)
  n = 1
  ref = N_element
FEATURE [App::DocumentObjectGroupPython] O_element091  label="O_element : 051"  # scripted group (container) (typed FeaturePython)
  n = 3
  ref = O_element
FEATURE [App::DocumentObjectGroupPython] G4_SODIUM_NITRATE  # scripted group (container) (typed FeaturePython)
  Dunit = g/cm3
  Dvalue = 2.261
  Group = -> [Na_element017,N_element040,O_element091]
  conduct = 2
  density = 1
  expand = 3
  formula = G4_SODIUM_NITRATE
  name = G4_SODIUM_NITRATE
  specific = 4
FEATURE [App::DocumentObjectGroupPython] C_element105  label="C_element : 059"  # scripted group (container) (typed FeaturePython)
  n = 14
  ref = C_element
FEATURE [App::DocumentObjectGroupPython] H_element096  label="H_element : 053"  # scripted group (container) (typed FeaturePython)
  n = 12
  ref = H_element
FEATURE [App::DocumentObjectGroupPython] G4_STILBENE  # scripted group (container) (typed FeaturePython)
  Dunit = g/cm3
  Dvalue = 0.9707
  Group = -> [C_element105,H_element096]
  conduct = 2
  density = 1
  expand = 3
  formula = G4_STILBENE
  name = G4_STILBENE
  specific = 4
FEATURE [App::DocumentObjectGroupPython] C_element106  label="C_element : 12"  # scripted group (container) (typed FeaturePython)
  n = 12
  ref = C_element
FEATURE [App::DocumentObjectGroupPython] H_element097  label="H_element : 22"  # scripted group (container) (typed FeaturePython)
  n = 22
  ref = H_element
FEATURE [App::DocumentObjectGroupPython] O_element092  label="O_element : 11"  # scripted group (container) (typed FeaturePython)
  n = 11
  ref = O_element
FEATURE [App::DocumentObjectGroupPython] G4_SUCROSE  # scripted group (container) (typed FeaturePython)
  Dunit = g/cm3
  Dvalue = 1.5805
  Group = -> [C_element106,H_element097,O_element092]
  conduct = 2
  density = 1
  expand = 3
  formula = G4_SUCROSE
  name = G4_SUCROSE
  specific = 4
FEATURE [App::DocumentObjectGroupPython] C_element107  label="C_element : 18"  # scripted group (container) (typed FeaturePython)
  n = 18
  ref = C_element
FEATURE [App::DocumentObjectGroupPython] H_element098  label="H_element : 054"  # scripted group (container) (typed FeaturePython)
  n = 14
  ref = H_element
FEATURE [App::DocumentObjectGroupPython] G4_TERPHENYL  # scripted group (container) (typed FeaturePython)
  Dunit = g/cm3
  Dvalue = 1.24
  Group = -> [C_element107,H_element098]
  conduct = 2
  density = 1
  expand = 3
  formula = G4_TERPHENYL
  name = G4_TERPHENYL
  specific = 4
FEATURE [App::DocumentObjectGroupPython] H_element099  label="H_element : 0.146"  # scripted group (container) (typed FeaturePython)
  n = 0.106
FEATURE [App::DocumentObjectGroupPython] C_element108  label="C_element : 0.883"  # scripted group (container) (typed FeaturePython)
  n = 0.099
FEATURE [App::DocumentObjectGroupPython] N_element041  label="N_element : 0.020"  # scripted group (container) (typed FeaturePython)
  n = 0.02
FEATURE [App::DocumentObjectGroupPython] O_element093  label="O_element : 0.766"  # scripted group (container) (typed FeaturePython)
  n = 0.766
FEATURE [App::DocumentObjectGroupPython] Na_element018  label="Na_element : 0.101"  # scripted group (container) (typed FeaturePython)
  n = 0.002
FEATURE [App::DocumentObjectGroupPython] P_element010  label="P_element : 0.108"  # scripted group (container) (typed FeaturePython)
  n = 0.001
FEATURE [App::DocumentObjectGroupPython] S_element021  label="S_element : 0.022"  # scripted group (container) (typed FeaturePython)
  n = 0.002
FEATURE [App::DocumentObjectGroupPython] Cl_element024  label="Cl_element : 0.002"  # scripted group (container) (typed FeaturePython)
  n = 0.002
FEATURE [App::DocumentObjectGroupPython] K_element011  label="K_element : 0.017"  # scripted group (container) (typed FeaturePython)
  n = 0.002
FEATURE [App::DocumentObjectGroupPython] G4_TESTIS_ICRP  # scripted group (container) (typed FeaturePython)
  Dunit = g/cm3
  Dvalue = 1.04
  Group = -> [H_element099,C_element108,N_element041,O_element093,Na_element018,P_element010,S_element021,Cl_element024,K_element011]
  conduct = 2
  density = 1
  expand = 3
  formula = G4_TESTIS_ICRP
  name = G4_TESTIS_ICRP
  specific = 4
FEATURE [App::DocumentObjectGroupPython] C_element109  label="C_element : 060"  # scripted group (container) (typed FeaturePython)
  n = 2
  ref = C_element
FEATURE [App::DocumentObjectGroupPython] Cl_element025  label="Cl_element : 012"  # scripted group (container) (typed FeaturePython)
  n = 4
  ref = Cl_element
FEATURE [App::DocumentObjectGroupPython] G4_TETRACHLOROETHYLENE  # scripted group (container) (typed FeaturePython)
  Dunit = g/cm3
  Dvalue = 1.625
  Group = -> [C_element109,Cl_element025]
  conduct = 2
  density = 1
  expand = 3
  formula = G4_TETRACHLOROETHYLENE
  name = G4_TETRACHLOROETHYLENE
  specific = 4
FEATURE [App::DocumentObjectGroupPython] Tl_element001  label="Tl_element : 1"  # scripted group (container) (typed FeaturePython)
  n = 1
  ref = Tl_element
FEATURE [App::DocumentObjectGroupPython] Cl_element026  label="Cl_element : 013"  # scripted group (container) (typed FeaturePython)
  n = 1
  ref = Cl_element
FEATURE [App::DocumentObjectGroupPython] G4_THALLIUM_CHLORIDE  # scripted group (container) (typed FeaturePython)
  Dunit = g/cm3
  Dvalue = 7.004
  Group = -> [Tl_element001,Cl_element026]
  conduct = 2
  density = 1
  expand = 3
  formula = G4_THALLIUM_CHLORIDE
  name = G4_THALLIUM_CHLORIDE
  specific = 4
FEATURE [App::DocumentObjectGroupPython] H_element100  label="H_element : 0.147"  # scripted group (container) (typed FeaturePython)
  n = 0.105
FEATURE [App::DocumentObjectGroupPython] C_element110  label="C_element : 0.256"  # scripted group (container) (typed FeaturePython)
  n = 0.256
FEATURE [App::DocumentObjectGroupPython] N_element042  label="N_element : 0.760"  # scripted group (container) (typed FeaturePython)
  n = 0.027
FEATURE [App::DocumentObjectGroupPython] O_element094  label="O_element : 0.602"  # scripted group (container) (typed FeaturePython)
  n = 0.602
FEATURE [App::DocumentObjectGroupPython] Na_element019  label="Na_element : 0.102"  # scripted group (container) (typed FeaturePython)
  n = 0.001
FEATURE [App::DocumentObjectGroupPython] P_element011  label="P_element : 0.109"  # scripted group (container) (typed FeaturePython)
  n = 0.002
FEATURE [App::DocumentObjectGroupPython] S_element022  label="S_element : 0.023"  # scripted group (container) (typed FeaturePython)
  n = 0.003
FEATURE [App::DocumentObjectGroupPython] Cl_element027  label="Cl_element : 0.591"  # scripted group (container) (typed FeaturePython)
  n = 0.002
FEATURE [App::DocumentObjectGroupPython] K_element012  label="K_element : 0.018"  # scripted group (container) (typed FeaturePython)
  n = 0.002
FEATURE [App::DocumentObjectGroupPython] G4_TISSUE_SOFT_ICRP  # scripted group (container) (typed FeaturePython)
  Dunit = g/cm3
  Dvalue = 1.03
  Group = -> [H_element100,C_element110,N_element042,O_element094,Na_element019,P_element011,S_element022,Cl_element027,K_element012]
  conduct = 2
  density = 1
  expand = 3
  formula = G4_TISSUE_SOFT_ICRP
  name = G4_TISSUE_SOFT_ICRP
  specific = 4
FEATURE [App::DocumentObjectGroupPython] H_element101  label="H_element : 0.148"  # scripted group (container) (typed FeaturePython)
  n = 0.101
FEATURE [App::DocumentObjectGroupPython] C_element111  label="C_element : 0.111"  # scripted group (container) (typed FeaturePython)
  n = 0.111
FEATURE [App::DocumentObjectGroupPython] N_element043  label="N_element : 0.026"  # scripted group (container) (typed FeaturePython)
  n = 0.026
FEATURE [App::DocumentObjectGroupPython] O_element095  label="O_element : 0.762"  # scripted group (container) (typed FeaturePython)
  n = 0.762
FEATURE [App::DocumentObjectGroupPython] G4_TISSUE_SOFT_ICRU_4  label="G4_TISSUE_SOFT_ICRU-4"  # scripted group (container) (typed FeaturePython)
  Dunit = g/cm3
  Dvalue = 1
  Group = -> [H_element101,C_element111,N_element043,O_element095]
  conduct = 2
  density = 1
  expand = 3
  formula = G4_TISSUE_SOFT_ICRU-4
  name = G4_TISSUE_SOFT_ICRU-4
  specific = 4
FEATURE [App::DocumentObjectGroupPython] H_element102  label="H_element : 0.149"  # scripted group (container) (typed FeaturePython)
  n = 0.101869
FEATURE [App::DocumentObjectGroupPython] C_element112  label="C_element : 0.456"  # scripted group (container) (typed FeaturePython)
  n = 0.456179
FEATURE [App::DocumentObjectGroupPython] N_element044  label="N_element : 0.761"  # scripted group (container) (typed FeaturePython)
  n = 0.035172
FEATURE [App::DocumentObjectGroupPython] O_element096  label="O_element : 0.407"  # scripted group (container) (typed FeaturePython)
  n = 0.40678
FEATURE [App::DocumentObjectGroupPython] G4_TISSUE_METHANE  label="G4_TISSUE-METHANE"  # scripted group (container) (typed FeaturePython)
  Dunit = g/cm3
  Dvalue = 0.00106409
  Group = -> [H_element102,C_element112,N_element044,O_element096]
  conduct = 2
  density = 1
  expand = 3
  formula = G4_TISSUE-METHANE
  name = G4_TISSUE-METHANE
  specific = 4
FEATURE [App::DocumentObjectGroupPython] H_element103  label="H_element : 0.103"  # scripted group (container) (typed FeaturePython)
  n = 0.102672
FEATURE [App::DocumentObjectGroupPython] C_element113  label="C_element : 0.569"  # scripted group (container) (typed FeaturePython)
  n = 0.56894
FEATURE [App::DocumentObjectGroupPython] N_element045  label="N_element : 0.762"  # scripted group (container) (typed FeaturePython)
  n = 0.035022
FEATURE [App::DocumentObjectGroupPython] O_element097  label="O_element : 0.293"  # scripted group (container) (typed FeaturePython)
  n = 0.293366
FEATURE [App::DocumentObjectGroupPython] G4_TISSUE_PROPANE  label="G4_TISSUE-PROPANE"  # scripted group (container) (typed FeaturePython)
  Dunit = g/cm3
  Dvalue = 0.00182628
  Group = -> [H_element103,C_element113,N_element045,O_element097]
  conduct = 2
  density = 1
  expand = 3
  formula = G4_TISSUE-PROPANE
  name = G4_TISSUE-PROPANE
  specific = 4
FEATURE [App::DocumentObjectGroupPython] Ti_element003  label="Ti_element : 1"  # scripted group (container) (typed FeaturePython)
  n = 1
  ref = Ti_element
FEATURE [App::DocumentObjectGroupPython] O_element098  label="O_element : 052"  # scripted group (container) (typed FeaturePython)
  n = 2
  ref = O_element
FEATURE [App::DocumentObjectGroupPython] G4_TITANIUM_DIOXIDE  # scripted group (container) (typed FeaturePython)
  Dunit = g/cm3
  Dvalue = 4.26
  Group = -> [Ti_element003,O_element098]
  conduct = 2
  density = 1
  expand = 3
  formula = G4_TITANIUM_DIOXIDE
  name = G4_TITANIUM_DIOXIDE
  specific = 4
FEATURE [App::DocumentObjectGroupPython] C_element114  label="C_element : 061"  # scripted group (container) (typed FeaturePython)
  n = 7
  ref = C_element
FEATURE [App::DocumentObjectGroupPython] H_element104  label="H_element : 055"  # scripted group (container) (typed FeaturePython)
  n = 8
  ref = H_element
FEATURE [App::DocumentObjectGroupPython] G4_TOLUENE  # scripted group (container) (typed FeaturePython)
  Dunit = g/cm3
  Dvalue = 0.8669
  Group = -> [C_element114,H_element104]
  conduct = 2
  density = 1
  expand = 3
  formula = G4_TOLUENE
  name = G4_TOLUENE
  specific = 4
FEATURE [App::DocumentObjectGroupPython] C_element115  label="C_element : 062"  # scripted group (container) (typed FeaturePython)
  n = 2
  ref = C_element
FEATURE [App::DocumentObjectGroupPython] H_element105  label="H_element : 056"  # scripted group (container) (typed FeaturePython)
  n = 1
  ref = H_element
FEATURE [App::DocumentObjectGroupPython] Cl_element028  label="Cl_element : 014"  # scripted group (container) (typed FeaturePython)
  n = 3
  ref = Cl_element
FEATURE [App::DocumentObjectGroupPython] G4_TRICHLOROETHYLENE  # scripted group (container) (typed FeaturePython)
  Dunit = g/cm3
  Dvalue = 1.46
  Group = -> [C_element115,H_element105,Cl_element028]
  conduct = 2
  density = 1
  expand = 3
  formula = G4_TRICHLOROETHYLENE
  name = G4_TRICHLOROETHYLENE
  specific = 4
FEATURE [App::DocumentObjectGroupPython] C_element116  label="C_element : 063"  # scripted group (container) (typed FeaturePython)
  n = 6
  ref = C_element
FEATURE [App::DocumentObjectGroupPython] H_element106  label="H_element : 15"  # scripted group (container) (typed FeaturePython)
  n = 15
  ref = H_element
FEATURE [App::DocumentObjectGroupPython] O_element099  label="O_element : 053"  # scripted group (container) (typed FeaturePython)
  n = 4
  ref = O_element
FEATURE [App::DocumentObjectGroupPython] P_element012  label="P_element : 1"  # scripted group (container) (typed FeaturePython)
  n = 1
  ref = P_element
FEATURE [App::DocumentObjectGroupPython] G4_TRIETHYL_PHOSPHATE  # scripted group (container) (typed FeaturePython)
  Dunit = g/cm3
  Dvalue = 1.07
  Group = -> [C_element116,H_element106,O_element099,P_element012]
  conduct = 2
  density = 1
  expand = 3
  formula = G4_TRIETHYL_PHOSPHATE
  name = G4_TRIETHYL_PHOSPHATE
  specific = 4
FEATURE [App::DocumentObjectGroupPython] W_element003  label="W_element : 003"  # scripted group (container) (typed FeaturePython)
  n = 1
  ref = W_element
FEATURE [App::DocumentObjectGroupPython] F_element017  label="F_element : 6"  # scripted group (container) (typed FeaturePython)
  n = 6
  ref = F_element
FEATURE [App::DocumentObjectGroupPython] G4_TUNGSTEN_HEXAFLUORIDE  # scripted group (container) (typed FeaturePython)
  Dunit = g/cm3
  Dvalue = 2.4
  Group = -> [W_element003,F_element017]
  conduct = 2
  density = 1
  expand = 3
  formula = G4_TUNGSTEN_HEXAFLUORIDE
  name = G4_TUNGSTEN_HEXAFLUORIDE
  specific = 4
FEATURE [App::DocumentObjectGroupPython] U_element001  label="U_element : 1"  # scripted group (container) (typed FeaturePython)
  n = 1
  ref = U_element
FEATURE [App::DocumentObjectGroupPython] C_element117  label="C_element : 064"  # scripted group (container) (typed FeaturePython)
  n = 2
  ref = C_element
FEATURE [App::DocumentObjectGroupPython] G4_URANIUM_DICARBIDE  # scripted group (container) (typed FeaturePython)
  Dunit = g/cm3
  Dvalue = 11.28
  Group = -> [U_element001,C_element117]
  conduct = 2
  density = 1
  expand = 3
  formula = G4_URANIUM_DICARBIDE
  name = G4_URANIUM_DICARBIDE
  specific = 4
FEATURE [App::DocumentObjectGroupPython] U_element002  label="U_element : 002"  # scripted group (container) (typed FeaturePython)
  n = 1
  ref = U_element
FEATURE [App::DocumentObjectGroupPython] C_element118  label="C_element : 065"  # scripted group (container) (typed FeaturePython)
  n = 1
  ref = C_element
FEATURE [App::DocumentObjectGroupPython] G4_URANIUM_MONOCARBIDE  # scripted group (container) (typed FeaturePython)
  Dunit = g/cm3
  Dvalue = 13.63
  Group = -> [U_element002,C_element118]
  conduct = 2
  density = 1
  expand = 3
  formula = G4_URANIUM_MONOCARBIDE
  name = G4_URANIUM_MONOCARBIDE
  specific = 4
FEATURE [App::DocumentObjectGroupPython] U_element003  label="U_element : 003"  # scripted group (container) (typed FeaturePython)
  n = 1
  ref = U_element
FEATURE [App::DocumentObjectGroupPython] O_element100  label="O_element : 054"  # scripted group (container) (typed FeaturePython)
  n = 2
  ref = O_element
FEATURE [App::DocumentObjectGroupPython] G4_URANIUM_OXIDE  # scripted group (container) (typed FeaturePython)
  Dunit = g/cm3
  Dvalue = 10.96
  Group = -> [U_element003,O_element100]
  conduct = 2
  density = 1
  expand = 3
  formula = G4_URANIUM_OXIDE
  name = G4_URANIUM_OXIDE
  specific = 4
FEATURE [App::DocumentObjectGroupPython] C_element119  label="C_element : 066"  # scripted group (container) (typed FeaturePython)
  n = 1
  ref = C_element
FEATURE [App::DocumentObjectGroupPython] H_element107  label="H_element : 057"  # scripted group (container) (typed FeaturePython)
  n = 4
  ref = H_element
FEATURE [App::DocumentObjectGroupPython] N_element046  label="N_element : 019"  # scripted group (container) (typed FeaturePython)
  n = 2
  ref = N_element
FEATURE [App::DocumentObjectGroupPython] O_element101  label="O_element : 055"  # scripted group (container) (typed FeaturePython)
  n = 1
  ref = O_element
FEATURE [App::DocumentObjectGroupPython] G4_UREA  # scripted group (container) (typed FeaturePython)
  Dunit = g/cm3
  Dvalue = 1.323
  Group = -> [C_element119,H_element107,N_element046,O_element101]
  conduct = 2
  density = 1
  expand = 3
  formula = G4_UREA
  name = G4_UREA
  specific = 4
FEATURE [App::DocumentObjectGroupPython] C_element120  label="C_element : 067"  # scripted group (container) (typed FeaturePython)
  n = 5
  ref = C_element
FEATURE [App::DocumentObjectGroupPython] H_element108  label="H_element : 058"  # scripted group (container) (typed FeaturePython)
  n = 11
  ref = H_element
FEATURE [App::DocumentObjectGroupPython] N_element047  label="N_element : 020"  # scripted group (container) (typed FeaturePython)
  n = 1
  ref = N_element
FEATURE [App::DocumentObjectGroupPython] O_element102  label="O_element : 056"  # scripted group (container) (typed FeaturePython)
  n = 2
  ref = O_element
FEATURE [App::DocumentObjectGroupPython] G4_VALINE  # scripted group (container) (typed FeaturePython)
  Dunit = g/cm3
  Dvalue = 1.23
  Group = -> [C_element120,H_element108,N_element047,O_element102]
  conduct = 2
  density = 1
  expand = 3
  formula = G4_VALINE
  name = G4_VALINE
  specific = 4
FEATURE [App::DocumentObjectGroupPython] H_element109  label="H_element : 0.009"  # scripted group (container) (typed FeaturePython)
  n = 0.009417
FEATURE [App::DocumentObjectGroupPython] C_element121  label="C_element : 0.281"  # scripted group (container) (typed FeaturePython)
  n = 0.280555
FEATURE [App::DocumentObjectGroupPython] F_element018  label="F_element : 0.710"  # scripted group (container) (typed FeaturePython)
  n = 0.710028
FEATURE [App::DocumentObjectGroupPython] G4_VITON  # scripted group (container) (typed FeaturePython)
  Dunit = g/cm3
  Dvalue = 1.8
  Group = -> [H_element109,C_element121,F_element018]
  conduct = 2
  density = 1
  expand = 3
  formula = G4_VITON
  name = G4_VITON
  specific = 4
FEATURE [App::DocumentObjectGroupPython] H_element110  label="H_element : 059"  # scripted group (container) (typed FeaturePython)
  n = 2
  ref = H_element
FEATURE [App::DocumentObjectGroupPython] O_element103  label="O_element : 057"  # scripted group (container) (typed FeaturePython)
  n = 1
  ref = O_element
FEATURE [App::DocumentObjectGroupPython] G4_WATER  # scripted group (container) (typed FeaturePython)
  Dunit = g/cm3
  Dvalue = 1
  Group = -> [H_element110,O_element103]
  conduct = 2
  density = 1
  expand = 3
  formula = G4_WATER
  name = G4_WATER
  specific = 4
FEATURE [App::DocumentObjectGroupPython] H_element111  label="H_element : 060"  # scripted group (container) (typed FeaturePython)
  n = 2
  ref = H_element
FEATURE [App::DocumentObjectGroupPython] O_element104  label="O_element : 058"  # scripted group (container) (typed FeaturePython)
  n = 1
  ref = O_element
FEATURE [App::DocumentObjectGroupPython] G4_WATER_VAPOR  # scripted group (container) (typed FeaturePython)
  Dunit = g/cm3
  Dvalue = 0.000756182
  Group = -> [H_element111,O_element104]
  conduct = 2
  density = 1
  expand = 3
  formula = G4_WATER_VAPOR
  name = G4_WATER_VAPOR
  specific = 4
FEATURE [App::DocumentObjectGroupPython] C_element122  label="C_element : 068"  # scripted group (container) (typed FeaturePython)
  n = 8
  ref = C_element
FEATURE [App::DocumentObjectGroupPython] H_element112  label="H_element : 061"  # scripted group (container) (typed FeaturePython)
  n = 10
  ref = H_element
FEATURE [App::DocumentObjectGroupPython] G4_XYLENE  # scripted group (container) (typed FeaturePython)
  Dunit = g/cm3
  Dvalue = 0.87
  Group = -> [C_element122,H_element112]
  conduct = 2
  density = 1
  expand = 3
  formula = G4_XYLENE
  name = G4_XYLENE
  specific = 4
FEATURE [App::DocumentObjectGroupPython] C_element123  label="C_element : 069"  # scripted group (container) (typed FeaturePython)
  n = 1
  ref = C_element
FEATURE [App::DocumentObjectGroupPython] G4_GRAPHITE  # scripted group (container) (typed FeaturePython)
  Dunit = g/cm3
  Dvalue = 2.21
  Group = -> [C_element123]
  conduct = 2
  density = 1
  expand = 3
  formula = G4_GRAPHITE
  name = G4_GRAPHITE
  specific = 4
FEATURE [App::DocumentObjectGroupPython] NIST  # scripted group (container) (typed FeaturePython)
  Group = -> [G4_A_150_TISSUE,G4_ACETONE,G4_ACETYLENE,G4_ADENINE,G4_ADIPOSE_TISSUE_ICRP,G4_AIR,G4_ALANINE,G4_ALUMINUM_OXIDE,G4_AMBER,G4_AMMONIA,G4_ANILINE,G4_ANTHRACENE,G4_B_100_BONE,G4_BAKELITE,G4_BARIUM_FLUORIDE,G4_BARIUM_SULFATE,G4_BENZENE,G4_BERYLLIUM_OXIDE,G4_BGO,G4_BLOOD_ICRP,G4_BONE_COMPACT_ICRU,G4_BONE_CORTICAL_ICRP,G4_BORON_CARBIDE,G4_BORON_OXIDE,G4_BRAIN_ICRP,G4_BUTANE,G4_N_BUTYL_ALCOHOL,G4_C_552,+152 more]
FEATURE [App::DocumentObjectGroupPython] H_element113  label="H_element : 062"  # scripted group (container) (typed FeaturePython)
  n = 1
  ref = H_element
FEATURE [App::DocumentObjectGroupPython] G4_H  # scripted group (container) (typed FeaturePython)
  Dunit = g/cm3
  Dvalue = 8.3748e-05
  Group = -> [H_element113]
  conduct = 2
  density = 1
  expand = 3
  formula = H
  name = G4_H
  specific = 4
FEATURE [App::DocumentObjectGroupPython] He_element001  label="He_element : 1"  # scripted group (container) (typed FeaturePython)
  n = 1
  ref = He_element
FEATURE [App::DocumentObjectGroupPython] G4_He  # scripted group (container) (typed FeaturePython)
  Dunit = g/cm3
  Dvalue = 0.000166322
  Group = -> [He_element001]
  conduct = 2
  density = 1
  expand = 3
  formula = He
  name = G4_He
  specific = 4
FEATURE [App::DocumentObjectGroupPython] Li_element008  label="Li_element : 008"  # scripted group (container) (typed FeaturePython)
  n = 1
  ref = Li_element
FEATURE [App::DocumentObjectGroupPython] G4_Li  # scripted group (container) (typed FeaturePython)
  Dunit = g/cm3
  Dvalue = 0.534
  Group = -> [Li_element008]
  conduct = 2
  density = 1
  expand = 3
  formula = Li
  name = G4_Li
  specific = 4
FEATURE [App::DocumentObjectGroupPython] Be_element002  label="Be_element : 002"  # scripted group (container) (typed FeaturePython)
  n = 1
  ref = Be_element
FEATURE [App::DocumentObjectGroupPython] G4_Be  # scripted group (container) (typed FeaturePython)
  Dunit = g/cm3
  Dvalue = 1.848
  Group = -> [Be_element002]
  conduct = 2
  density = 1
  expand = 3
  formula = Be
  name = G4_Be
  specific = 4
FEATURE [App::DocumentObjectGroupPython] B_element007  label="B_element : 007"  # scripted group (container) (typed FeaturePython)
  n = 1
  ref = B_element
FEATURE [App::DocumentObjectGroupPython] G4_B  # scripted group (container) (typed FeaturePython)
  Dunit = g/cm3
  Dvalue = 2.37
  Group = -> [B_element007]
  conduct = 2
  density = 1
  expand = 3
  formula = B
  name = G4_B
  specific = 4
FEATURE [App::DocumentObjectGroupPython] C_element124  label="C_element : 070"  # scripted group (container) (typed FeaturePython)
  n = 1
  ref = C_element
FEATURE [App::DocumentObjectGroupPython] G4_C  # scripted group (container) (typed FeaturePython)
  Dunit = g/cm3
  Dvalue = 2
  Group = -> [C_element124]
  conduct = 2
  density = 1
  expand = 3
  formula = C
  name = G4_C
  specific = 4
FEATURE [App::DocumentObjectGroupPython] N_element048  label="N_element : 021"  # scripted group (container) (typed FeaturePython)
  n = 1
  ref = N_element
FEATURE [App::DocumentObjectGroupPython] G4_N  # scripted group (container) (typed FeaturePython)
  Dunit = g/cm3
  Dvalue = 0.0011652
  Group = -> [N_element048]
  conduct = 2
  density = 1
  expand = 3
  formula = N
  name = G4_N
  specific = 4
FEATURE [App::DocumentObjectGroupPython] O_element105  label="O_element : 059"  # scripted group (container) (typed FeaturePython)
  n = 1
  ref = O_element
FEATURE [App::DocumentObjectGroupPython] G4_O  # scripted group (container) (typed FeaturePython)
  Dunit = g/cm3
  Dvalue = 0.00133151
  Group = -> [O_element105]
  conduct = 2
  density = 1
  expand = 3
  formula = O
  name = G4_O
  specific = 4
FEATURE [App::DocumentObjectGroupPython] F_element019  label="F_element : 008"  # scripted group (container) (typed FeaturePython)
  n = 1
  ref = F_element
FEATURE [App::DocumentObjectGroupPython] G4_F  # scripted group (container) (typed FeaturePython)
  Dunit = g/cm3
  Dvalue = 0.00158029
  Group = -> [F_element019]
  conduct = 2
  density = 1
  expand = 3
  formula = F
  name = G4_F
  specific = 4
FEATURE [App::DocumentObjectGroupPython] Ne_element001  label="Ne_element : 1"  # scripted group (container) (typed FeaturePython)
  n = 1
  ref = Ne_element
FEATURE [App::DocumentObjectGroupPython] G4_Ne  # scripted group (container) (typed FeaturePython)
  Dunit = g/cm3
  Dvalue = 0.000838505
  Group = -> [Ne_element001]
  conduct = 2
  density = 1
  expand = 3
  formula = Ne
  name = G4_Ne
  specific = 4
FEATURE [App::DocumentObjectGroupPython] Na_element020  label="Na_element : 005"  # scripted group (container) (typed FeaturePython)
  n = 1
  ref = Na_element
FEATURE [App::DocumentObjectGroupPython] G4_Na  # scripted group (container) (typed FeaturePython)
  Dunit = g/cm3
  Dvalue = 0.971
  Group = -> [Na_element020]
  conduct = 2
  density = 1
  expand = 3
  formula = Na
  name = G4_Na
  specific = 4
FEATURE [App::DocumentObjectGroupPython] Mg_element011  label="Mg_element : 005"  # scripted group (container) (typed FeaturePython)
  n = 1
  ref = Mg_element
FEATURE [App::DocumentObjectGroupPython] G4_Mg  # scripted group (container) (typed FeaturePython)
  Dunit = g/cm3
  Dvalue = 1.74
  Group = -> [Mg_element011]
  conduct = 2
  density = 1
  expand = 3
  formula = Mg
  name = G4_Mg
  specific = 4
FEATURE [App::DocumentObjectGroupPython] Al_element004  label="Al_element : 1"  # scripted group (container) (typed FeaturePython)
  n = 1
  ref = Al_element
FEATURE [App::DocumentObjectGroupPython] G4_Al  # scripted group (container) (typed FeaturePython)
  Dunit = g/cm3
  Dvalue = 2.699
  Group = -> [Al_element004]
  conduct = 2
  density = 1
  expand = 3
  formula = Al
  name = G4_Al
  specific = 4
FEATURE [App::DocumentObjectGroupPython] Si_element007  label="Si_element : 002"  # scripted group (container) (typed FeaturePython)
  n = 1
  ref = Si_element
FEATURE [App::DocumentObjectGroupPython] G4_Si  # scripted group (container) (typed FeaturePython)
  Dunit = g/cm3
  Dvalue = 2.33
  Group = -> [Si_element007]
  conduct = 2
  density = 1
  expand = 3
  formula = Si
  name = G4_Si
  specific = 4
FEATURE [App::DocumentObjectGroupPython] P_element013  label="P_element : 002"  # scripted group (container) (typed FeaturePython)
  n = 1
  ref = P_element
FEATURE [App::DocumentObjectGroupPython] G4_P  # scripted group (container) (typed FeaturePython)
  Dunit = g/cm3
  Dvalue = 2.2
  Group = -> [P_element013]
  conduct = 2
  density = 1
  expand = 3
  formula = P
  name = G4_P
  specific = 4
FEATURE [App::DocumentObjectGroupPython] S_element023  label="S_element : 007"  # scripted group (container) (typed FeaturePython)
  n = 1
  ref = S_element
FEATURE [App::DocumentObjectGroupPython] G4_S  # scripted group (container) (typed FeaturePython)
  Dunit = g/cm3
  Dvalue = 2
  Group = -> [S_element023]
  conduct = 2
  density = 1
  expand = 3
  formula = S
  name = G4_S
  specific = 4
FEATURE [App::DocumentObjectGroupPython] Cl_element029  label="Cl_element : 015"  # scripted group (container) (typed FeaturePython)
  n = 1
  ref = Cl_element
FEATURE [App::DocumentObjectGroupPython] G4_Cl  # scripted group (container) (typed FeaturePython)
  Dunit = g/cm3
  Dvalue = 0.00299473
  Group = -> [Cl_element029]
  conduct = 2
  density = 1
  expand = 3
  formula = Cl
  name = G4_Cl
  specific = 4
FEATURE [App::DocumentObjectGroupPython] Ar_element002  label="Ar_element : 1"  # scripted group (container) (typed FeaturePython)
  n = 1
  ref = Ar_element
FEATURE [App::DocumentObjectGroupPython] G4_Ar  # scripted group (container) (typed FeaturePython)
  Dunit = g/cm3
  Dvalue = 0.00166201
  Group = -> [Ar_element002]
  conduct = 2
  density = 1
  expand = 3
  formula = Ar
  name = G4_Ar
  specific = 4
FEATURE [App::DocumentObjectGroupPython] K_element013  label="K_element : 003"  # scripted group (container) (typed FeaturePython)
  n = 1
  ref = K_element
FEATURE [App::DocumentObjectGroupPython] G4_K  # scripted group (container) (typed FeaturePython)
  Dunit = g/cm3
  Dvalue = 0.862
  Group = -> [K_element013]
  conduct = 2
  density = 1
  expand = 3
  formula = K
  name = G4_K
  specific = 4
FEATURE [App::DocumentObjectGroupPython] Ca_element014  label="Ca_element : 007"  # scripted group (container) (typed FeaturePython)
  n = 1
  ref = Ca_element
FEATURE [App::DocumentObjectGroupPython] G4_Ca  # scripted group (container) (typed FeaturePython)
  Dunit = g/cm3
  Dvalue = 1.55
  Group = -> [Ca_element014]
  conduct = 2
  density = 1
  expand = 3
  formula = Ca
  name = G4_Ca
  specific = 4
FEATURE [App::DocumentObjectGroupPython] Sc_element001  label="Sc_element : 1"  # scripted group (container) (typed FeaturePython)
  n = 1
  ref = Sc_element
FEATURE [App::DocumentObjectGroupPython] G4_Sc  # scripted group (container) (typed FeaturePython)
  Dunit = g/cm3
  Dvalue = 2.989
  Group = -> [Sc_element001]
  conduct = 2
  density = 1
  expand = 3
  formula = Sc
  name = G4_Sc
  specific = 4
FEATURE [App::DocumentObjectGroupPython] Ti_element004  label="Ti_element : 002"  # scripted group (container) (typed FeaturePython)
  n = 1
  ref = Ti_element
FEATURE [App::DocumentObjectGroupPython] G4_Ti  # scripted group (container) (typed FeaturePython)
  Dunit = g/cm3
  Dvalue = 4.54
  Group = -> [Ti_element004]
  conduct = 2
  density = 1
  expand = 3
  formula = Ti
  name = G4_Ti
  specific = 4
FEATURE [App::DocumentObjectGroupPython] V_element001  label="V_element : 1"  # scripted group (container) (typed FeaturePython)
  n = 1
  ref = V_element
FEATURE [App::DocumentObjectGroupPython] G4_V  # scripted group (container) (typed FeaturePython)
  Dunit = g/cm3
  Dvalue = 6.11
  Group = -> [V_element001]
  conduct = 2
  density = 1
  expand = 3
  formula = V
  name = G4_V
  specific = 4
FEATURE [App::DocumentObjectGroupPython] Cr_element001  label="Cr_element : 1"  # scripted group (container) (typed FeaturePython)
  n = 1
  ref = Cr_element
FEATURE [App::DocumentObjectGroupPython] G4_Cr  # scripted group (container) (typed FeaturePython)
  Dunit = g/cm3
  Dvalue = 7.18
  Group = -> [Cr_element001]
  conduct = 2
  density = 1
  expand = 3
  formula = Cr
  name = G4_Cr
  specific = 4
FEATURE [App::DocumentObjectGroupPython] Mn_element001  label="Mn_element : 1"  # scripted group (container) (typed FeaturePython)
  n = 1
  ref = Mn_element
FEATURE [App::DocumentObjectGroupPython] G4_Mn  # scripted group (container) (typed FeaturePython)
  Dunit = g/cm3
  Dvalue = 7.44
  Group = -> [Mn_element001]
  conduct = 2
  density = 1
  expand = 3
  formula = Mn
  name = G4_Mn
  specific = 4
FEATURE [App::DocumentObjectGroupPython] Fe_element007  label="Fe_element : 004"  # scripted group (container) (typed FeaturePython)
  n = 1
  ref = Fe_element
FEATURE [App::DocumentObjectGroupPython] G4_Fe  # scripted group (container) (typed FeaturePython)
  Dunit = g/cm3
  Dvalue = 7.874
  Group = -> [Fe_element007]
  conduct = 2
  density = 1
  expand = 3
  formula = Fe
  name = G4_Fe
  specific = 4
FEATURE [App::DocumentObjectGroupPython] Co_element001  label="Co_element : 1"  # scripted group (container) (typed FeaturePython)
  n = 1
  ref = Co_element
FEATURE [App::DocumentObjectGroupPython] G4_Co  # scripted group (container) (typed FeaturePython)
  Dunit = g/cm3
  Dvalue = 8.9
  Group = -> [Co_element001]
  conduct = 2
  density = 1
  expand = 3
  formula = Co
  name = G4_Co
  specific = 4
FEATURE [App::DocumentObjectGroupPython] Ni_element001  label="Ni_element : 1"  # scripted group (container) (typed FeaturePython)
  n = 1
  ref = Ni_element
FEATURE [App::DocumentObjectGroupPython] G4_Ni  # scripted group (container) (typed FeaturePython)
  Dunit = g/cm3
  Dvalue = 8.902
  Group = -> [Ni_element001]
  conduct = 2
  density = 1
  expand = 3
  formula = Ni
  name = G4_Ni
  specific = 4
FEATURE [App::DocumentObjectGroupPython] Cu_element001  label="Cu_element : 1"  # scripted group (container) (typed FeaturePython)
  n = 1
  ref = Cu_element
FEATURE [App::DocumentObjectGroupPython] G4_Cu  # scripted group (container) (typed FeaturePython)
  Dunit = g/cm3
  Dvalue = 8.96
  Group = -> [Cu_element001]
  conduct = 2
  density = 1
  expand = 3
  formula = Cu
  name = G4_Cu
  specific = 4
FEATURE [App::DocumentObjectGroupPython] Zn_element001  label="Zn_element : 1"  # scripted group (container) (typed FeaturePython)
  n = 1
  ref = Zn_element
FEATURE [App::DocumentObjectGroupPython] G4_Zn  # scripted group (container) (typed FeaturePython)
  Dunit = g/cm3
  Dvalue = 7.133
  Group = -> [Zn_element001]
  conduct = 2
  density = 1
  expand = 3
  formula = Zn
  name = G4_Zn
  specific = 4
FEATURE [App::DocumentObjectGroupPython] Ga_element002  label="Ga_element : 002"  # scripted group (container) (typed FeaturePython)
  n = 1
  ref = Ga_element
FEATURE [App::DocumentObjectGroupPython] G4_Ga  # scripted group (container) (typed FeaturePython)
  Dunit = g/cm3
  Dvalue = 5.904
  Group = -> [Ga_element002]
  conduct = 2
  density = 1
  expand = 3
  formula = Ga
  name = G4_Ga
  specific = 4
FEATURE [App::DocumentObjectGroupPython] Ge_element002  label="Ge_element : 1"  # scripted group (container) (typed FeaturePython)
  n = 1
  ref = Ge_element
FEATURE [App::DocumentObjectGroupPython] G4_Ge  # scripted group (container) (typed FeaturePython)
  Dunit = g/cm3
  Dvalue = 5.323
  Group = -> [Ge_element002]
  conduct = 2
  density = 1
  expand = 3
  formula = Ge
  name = G4_Ge
  specific = 4
FEATURE [App::DocumentObjectGroupPython] As_element003  label="As_element : 002"  # scripted group (container) (typed FeaturePython)
  n = 1
  ref = As_element
FEATURE [App::DocumentObjectGroupPython] G4_As  # scripted group (container) (typed FeaturePython)
  Dunit = g/cm3
  Dvalue = 5.73
  Group = -> [As_element003]
  conduct = 2
  density = 1
  expand = 3
  formula = As
  name = G4_As
  specific = 4
FEATURE [App::DocumentObjectGroupPython] Se_element001  label="Se_element : 1"  # scripted group (container) (typed FeaturePython)
  n = 1
  ref = Se_element
FEATURE [App::DocumentObjectGroupPython] G4_Se  # scripted group (container) (typed FeaturePython)
  Dunit = g/cm3
  Dvalue = 4.5
  Group = -> [Se_element001]
  conduct = 2
  density = 1
  expand = 3
  formula = Se
  name = G4_Se
  specific = 4
FEATURE [App::DocumentObjectGroupPython] Br_element007  label="Br_element : 004"  # scripted group (container) (typed FeaturePython)
  n = 1
  ref = Br_element
FEATURE [App::DocumentObjectGroupPython] G4_Br  # scripted group (container) (typed FeaturePython)
  Dunit = g/cm3
  Dvalue = 0.0070721
  Group = -> [Br_element007]
  conduct = 2
  density = 1
  expand = 3
  formula = Br
  name = G4_Br
  specific = 4
FEATURE [App::DocumentObjectGroupPython] Kr_element001  label="Kr_element : 1"  # scripted group (container) (typed FeaturePython)
  n = 1
  ref = Kr_element
FEATURE [App::DocumentObjectGroupPython] G4_Kr  # scripted group (container) (typed FeaturePython)
  Dunit = g/cm3
  Dvalue = 0.00347832
  Group = -> [Kr_element001]
  conduct = 2
  density = 1
  expand = 3
  formula = Kr
  name = G4_Kr
  specific = 4
FEATURE [App::DocumentObjectGroupPython] Rb_element001  label="Rb_element : 1"  # scripted group (container) (typed FeaturePython)
  n = 1
  ref = Rb_element
FEATURE [App::DocumentObjectGroupPython] G4_Rb  # scripted group (container) (typed FeaturePython)
  Dunit = g/cm3
  Dvalue = 1.532
  Group = -> [Rb_element001]
  conduct = 2
  density = 1
  expand = 3
  formula = Rb
  name = G4_Rb
  specific = 4
FEATURE [App::DocumentObjectGroupPython] Sr_element001  label="Sr_element : 1"  # scripted group (container) (typed FeaturePython)
  n = 1
  ref = Sr_element
FEATURE [App::DocumentObjectGroupPython] G4_Sr  # scripted group (container) (typed FeaturePython)
  Dunit = g/cm3
  Dvalue = 2.54
  Group = -> [Sr_element001]
  conduct = 2
  density = 1
  expand = 3
  formula = Sr
  name = G4_Sr
  specific = 4
FEATURE [App::DocumentObjectGroupPython] Y_element001  label="Y_element : 1"  # scripted group (container) (typed FeaturePython)
  n = 1
  ref = Y_element
FEATURE [App::DocumentObjectGroupPython] G4_Y  # scripted group (container) (typed FeaturePython)
  Dunit = g/cm3
  Dvalue = 4.469
  Group = -> [Y_element001]
  conduct = 2
  density = 1
  expand = 3
  formula = Y
  name = G4_Y
  specific = 4
FEATURE [App::DocumentObjectGroupPython] Zr_element001  label="Zr_element : 1"  # scripted group (container) (typed FeaturePython)
  n = 1
  ref = Zr_element
FEATURE [App::DocumentObjectGroupPython] G4_Zr  # scripted group (container) (typed FeaturePython)
  Dunit = g/cm3
  Dvalue = 6.506
  Group = -> [Zr_element001]
  conduct = 2
  density = 1
  expand = 3
  formula = Zr
  name = G4_Zr
  specific = 4
FEATURE [App::DocumentObjectGroupPython] Nb_element001  label="Nb_element : 1"  # scripted group (container) (typed FeaturePython)
  n = 1
  ref = Nb_element
FEATURE [App::DocumentObjectGroupPython] G4_Nb  # scripted group (container) (typed FeaturePython)
  Dunit = g/cm3
  Dvalue = 8.57
  Group = -> [Nb_element001]
  conduct = 2
  density = 1
  expand = 3
  formula = Nb
  name = G4_Nb
  specific = 4
FEATURE [App::DocumentObjectGroupPython] Mo_element001  label="Mo_element : 1"  # scripted group (container) (typed FeaturePython)
  n = 1
  ref = Mo_element
FEATURE [App::DocumentObjectGroupPython] G4_Mo  # scripted group (container) (typed FeaturePython)
  Dunit = g/cm3
  Dvalue = 10.22
  Group = -> [Mo_element001]
  conduct = 2
  density = 1
  expand = 3
  formula = Mo
  name = G4_Mo
  specific = 4
FEATURE [App::DocumentObjectGroupPython] Tc_element001  label="Tc_element : 1"  # scripted group (container) (typed FeaturePython)
  n = 1
  ref = Tc_element
FEATURE [App::DocumentObjectGroupPython] G4_Tc  # scripted group (container) (typed FeaturePython)
  Dunit = g/cm3
  Dvalue = 11.5
  Group = -> [Tc_element001]
  conduct = 2
  density = 1
  expand = 3
  formula = Tc
  name = G4_Tc
  specific = 4
FEATURE [App::DocumentObjectGroupPython] Ru_element001  label="Ru_element : 1"  # scripted group (container) (typed FeaturePython)
  n = 1
  ref = Ru_element
FEATURE [App::DocumentObjectGroupPython] G4_Ru  # scripted group (container) (typed FeaturePython)
  Dunit = g/cm3
  Dvalue = 12.41
  Group = -> [Ru_element001]
  conduct = 2
  density = 1
  expand = 3
  formula = Ru
  name = G4_Ru
  specific = 4
FEATURE [App::DocumentObjectGroupPython] Rh_element001  label="Rh_element : 1"  # scripted group (container) (typed FeaturePython)
  n = 1
  ref = Rh_element
FEATURE [App::DocumentObjectGroupPython] G4_Rh  # scripted group (container) (typed FeaturePython)
  Dunit = g/cm3
  Dvalue = 12.41
  Group = -> [Rh_element001]
  conduct = 2
  density = 1
  expand = 3
  formula = Rh
  name = G4_Rh
  specific = 4
FEATURE [App::DocumentObjectGroupPython] Pd_element001  label="Pd_element : 1"  # scripted group (container) (typed FeaturePython)
  n = 1
  ref = Pd_element
FEATURE [App::DocumentObjectGroupPython] G4_Pd  # scripted group (container) (typed FeaturePython)
  Dunit = g/cm3
  Dvalue = 12.02
  Group = -> [Pd_element001]
  conduct = 2
  density = 1
  expand = 3
  formula = Pd
  name = G4_Pd
  specific = 4
FEATURE [App::DocumentObjectGroupPython] Ag_element006  label="Ag_element : 004"  # scripted group (container) (typed FeaturePython)
  n = 1
  ref = Ag_element
FEATURE [App::DocumentObjectGroupPython] G4_Ag  # scripted group (container) (typed FeaturePython)
  Dunit = g/cm3
  Dvalue = 10.5
  Group = -> [Ag_element006]
  conduct = 2
  density = 1
  expand = 3
  formula = Ag
  name = G4_Ag
  specific = 4
FEATURE [App::DocumentObjectGroupPython] Cd_element003  label="Cd_element : 003"  # scripted group (container) (typed FeaturePython)
  n = 1
  ref = Cd_element
FEATURE [App::DocumentObjectGroupPython] G4_Cd  # scripted group (container) (typed FeaturePython)
  Dunit = g/cm3
  Dvalue = 8.65
  Group = -> [Cd_element003]
  conduct = 2
  density = 1
  expand = 3
  formula = Cd
  name = G4_Cd
  specific = 4
FEATURE [App::DocumentObjectGroupPython] In_element001  label="In_element : 1"  # scripted group (container) (typed FeaturePython)
  n = 1
  ref = In_element
FEATURE [App::DocumentObjectGroupPython] G4_In  # scripted group (container) (typed FeaturePython)
  Dunit = g/cm3
  Dvalue = 7.31
  Group = -> [In_element001]
  conduct = 2
  density = 1
  expand = 3
  formula = In
  name = G4_In
  specific = 4
FEATURE [App::DocumentObjectGroupPython] Sn_element001  label="Sn_element : 1"  # scripted group (container) (typed FeaturePython)
  n = 1
  ref = Sn_element
FEATURE [App::DocumentObjectGroupPython] G4_Sn  # scripted group (container) (typed FeaturePython)
  Dunit = g/cm3
  Dvalue = 7.31
  Group = -> [Sn_element001]
  conduct = 2
  density = 1
  expand = 3
  formula = Sn
  name = G4_Sn
  specific = 4
FEATURE [App::DocumentObjectGroupPython] Sb_element001  label="Sb_element : 1"  # scripted group (container) (typed FeaturePython)
  n = 1
  ref = Sb_element
FEATURE [App::DocumentObjectGroupPython] G4_Sb  # scripted group (container) (typed FeaturePython)
  Dunit = g/cm3
  Dvalue = 6.691
  Group = -> [Sb_element001]
  conduct = 2
  density = 1
  expand = 3
  formula = Sb
  name = G4_Sb
  specific = 4
FEATURE [App::DocumentObjectGroupPython] Te_element002  label="Te_element : 002"  # scripted group (container) (typed FeaturePython)
  n = 1
  ref = Te_element
FEATURE [App::DocumentObjectGroupPython] G4_Te  # scripted group (container) (typed FeaturePython)
  Dunit = g/cm3
  Dvalue = 6.24
  Group = -> [Te_element002]
  conduct = 2
  density = 1
  expand = 3
  formula = Te
  name = G4_Te
  specific = 4
FEATURE [App::DocumentObjectGroupPython] I_element010  label="I_element : 006"  # scripted group (container) (typed FeaturePython)
  n = 1
  ref = I_element
FEATURE [App::DocumentObjectGroupPython] G4_I  # scripted group (container) (typed FeaturePython)
  Dunit = g/cm3
  Dvalue = 4.93
  Group = -> [I_element010]
  conduct = 2
  density = 1
  expand = 3
  formula = I
  name = G4_I
  specific = 4
FEATURE [App::DocumentObjectGroupPython] Xe_element001  label="Xe_element : 1"  # scripted group (container) (typed FeaturePython)
  n = 1
  ref = Xe_element
FEATURE [App::DocumentObjectGroupPython] G4_Xe  # scripted group (container) (typed FeaturePython)
  Dunit = g/cm3
  Dvalue = 0.00548536
  Group = -> [Xe_element001]
  conduct = 2
  density = 1
  expand = 3
  formula = Xe
  name = G4_Xe
  specific = 4
FEATURE [App::DocumentObjectGroupPython] Cs_element003  label="Cs_element : 003"  # scripted group (container) (typed FeaturePython)
  n = 1
  ref = Cs_element
FEATURE [App::DocumentObjectGroupPython] G4_Cs  # scripted group (container) (typed FeaturePython)
  Dunit = g/cm3
  Dvalue = 1.873
  Group = -> [Cs_element003]
  conduct = 2
  density = 1
  expand = 3
  formula = Cs
  name = G4_Cs
  specific = 4
FEATURE [App::DocumentObjectGroupPython] Ba_element003  label="Ba_element : 003"  # scripted group (container) (typed FeaturePython)
  n = 1
  ref = Ba_element
FEATURE [App::DocumentObjectGroupPython] G4_Ba  # scripted group (container) (typed FeaturePython)
  Dunit = g/cm3
  Dvalue = 3.5
  Group = -> [Ba_element003]
  conduct = 2
  density = 1
  expand = 3
  formula = Ba
  name = G4_Ba
  specific = 4
FEATURE [App::DocumentObjectGroupPython] La_element003  label="La_element : 003"  # scripted group (container) (typed FeaturePython)
  n = 1
  ref = La_element
FEATURE [App::DocumentObjectGroupPython] G4_La  # scripted group (container) (typed FeaturePython)
  Dunit = g/cm3
  Dvalue = 6.154
  Group = -> [La_element003]
  conduct = 2
  density = 1
  expand = 3
  formula = La
  name = G4_La
  specific = 4
FEATURE [App::DocumentObjectGroupPython] Ce_element002  label="Ce_element : 1"  # scripted group (container) (typed FeaturePython)
  n = 1
  ref = Ce_element
FEATURE [App::DocumentObjectGroupPython] G4_Ce  # scripted group (container) (typed FeaturePython)
  Dunit = g/cm3
  Dvalue = 6.657
  Group = -> [Ce_element002]
  conduct = 2
  density = 1
  expand = 3
  formula = Ce
  name = G4_Ce
  specific = 4
FEATURE [App::DocumentObjectGroupPython] Pr_element001  label="Pr_element : 1"  # scripted group (container) (typed FeaturePython)
  n = 1
  ref = Pr_element
FEATURE [App::DocumentObjectGroupPython] G4_Pr  # scripted group (container) (typed FeaturePython)
  Dunit = g/cm3
  Dvalue = 6.71
  Group = -> [Pr_element001]
  conduct = 2
  density = 1
  expand = 3
  formula = Pr
  name = G4_Pr
  specific = 4
FEATURE [App::DocumentObjectGroupPython] Nd_element001  label="Nd_element : 1"  # scripted group (container) (typed FeaturePython)
  n = 1
  ref = Nd_element
FEATURE [App::DocumentObjectGroupPython] G4_Nd  # scripted group (container) (typed FeaturePython)
  Dunit = g/cm3
  Dvalue = 6.9
  Group = -> [Nd_element001]
  conduct = 2
  density = 1
  expand = 3
  formula = Nd
  name = G4_Nd
  specific = 4
FEATURE [App::DocumentObjectGroupPython] Pm_element001  label="Pm_element : 1"  # scripted group (container) (typed FeaturePython)
  n = 1
  ref = Pm_element
FEATURE [App::DocumentObjectGroupPython] G4_Pm  # scripted group (container) (typed FeaturePython)
  Dunit = g/cm3
  Dvalue = 7.22
  Group = -> [Pm_element001]
  conduct = 2
  density = 1
  expand = 3
  formula = Pm
  name = G4_Pm
  specific = 4
FEATURE [App::DocumentObjectGroupPython] Sm_element001  label="Sm_element : 1"  # scripted group (container) (typed FeaturePython)
  n = 1
  ref = Sm_element
FEATURE [App::DocumentObjectGroupPython] G4_Sm  # scripted group (container) (typed FeaturePython)
  Dunit = g/cm3
  Dvalue = 7.46
  Group = -> [Sm_element001]
  conduct = 2
  density = 1
  expand = 3
  formula = Sm
  name = G4_Sm
  specific = 4
FEATURE [App::DocumentObjectGroupPython] Eu_element001  label="Eu_element : 1"  # scripted group (container) (typed FeaturePython)
  n = 1
  ref = Eu_element
FEATURE [App::DocumentObjectGroupPython] G4_Eu  # scripted group (container) (typed FeaturePython)
  Dunit = g/cm3
  Dvalue = 5.243
  Group = -> [Eu_element001]
  conduct = 2
  density = 1
  expand = 3
  formula = Eu
  name = G4_Eu
  specific = 4
FEATURE [App::DocumentObjectGroupPython] Gd_element002  label="Gd_element : 1"  # scripted group (container) (typed FeaturePython)
  n = 1
  ref = Gd_element
FEATURE [App::DocumentObjectGroupPython] G4_Gd  # scripted group (container) (typed FeaturePython)
  Dunit = g/cm3
  Dvalue = 7.9004
  Group = -> [Gd_element002]
  conduct = 2
  density = 1
  expand = 3
  formula = Gd
  name = G4_Gd
  specific = 4
FEATURE [App::DocumentObjectGroupPython] Tb_element001  label="Tb_element : 1"  # scripted group (container) (typed FeaturePython)
  n = 1
  ref = Tb_element
FEATURE [App::DocumentObjectGroupPython] G4_Tb  # scripted group (container) (typed FeaturePython)
  Dunit = g/cm3
  Dvalue = 8.229
  Group = -> [Tb_element001]
  conduct = 2
  density = 1
  expand = 3
  formula = Tb
  name = G4_Tb
  specific = 4
FEATURE [App::DocumentObjectGroupPython] Dy_element001  label="Dy_element : 1"  # scripted group (container) (typed FeaturePython)
  n = 1
  ref = Dy_element
FEATURE [App::DocumentObjectGroupPython] G4_Dy  # scripted group (container) (typed FeaturePython)
  Dunit = g/cm3
  Dvalue = 8.55
  Group = -> [Dy_element001]
  conduct = 2
  density = 1
  expand = 3
  formula = Dy
  name = G4_Dy
  specific = 4
FEATURE [App::DocumentObjectGroupPython] Ho_element001  label="Ho_element : 1"  # scripted group (container) (typed FeaturePython)
  n = 1
  ref = Ho_element
FEATURE [App::DocumentObjectGroupPython] G4_Ho  # scripted group (container) (typed FeaturePython)
  Dunit = g/cm3
  Dvalue = 8.795
  Group = -> [Ho_element001]
  conduct = 2
  density = 1
  expand = 3
  formula = Ho
  name = G4_Ho
  specific = 4
FEATURE [App::DocumentObjectGroupPython] Er_element001  label="Er_element : 1"  # scripted group (container) (typed FeaturePython)
  n = 1
  ref = Er_element
FEATURE [App::DocumentObjectGroupPython] G4_Er  # scripted group (container) (typed FeaturePython)
  Dunit = g/cm3
  Dvalue = 9.066
  Group = -> [Er_element001]
  conduct = 2
  density = 1
  expand = 3
  formula = Er
  name = G4_Er
  specific = 4
FEATURE [App::DocumentObjectGroupPython] Tm_element001  label="Tm_element : 1"  # scripted group (container) (typed FeaturePython)
  n = 1
  ref = Tm_element
FEATURE [App::DocumentObjectGroupPython] G4_Tm  # scripted group (container) (typed FeaturePython)
  Dunit = g/cm3
  Dvalue = 9.321
  Group = -> [Tm_element001]
  conduct = 2
  density = 1
  expand = 3
  formula = Tm
  name = G4_Tm
  specific = 4
FEATURE [App::DocumentObjectGroupPython] Yb_element001  label="Yb_element : 1"  # scripted group (container) (typed FeaturePython)
  n = 1
  ref = Yb_element
FEATURE [App::DocumentObjectGroupPython] G4_Yb  # scripted group (container) (typed FeaturePython)
  Dunit = g/cm3
  Dvalue = 6.73
  Group = -> [Yb_element001]
  conduct = 2
  density = 1
  expand = 3
  formula = Yb
  name = G4_Yb
  specific = 4
FEATURE [App::DocumentObjectGroupPython] Lu_element001  label="Lu_element : 1"  # scripted group (container) (typed FeaturePython)
  n = 1
  ref = Lu_element
FEATURE [App::DocumentObjectGroupPython] G4_Lu  # scripted group (container) (typed FeaturePython)
  Dunit = g/cm3
  Dvalue = 9.84
  Group = -> [Lu_element001]
  conduct = 2
  density = 1
  expand = 3
  formula = Lu
  name = G4_Lu
  specific = 4
FEATURE [App::DocumentObjectGroupPython] Hf_element001  label="Hf_element : 1"  # scripted group (container) (typed FeaturePython)
  n = 1
  ref = Hf_element
FEATURE [App::DocumentObjectGroupPython] G4_Hf  # scripted group (container) (typed FeaturePython)
  Dunit = g/cm3
  Dvalue = 13.31
  Group = -> [Hf_element001]
  conduct = 2
  density = 1
  expand = 3
  formula = Hf
  name = G4_Hf
  specific = 4
FEATURE [App::DocumentObjectGroupPython] Ta_element001  label="Ta_element : 1"  # scripted group (container) (typed FeaturePython)
  n = 1
  ref = Ta_element
FEATURE [App::DocumentObjectGroupPython] G4_Ta  # scripted group (container) (typed FeaturePython)
  Dunit = g/cm3
  Dvalue = 16.654
  Group = -> [Ta_element001]
  conduct = 2
  density = 1
  expand = 3
  formula = Ta
  name = G4_Ta
  specific = 4
FEATURE [App::DocumentObjectGroupPython] W_element004  label="W_element : 004"  # scripted group (container) (typed FeaturePython)
  n = 1
  ref = W_element
FEATURE [App::DocumentObjectGroupPython] G4_W  # scripted group (container) (typed FeaturePython)
  Dunit = g/cm3
  Dvalue = 19.3
  Group = -> [W_element004]
  conduct = 2
  density = 1
  expand = 3
  formula = W
  name = G4_W
  specific = 4
FEATURE [App::DocumentObjectGroupPython] Re_element001  label="Re_element : 1"  # scripted group (container) (typed FeaturePython)
  n = 1
  ref = Re_element
FEATURE [App::DocumentObjectGroupPython] G4_Re  # scripted group (container) (typed FeaturePython)
  Dunit = g/cm3
  Dvalue = 21.02
  Group = -> [Re_element001]
  conduct = 2
  density = 1
  expand = 3
  formula = Re
  name = G4_Re
  specific = 4
FEATURE [App::DocumentObjectGroupPython] Os_element001  label="Os_element : 1"  # scripted group (container) (typed FeaturePython)
  n = 1
  ref = Os_element
FEATURE [App::DocumentObjectGroupPython] G4_Os  # scripted group (container) (typed FeaturePython)
  Dunit = g/cm3
  Dvalue = 22.57
  Group = -> [Os_element001]
  conduct = 2
  density = 1
  expand = 3
  formula = Os
  name = G4_Os
  specific = 4
FEATURE [App::DocumentObjectGroupPython] Ir_element001  label="Ir_element : 1"  # scripted group (container) (typed FeaturePython)
  n = 1
  ref = Ir_element
FEATURE [App::DocumentObjectGroupPython] G4_Ir  # scripted group (container) (typed FeaturePython)
  Dunit = g/cm3
  Dvalue = 22.42
  Group = -> [Ir_element001]
  conduct = 2
  density = 1
  expand = 3
  formula = Ir
  name = G4_Ir
  specific = 4
FEATURE [App::DocumentObjectGroupPython] Pt_element001  label="Pt_element : 1"  # scripted group (container) (typed FeaturePython)
  n = 1
  ref = Pt_element
FEATURE [App::DocumentObjectGroupPython] G4_Pt  # scripted group (container) (typed FeaturePython)
  Dunit = g/cm3
  Dvalue = 21.45
  Group = -> [Pt_element001]
  conduct = 2
  density = 1
  expand = 3
  formula = Pt
  name = G4_Pt
  specific = 4
FEATURE [App::DocumentObjectGroupPython] Au_element001  label="Au_element : 1"  # scripted group (container) (typed FeaturePython)
  n = 1
  ref = Au_element
FEATURE [App::DocumentObjectGroupPython] G4_Au  # scripted group (container) (typed FeaturePython)
  Dunit = g/cm3
  Dvalue = 19.32
  Group = -> [Au_element001]
  conduct = 2
  density = 1
  expand = 3
  formula = Au
  name = G4_Au
  specific = 4
FEATURE [App::DocumentObjectGroupPython] Hg_element002  label="Hg_element : 002"  # scripted group (container) (typed FeaturePython)
  n = 1
  ref = Hg_element
FEATURE [App::DocumentObjectGroupPython] G4_Hg  # scripted group (container) (typed FeaturePython)
  Dunit = g/cm3
  Dvalue = 13.546
  Group = -> [Hg_element002]
  conduct = 2
  density = 1
  expand = 3
  formula = Hg
  name = G4_Hg
  specific = 4
FEATURE [App::DocumentObjectGroupPython] Tl_element002  label="Tl_element : 002"  # scripted group (container) (typed FeaturePython)
  n = 1
  ref = Tl_element
FEATURE [App::DocumentObjectGroupPython] G4_Tl  # scripted group (container) (typed FeaturePython)
  Dunit = g/cm3
  Dvalue = 11.72
  Group = -> [Tl_element002]
  conduct = 2
  density = 1
  expand = 3
  formula = Tl
  name = G4_Tl
  specific = 4
FEATURE [App::DocumentObjectGroupPython] Pb_element003  label="Pb_element : 1"  # scripted group (container) (typed FeaturePython)
  n = 1
  ref = Pb_element
FEATURE [App::DocumentObjectGroupPython] G4_Pb  # scripted group (container) (typed FeaturePython)
  Dunit = g/cm3
  Dvalue = 11.35
  Group = -> [Pb_element003]
  conduct = 2
  density = 1
  expand = 3
  formula = Pb
  name = G4_Pb
  specific = 4
FEATURE [App::DocumentObjectGroupPython] Bi_element002  label="Bi_element : 1"  # scripted group (container) (typed FeaturePython)
  n = 1
  ref = Bi_element
FEATURE [App::DocumentObjectGroupPython] G4_Bi  # scripted group (container) (typed FeaturePython)
  Dunit = g/cm3
  Dvalue = 9.747
  Group = -> [Bi_element002]
  conduct = 2
  density = 1
  expand = 3
  formula = Bi
  name = G4_Bi
  specific = 4
FEATURE [App::DocumentObjectGroupPython] Po_element001  label="Po_element : 1"  # scripted group (container) (typed FeaturePython)
  n = 1
  ref = Po_element
FEATURE [App::DocumentObjectGroupPython] G4_Po  # scripted group (container) (typed FeaturePython)
  Dunit = g/cm3
  Dvalue = 9.32
  Group = -> [Po_element001]
  conduct = 2
  density = 1
  expand = 3
  formula = Po
  name = G4_Po
  specific = 4
FEATURE [App::DocumentObjectGroupPython] At_element001  label="At_element : 1"  # scripted group (container) (typed FeaturePython)
  n = 1
  ref = At_element
FEATURE [App::DocumentObjectGroupPython] G4_At  # scripted group (container) (typed FeaturePython)
  Dunit = g/cm3
  Dvalue = 9.32
  Group = -> [At_element001]
  conduct = 2
  density = 1
  expand = 3
  formula = At
  name = G4_At
  specific = 4
FEATURE [App::DocumentObjectGroupPython] Rn_element001  label="Rn_element : 1"  # scripted group (container) (typed FeaturePython)
  n = 1
  ref = Rn_element
FEATURE [App::DocumentObjectGroupPython] G4_Rn  # scripted group (container) (typed FeaturePython)
  Dunit = g/cm3
  Dvalue = 0.00900662
  Group = -> [Rn_element001]
  conduct = 2
  density = 1
  expand = 3
  formula = Rn
  name = G4_Rn
  specific = 4
FEATURE [App::DocumentObjectGroupPython] Fr_element001  label="Fr_element : 1"  # scripted group (container) (typed FeaturePython)
  n = 1
  ref = Fr_element
FEATURE [App::DocumentObjectGroupPython] G4_Fr  # scripted group (container) (typed FeaturePython)
  Dunit = g/cm3
  Dvalue = 1
  Group = -> [Fr_element001]
  conduct = 2
  density = 1
  expand = 3
  formula = Fr
  name = G4_Fr
  specific = 4
FEATURE [App::DocumentObjectGroupPython] Ra_element001  label="Ra_element : 1"  # scripted group (container) (typed FeaturePython)
  n = 1
  ref = Ra_element
FEATURE [App::DocumentObjectGroupPython] G4_Ra  # scripted group (container) (typed FeaturePython)
  Dunit = g/cm3
  Dvalue = 5
  Group = -> [Ra_element001]
  conduct = 2
  density = 1
  expand = 3
  formula = Ra
  name = G4_Ra
  specific = 4
FEATURE [App::DocumentObjectGroupPython] Ac_element001  label="Ac_element : 1"  # scripted group (container) (typed FeaturePython)
  n = 1
  ref = Ac_element
FEATURE [App::DocumentObjectGroupPython] G4_Ac  # scripted group (container) (typed FeaturePython)
  Dunit = g/cm3
  Dvalue = 10.07
  Group = -> [Ac_element001]
  conduct = 2
  density = 1
  expand = 3
  formula = Ac
  name = G4_Ac
  specific = 4
FEATURE [App::DocumentObjectGroupPython] Th_element001  label="Th_element : 1"  # scripted group (container) (typed FeaturePython)
  n = 1
  ref = Th_element
FEATURE [App::DocumentObjectGroupPython] G4_Th  # scripted group (container) (typed FeaturePython)
  Dunit = g/cm3
  Dvalue = 11.72
  Group = -> [Th_element001]
  conduct = 2
  density = 1
  expand = 3
  formula = Th
  name = G4_Th
  specific = 4
FEATURE [App::DocumentObjectGroupPython] Pa_element001  label="Pa_element : 1"  # scripted group (container) (typed FeaturePython)
  n = 1
  ref = Pa_element
FEATURE [App::DocumentObjectGroupPython] G4_Pa  # scripted group (container) (typed FeaturePython)
  Dunit = g/cm3
  Dvalue = 15.37
  Group = -> [Pa_element001]
  conduct = 2
  density = 1
  expand = 3
  formula = Pa
  name = G4_Pa
  specific = 4
FEATURE [App::DocumentObjectGroupPython] U_element004  label="U_element : 004"  # scripted group (container) (typed FeaturePython)
  n = 1
  ref = U_element
FEATURE [App::DocumentObjectGroupPython] G4_U  # scripted group (container) (typed FeaturePython)
  Dunit = g/cm3
  Dvalue = 18.95
  Group = -> [U_element004]
  conduct = 2
  density = 1
  expand = 3
  formula = U
  name = G4_U
  specific = 4
FEATURE [App::DocumentObjectGroupPython] Np_element001  label="Np_element : 1"  # scripted group (container) (typed FeaturePython)
  n = 1
  ref = Np_element
FEATURE [App::DocumentObjectGroupPython] G4_Np  # scripted group (container) (typed FeaturePython)
  Dunit = g/cm3
  Dvalue = 20.25
  Group = -> [Np_element001]
  conduct = 2
  density = 1
  expand = 3
  formula = Np
  name = G4_Np
  specific = 4
FEATURE [App::DocumentObjectGroupPython] Pu_element002  label="Pu_element : 002"  # scripted group (container) (typed FeaturePython)
  n = 1
  ref = Pu_element
FEATURE [App::DocumentObjectGroupPython] G4_Pu  # scripted group (container) (typed FeaturePython)
  Dunit = g/cm3
  Dvalue = 19.84
  Group = -> [Pu_element002]
  conduct = 2
  density = 1
  expand = 3
  formula = Pu
  name = G4_Pu
  specific = 4
FEATURE [App::DocumentObjectGroupPython] Am_element001  label="Am_element : 1"  # scripted group (container) (typed FeaturePython)
  n = 1
  ref = Am_element
FEATURE [App::DocumentObjectGroupPython] G4_Am  # scripted group (container) (typed FeaturePython)
  Dunit = g/cm3
  Dvalue = 13.67
  Group = -> [Am_element001]
  conduct = 2
  density = 1
  expand = 3
  formula = Am
  name = G4_Am
  specific = 4
FEATURE [App::DocumentObjectGroupPython] Cm_element001  label="Cm_element : 1"  # scripted group (container) (typed FeaturePython)
  n = 1
  ref = Cm_element
FEATURE [App::DocumentObjectGroupPython] G4_Cm  # scripted group (container) (typed FeaturePython)
  Dunit = g/cm3
  Dvalue = 13.51
  Group = -> [Cm_element001]
  conduct = 2
  density = 1
  expand = 3
  formula = Cm
  name = G4_Cm
  specific = 4
FEATURE [App::DocumentObjectGroupPython] Bk_element001  label="Bk_element : 1"  # scripted group (container) (typed FeaturePython)
  n = 1
  ref = Bk_element
FEATURE [App::DocumentObjectGroupPython] G4_Bk  # scripted group (container) (typed FeaturePython)
  Dunit = g/cm3
  Dvalue = 14
  Group = -> [Bk_element001]
  conduct = 2
  density = 1
  expand = 3
  formula = Bk
  name = G4_Bk
  specific = 4
FEATURE [App::DocumentObjectGroupPython] Cf_element001  label="Cf_element : 1"  # scripted group (container) (typed FeaturePython)
  n = 1
  ref = Cf_element
FEATURE [App::DocumentObjectGroupPython] G4_Cf  # scripted group (container) (typed FeaturePython)
  Dunit = g/cm3
  Dvalue = 10
  Group = -> [Cf_element001]
  conduct = 2
  density = 1
  expand = 3
  formula = Cf
  name = G4_Cf
  specific = 4
FEATURE [App::DocumentObjectGroupPython] Element  # scripted group (container) (typed FeaturePython)
  Group = -> [G4_H,G4_He,G4_Li,G4_Be,G4_B,G4_C,G4_N,G4_O,G4_F,G4_Ne,G4_Na,G4_Mg,G4_Al,G4_Si,G4_P,G4_S,G4_Cl,G4_Ar,G4_K,G4_Ca,G4_Sc,G4_Ti,G4_V,G4_Cr,G4_Mn,G4_Fe,G4_Co,G4_Ni,G4_Cu,G4_Zn,G4_Ga,G4_Ge,G4_As,G4_Se,G4_Br,G4_Kr,G4_Rb,G4_Sr,G4_Y,G4_Zr,G4_Nb,G4_Mo,G4_Tc,G4_Ru,G4_Rh,G4_Pd,G4_Ag,G4_Cd,G4_In,G4_Sn,G4_Sb,G4_Te,G4_I,G4_Xe,G4_Cs,G4_Ba,G4_La,G4_Ce,G4_Pr,G4_Nd,G4_Pm,G4_Sm,G4_Eu,G4_Gd,G4_Tb,G4_Dy,G4_Ho,G4_Er,+30 more]
FEATURE [App::DocumentObjectGroupPython] H_element114  label="H_element : 063"  # scripted group (container) (typed FeaturePython)
  n = 2
  ref = H_element
FEATURE [App::DocumentObjectGroupPython] G4_lH2  # scripted group (container) (typed FeaturePython)
  Dunit = g/cm3
  Dvalue = 0.0708
  Group = -> [H_element114]
  conduct = 2
  density = 1
  expand = 3
  formula = G4_lH2
  name = G4_lH2
  specific = 4
FEATURE [App::DocumentObjectGroupPython] N_element049  label="N_element : 022"  # scripted group (container) (typed FeaturePython)
  n = 2
  ref = N_element
FEATURE [App::DocumentObjectGroupPython] G4_lN2  # scripted group (container) (typed FeaturePython)
  Dunit = g/cm3
  Dvalue = 0.807
  Group = -> [N_element049]
  conduct = 2
  density = 1
  expand = 3
  formula = G4_lN2
  name = G4_lN2
  specific = 4
FEATURE [App::DocumentObjectGroupPython] O_element106  label="O_element : 060"  # scripted group (container) (typed FeaturePython)
  n = 2
  ref = O_element
FEATURE [App::DocumentObjectGroupPython] G4_lO2  # scripted group (container) (typed FeaturePython)
  Dunit = g/cm3
  Dvalue = 1.141
  Group = -> [O_element106]
  conduct = 2
  density = 1
  expand = 3
  formula = G4_lO2
  name = G4_lO2
  specific = 4
FEATURE [App::DocumentObjectGroupPython] Ar  label="Ar : 1"  # scripted group (container) (typed FeaturePython)
  n = 1
  ref = Ar
FEATURE [App::DocumentObjectGroupPython] G4_lAr  # scripted group (container) (typed FeaturePython)
  Dunit = g/cm3
  Dvalue = 1.396
  Group = -> [Ar]
  conduct = 2
  density = 1
  expand = 3
  formula = G4_lAr
  name = G4_lAr
  specific = 4
FEATURE [App::DocumentObjectGroupPython] Br  label="Br : 1"  # scripted group (container) (typed FeaturePython)
  n = 1
  ref = Br
FEATURE [App::DocumentObjectGroupPython] G4_lBr  # scripted group (container) (typed FeaturePython)
  Dunit = g/cm3
  Dvalue = 3.1028
  Group = -> [Br]
  conduct = 2
  density = 1
  expand = 3
  formula = G4_lBr
  name = G4_lBr
  specific = 4
FEATURE [App::DocumentObjectGroupPython] Kr  label="Kr : 1"  # scripted group (container) (typed FeaturePython)
  n = 1
  ref = Kr
FEATURE [App::DocumentObjectGroupPython] G4_lKr  # scripted group (container) (typed FeaturePython)
  Dunit = g/cm3
  Dvalue = 2.418
  Group = -> [Kr]
  conduct = 2
  density = 1
  expand = 3
  formula = G4_lKr
  name = G4_lKr
  specific = 4
FEATURE [App::DocumentObjectGroupPython] Xe  label="Xe : 1"  # scripted group (container) (typed FeaturePython)
  n = 1
  ref = Xe
FEATURE [App::DocumentObjectGroupPython] G4_lXe  # scripted group (container) (typed FeaturePython)
  Dunit = g/cm3
  Dvalue = 2.953
  Group = -> [Xe]
  conduct = 2
  density = 1
  expand = 3
  formula = G4_lXe
  name = G4_lXe
  specific = 4
FEATURE [App::DocumentObjectGroupPython] O_element107  label="O_element : 061"  # scripted group (container) (typed FeaturePython)
  n = 4
  ref = O_element
FEATURE [App::DocumentObjectGroupPython] Pb_element004  label="Pb_element : 002"  # scripted group (container) (typed FeaturePython)
  n = 1
  ref = Pb_element
FEATURE [App::DocumentObjectGroupPython] W_element005  label="W_element : 005"  # scripted group (container) (typed FeaturePython)
  n = 1
  ref = W_element
FEATURE [App::DocumentObjectGroupPython] G4_PbWO4  # scripted group (container) (typed FeaturePython)
  Dunit = g/cm3
  Dvalue = 8.28
  Group = -> [O_element107,Pb_element004,W_element005]
  conduct = 2
  density = 1
  expand = 3
  formula = G4_PbWO4
  name = G4_PbWO4
  specific = 4
FEATURE [App::DocumentObjectGroupPython] alactic  label="alactic : 1"  # scripted group (container) (typed FeaturePython)
  n = 1
  ref = alactic
FEATURE [App::DocumentObjectGroupPython] G4_Galactic  # scripted group (container) (typed FeaturePython)
  Dunit = g/cm3
  Dvalue = 0
  Group = -> [alactic]
  conduct = 2
  density = 1
  expand = 3
  formula = G4_Galactic
  name = G4_Galactic
  specific = 4
FEATURE [App::DocumentObjectGroupPython] RAPHITE_POROUS  label="RAPHITE_POROUS : 1"  # scripted group (container) (typed FeaturePython)
  n = 1
  ref = RAPHITE_POROUS
FEATURE [App::DocumentObjectGroupPython] G4_GRAPHITE_POROUS  # scripted group (container) (typed FeaturePython)
  Dunit = g/cm3
  Dvalue = 1.7
  Group = -> [RAPHITE_POROUS]
  conduct = 2
  density = 1
  expand = 3
  formula = G4_GRAPHITE_POROUS
  name = G4_GRAPHITE_POROUS
  specific = 4
FEATURE [App::DocumentObjectGroupPython] H_element115  label="H_element : 0.150"  # scripted group (container) (typed FeaturePython)
  n = 0.080538
FEATURE [App::DocumentObjectGroupPython] C_element125  label="C_element : 0.600"  # scripted group (container) (typed FeaturePython)
  n = 0.599848
FEATURE [App::DocumentObjectGroupPython] O_element108  label="O_element : 0.320"  # scripted group (container) (typed FeaturePython)
  n = 0.319614
FEATURE [App::DocumentObjectGroupPython] G4_LUCITE  # scripted group (container) (typed FeaturePython)
  Dunit = g/cm3
  Dvalue = 1.19
  Group = -> [H_element115,C_element125,O_element108]
  conduct = 2
  density = 1
  expand = 3
  formula = G4_LUCITE
  name = G4_LUCITE
  specific = 4
FEATURE [App::DocumentObjectGroupPython] Cu_element002  label="Cu_element : 62"  # scripted group (container) (typed FeaturePython)
  n = 62
  ref = Cu_element
FEATURE [App::DocumentObjectGroupPython] Zn_element002  label="Zn_element : 35"  # scripted group (container) (typed FeaturePython)
  n = 35
  ref = Zn_element
FEATURE [App::DocumentObjectGroupPython] Pb_element005  label="Pb_element : 3"  # scripted group (container) (typed FeaturePython)
  n = 3
  ref = Pb_element
FEATURE [App::DocumentObjectGroupPython] G4_BRASS  # scripted group (container) (typed FeaturePython)
  Dunit = g/cm3
  Dvalue = 8.52
  Group = -> [Cu_element002,Zn_element002,Pb_element005]
  conduct = 2
  density = 1
  expand = 3
  formula = G4_BRASS
  name = G4_BRASS
  specific = 4
FEATURE [App::DocumentObjectGroupPython] Cu_element003  label="Cu_element : 89"  # scripted group (container) (typed FeaturePython)
  n = 89
  ref = Cu_element
FEATURE [App::DocumentObjectGroupPython] Zn_element003  label="Zn_element : 9"  # scripted group (container) (typed FeaturePython)
  n = 9
  ref = Zn_element
FEATURE [App::DocumentObjectGroupPython] Pb_element006  label="Pb_element : 2"  # scripted group (container) (typed FeaturePython)
  n = 2
  ref = Pb_element
FEATURE [App::DocumentObjectGroupPython] G4_BRONZE  # scripted group (container) (typed FeaturePython)
  Dunit = g/cm3
  Dvalue = 8.82
  Group = -> [Cu_element003,Zn_element003,Pb_element006]
  conduct = 2
  density = 1
  expand = 3
  formula = G4_BRONZE
  name = G4_BRONZE
  specific = 4
FEATURE [App::DocumentObjectGroupPython] Fe_element008  label="Fe_element : 74"  # scripted group (container) (typed FeaturePython)
  n = 74
  ref = Fe_element
FEATURE [App::DocumentObjectGroupPython] Cr_element002  label="Cr_element : 18"  # scripted group (container) (typed FeaturePython)
  n = 18
  ref = Cr_element
FEATURE [App::DocumentObjectGroupPython] Ni_element002  label="Ni_element : 8"  # scripted group (container) (typed FeaturePython)
  n = 8
  ref = Ni_element
FEATURE [App::DocumentObjectGroupPython] G4_STAINLESS_STEEL  label="G4_STAINLESS-STEEL"  # scripted group (container) (typed FeaturePython)
  Dunit = g/cm3
  Dvalue = 8
  Group = -> [Fe_element008,Cr_element002,Ni_element002]
  conduct = 2
  density = 1
  expand = 3
  formula = G4_STAINLESS-STEEL
  name = G4_STAINLESS-STEEL
  specific = 4
FEATURE [App::DocumentObjectGroupPython] H_element116  label="H_element : 064"  # scripted group (container) (typed FeaturePython)
  n = 18
  ref = H_element
FEATURE [App::DocumentObjectGroupPython] C_element126  label="C_element : 071"  # scripted group (container) (typed FeaturePython)
  n = 12
  ref = C_element
FEATURE [App::DocumentObjectGroupPython] O_element109  label="O_element : 062"  # scripted group (container) (typed FeaturePython)
  n = 7
  ref = O_element
FEATURE [App::DocumentObjectGroupPython] G4_CR39  # scripted group (container) (typed FeaturePython)
  Dunit = g/cm3
  Dvalue = 1.32
  Group = -> [H_element116,C_element126,O_element109]
  conduct = 2
  density = 1
  expand = 3
  formula = G4_CR39
  name = G4_CR39
  specific = 4
FEATURE [App::DocumentObjectGroupPython] H_element117  label="H_element : 38"  # scripted group (container) (typed FeaturePython)
  n = 38
  ref = H_element
FEATURE [App::DocumentObjectGroupPython] C_element127  label="C_element : 072"  # scripted group (container) (typed FeaturePython)
  n = 18
  ref = C_element
FEATURE [App::DocumentObjectGroupPython] O_element110  label="O_element : 063"  # scripted group (container) (typed FeaturePython)
  n = 1
  ref = O_element
FEATURE [App::DocumentObjectGroupPython] G4_OCTADECANOL  # scripted group (container) (typed FeaturePython)
  Dunit = g/cm3
  Dvalue = 0.812
  Group = -> [H_element117,C_element127,O_element110]
  conduct = 2
  density = 1
  expand = 3
  formula = G4_OCTADECANOL
  name = G4_OCTADECANOL
  specific = 4
FEATURE [App::DocumentObjectGroupPython] HEP  # scripted group (container) (typed FeaturePython)
  Group = -> [G4_lH2,G4_lN2,G4_lO2,G4_lAr,G4_lBr,G4_lKr,G4_lXe,G4_PbWO4,G4_Galactic,G4_GRAPHITE_POROUS,G4_LUCITE,G4_BRASS,G4_BRONZE,G4_STAINLESS_STEEL,G4_CR39,G4_OCTADECANOL]
FEATURE [App::DocumentObjectGroupPython] C_element128  label="C_element : 073"  # scripted group (container) (typed FeaturePython)
  n = 14
  ref = C_element
FEATURE [App::DocumentObjectGroupPython] H_element118  label="H_element : 065"  # scripted group (container) (typed FeaturePython)
  n = 10
  ref = H_element
FEATURE [App::DocumentObjectGroupPython] O_element111  label="O_element : 064"  # scripted group (container) (typed FeaturePython)
  n = 2
  ref = O_element
FEATURE [App::DocumentObjectGroupPython] N_element050  label="N_element : 023"  # scripted group (container) (typed FeaturePython)
  n = 2
  ref = N_element
FEATURE [App::DocumentObjectGroupPython] G4_KEVLAR  # scripted group (container) (typed FeaturePython)
  Dunit = g/cm3
  Dvalue = 1.44
  Group = -> [C_element128,H_element118,O_element111,N_element050]
  conduct = 2
  density = 1
  expand = 3
  formula = G4_KEVLAR
  name = G4_KEVLAR
  specific = 4
FEATURE [App::DocumentObjectGroupPython] C_element129  label="C_element : 074"  # scripted group (container) (typed FeaturePython)
  n = 10
  ref = C_element
FEATURE [App::DocumentObjectGroupPython] H_element119  label="H_element : 066"  # scripted group (container) (typed FeaturePython)
  n = 8
  ref = H_element
FEATURE [App::DocumentObjectGroupPython] O_element112  label="O_element : 065"  # scripted group (container) (typed FeaturePython)
  n = 4
  ref = O_element
FEATURE [App::DocumentObjectGroupPython] G4_DACRON  # scripted group (container) (typed FeaturePython)
  Dunit = g/cm3
  Dvalue = 1.4
  Group = -> [C_element129,H_element119,O_element112]
  conduct = 2
  density = 1
  expand = 3
  formula = G4_DACRON
  name = G4_DACRON
  specific = 4
FEATURE [App::DocumentObjectGroupPython] C_element130  label="C_element : 075"  # scripted group (container) (typed FeaturePython)
  n = 4
  ref = C_element
FEATURE [App::DocumentObjectGroupPython] H_element120  label="H_element : 067"  # scripted group (container) (typed FeaturePython)
  n = 5
  ref = H_element
FEATURE [App::DocumentObjectGroupPython] Cl_element030  label="Cl_element : 016"  # scripted group (container) (typed FeaturePython)
  n = 1
  ref = Cl_element
FEATURE [App::DocumentObjectGroupPython] G4_NEOPRENE  # scripted group (container) (typed FeaturePython)
  Dunit = g/cm3
  Dvalue = 1.23
  Group = -> [C_element130,H_element120,Cl_element030]
  conduct = 2
  density = 1
  expand = 3
  formula = G4_NEOPRENE
  name = G4_NEOPRENE
  specific = 4
FEATURE [App::DocumentObjectGroupPython] Space  # scripted group (container) (typed FeaturePython)
  Group = -> [G4_KEVLAR,G4_DACRON,G4_NEOPRENE]
FEATURE [App::DocumentObjectGroupPython] H_element121  label="H_element : 068"  # scripted group (container) (typed FeaturePython)
  n = 5
  ref = H_element
FEATURE [App::DocumentObjectGroupPython] C_element131  label="C_element : 076"  # scripted group (container) (typed FeaturePython)
  n = 4
  ref = C_element
FEATURE [App::DocumentObjectGroupPython] N_element051  label="N_element : 3"  # scripted group (container) (typed FeaturePython)
  n = 3
  ref = N_element
FEATURE [App::DocumentObjectGroupPython] O_element113  label="O_element : 066"  # scripted group (container) (typed FeaturePython)
  n = 1
  ref = O_element
FEATURE [App::DocumentObjectGroupPython] G4_CYTOSINE  # scripted group (container) (typed FeaturePython)
  Dunit = g/cm3
  Dvalue = 1.55
  Group = -> [H_element121,C_element131,N_element051,O_element113]
  conduct = 2
  density = 1
  expand = 3
  formula = G4_CYTOSINE
  name = G4_CYTOSINE
  specific = 4
FEATURE [App::DocumentObjectGroupPython] H_element122  label="H_element : 069"  # scripted group (container) (typed FeaturePython)
  n = 6
  ref = H_element
FEATURE [App::DocumentObjectGroupPython] C_element132  label="C_element : 077"  # scripted group (container) (typed FeaturePython)
  n = 5
  ref = C_element
FEATURE [App::DocumentObjectGroupPython] N_element052  label="N_element : 024"  # scripted group (container) (typed FeaturePython)
  n = 2
  ref = N_element
FEATURE [App::DocumentObjectGroupPython] O_element114  label="O_element : 067"  # scripted group (container) (typed FeaturePython)
  n = 2
  ref = O_element
FEATURE [App::DocumentObjectGroupPython] G4_THYMINE  # scripted group (container) (typed FeaturePython)
  Dunit = g/cm3
  Dvalue = 1.23
  Group = -> [H_element122,C_element132,N_element052,O_element114]
  conduct = 2
  density = 1
  expand = 3
  formula = G4_THYMINE
  name = G4_THYMINE
  specific = 4
FEATURE [App::DocumentObjectGroupPython] H_element123  label="H_element : 070"  # scripted group (container) (typed FeaturePython)
  n = 4
  ref = H_element
FEATURE [App::DocumentObjectGroupPython] C_element133  label="C_element : 078"  # scripted group (container) (typed FeaturePython)
  n = 4
  ref = C_element
FEATURE [App::DocumentObjectGroupPython] N_element053  label="N_element : 025"  # scripted group (container) (typed FeaturePython)
  n = 2
  ref = N_element
FEATURE [App::DocumentObjectGroupPython] O_element115  label="O_element : 068"  # scripted group (container) (typed FeaturePython)
  n = 2
  ref = O_element
FEATURE [App::DocumentObjectGroupPython] G4_URACIL  # scripted group (container) (typed FeaturePython)
  Dunit = g/cm3
  Dvalue = 1.32
  Group = -> [H_element123,C_element133,N_element053,O_element115]
  conduct = 2
  density = 1
  expand = 3
  formula = G4_URACIL
  name = G4_URACIL
  specific = 4
FEATURE [App::DocumentObjectGroupPython] H_element124  label="H_element : 071"  # scripted group (container) (typed FeaturePython)
  n = 4
  ref = H_element
FEATURE [App::DocumentObjectGroupPython] C_element134  label="C_element : 079"  # scripted group (container) (typed FeaturePython)
  n = 5
  ref = C_element
FEATURE [App::DocumentObjectGroupPython] N_element054  label="N_element : 026"  # scripted group (container) (typed FeaturePython)
  n = 5
  ref = N_element
FEATURE [App::DocumentObjectGroupPython] G4_DNA_ADENINE  # scripted group (container) (typed FeaturePython)
  Dunit = g/cm3
  Dvalue = 1
  Group = -> [H_element124,C_element134,N_element054]
  conduct = 2
  density = 1
  expand = 3
  formula = G4_DNA_ADENINE
  name = G4_DNA_ADENINE
  specific = 4
FEATURE [App::DocumentObjectGroupPython] H_element125  label="H_element : 072"  # scripted group (container) (typed FeaturePython)
  n = 4
  ref = H_element
FEATURE [App::DocumentObjectGroupPython] C_element135  label="C_element : 080"  # scripted group (container) (typed FeaturePython)
  n = 5
  ref = C_element
FEATURE [App::DocumentObjectGroupPython] N_element055  label="N_element : 027"  # scripted group (container) (typed FeaturePython)
  n = 5
  ref = N_element
FEATURE [App::DocumentObjectGroupPython] O_element116  label="O_element : 069"  # scripted group (container) (typed FeaturePython)
  n = 1
  ref = O_element
FEATURE [App::DocumentObjectGroupPython] G4_DNA_GUANINE  # scripted group (container) (typed FeaturePython)
  Dunit = g/cm3
  Dvalue = 1
  Group = -> [H_element125,C_element135,N_element055,O_element116]
  conduct = 2
  density = 1
  expand = 3
  formula = G4_DNA_GUANINE
  name = G4_DNA_GUANINE
  specific = 4
FEATURE [App::DocumentObjectGroupPython] H_element126  label="H_element : 073"  # scripted group (container) (typed FeaturePython)
  n = 4
  ref = H_element
FEATURE [App::DocumentObjectGroupPython] C_element136  label="C_element : 081"  # scripted group (container) (typed FeaturePython)
  n = 4
  ref = C_element
FEATURE [App::DocumentObjectGroupPython] N_element056  label="N_element : 028"  # scripted group (container) (typed FeaturePython)
  n = 3
  ref = N_element
FEATURE [App::DocumentObjectGroupPython] O_element117  label="O_element : 070"  # scripted group (container) (typed FeaturePython)
  n = 1
  ref = O_element
FEATURE [App::DocumentObjectGroupPython] G4_DNA_CYTOSINE  # scripted group (container) (typed FeaturePython)
  Dunit = g/cm3
  Dvalue = 1
  Group = -> [H_element126,C_element136,N_element056,O_element117]
  conduct = 2
  density = 1
  expand = 3
  formula = G4_DNA_CYTOSINE
  name = G4_DNA_CYTOSINE
  specific = 4
FEATURE [App::DocumentObjectGroupPython] H_element127  label="H_element : 074"  # scripted group (container) (typed FeaturePython)
  n = 5
  ref = H_element
FEATURE [App::DocumentObjectGroupPython] C_element137  label="C_element : 082"  # scripted group (container) (typed FeaturePython)
  n = 5
  ref = C_element
FEATURE [App::DocumentObjectGroupPython] N_element057  label="N_element : 029"  # scripted group (container) (typed FeaturePython)
  n = 2
  ref = N_element
FEATURE [App::DocumentObjectGroupPython] O_element118  label="O_element : 071"  # scripted group (container) (typed FeaturePython)
  n = 2
  ref = O_element
FEATURE [App::DocumentObjectGroupPython] G4_DNA_THYMINE  # scripted group (container) (typed FeaturePython)
  Dunit = g/cm3
  Dvalue = 1
  Group = -> [H_element127,C_element137,N_element057,O_element118]
  conduct = 2
  density = 1
  expand = 3
  formula = G4_DNA_THYMINE
  name = G4_DNA_THYMINE
  specific = 4
FEATURE [App::DocumentObjectGroupPython] H_element128  label="H_element : 075"  # scripted group (container) (typed FeaturePython)
  n = 3
  ref = H_element
FEATURE [App::DocumentObjectGroupPython] C_element138  label="C_element : 083"  # scripted group (container) (typed FeaturePython)
  n = 4
  ref = C_element
FEATURE [App::DocumentObjectGroupPython] N_element058  label="N_element : 030"  # scripted group (container) (typed FeaturePython)
  n = 2
  ref = N_element
FEATURE [App::DocumentObjectGroupPython] O_element119  label="O_element : 072"  # scripted group (container) (typed FeaturePython)
  n = 2
  ref = O_element
FEATURE [App::DocumentObjectGroupPython] G4_DNA_URACIL  # scripted group (container) (typed FeaturePython)
  Dunit = g/cm3
  Dvalue = 1
  Group = -> [H_element128,C_element138,N_element058,O_element119]
  conduct = 2
  density = 1
  expand = 3
  formula = G4_DNA_URACIL
  name = G4_DNA_URACIL
  specific = 4
FEATURE [App::DocumentObjectGroupPython] H_element129  label="H_element : 076"  # scripted group (container) (typed FeaturePython)
  n = 10
  ref = H_element
FEATURE [App::DocumentObjectGroupPython] C_element139  label="C_element : 084"  # scripted group (container) (typed FeaturePython)
  n = 10
  ref = C_element
FEATURE [App::DocumentObjectGroupPython] N_element059  label="N_element : 031"  # scripted group (container) (typed FeaturePython)
  n = 5
  ref = N_element
FEATURE [App::DocumentObjectGroupPython] O_element120  label="O_element : 073"  # scripted group (container) (typed FeaturePython)
  n = 4
  ref = O_element
FEATURE [App::DocumentObjectGroupPython] G4_DNA_ADENOSINE  # scripted group (container) (typed FeaturePython)
  Dunit = g/cm3
  Dvalue = 1
  Group = -> [H_element129,C_element139,N_element059,O_element120]
  conduct = 2
  density = 1
  expand = 3
  formula = G4_DNA_ADENOSINE
  name = G4_DNA_ADENOSINE
  specific = 4
FEATURE [App::DocumentObjectGroupPython] H_element130  label="H_element : 077"  # scripted group (container) (typed FeaturePython)
  n = 10
  ref = H_element
FEATURE [App::DocumentObjectGroupPython] C_element140  label="C_element : 085"  # scripted group (container) (typed FeaturePython)
  n = 10
  ref = C_element
FEATURE [App::DocumentObjectGroupPython] N_element060  label="N_element : 032"  # scripted group (container) (typed FeaturePython)
  n = 5
  ref = N_element
FEATURE [App::DocumentObjectGroupPython] O_element121  label="O_element : 074"  # scripted group (container) (typed FeaturePython)
  n = 5
  ref = O_element
FEATURE [App::DocumentObjectGroupPython] G4_DNA_GUANOSINE  # scripted group (container) (typed FeaturePython)
  Dunit = g/cm3
  Dvalue = 1
  Group = -> [H_element130,C_element140,N_element060,O_element121]
  conduct = 2
  density = 1
  expand = 3
  formula = G4_DNA_GUANOSINE
  name = G4_DNA_GUANOSINE
  specific = 4
FEATURE [App::DocumentObjectGroupPython] H_element131  label="H_element : 078"  # scripted group (container) (typed FeaturePython)
  n = 10
  ref = H_element
FEATURE [App::DocumentObjectGroupPython] C_element141  label="C_element : 086"  # scripted group (container) (typed FeaturePython)
  n = 9
  ref = C_element
FEATURE [App::DocumentObjectGroupPython] N_element061  label="N_element : 033"  # scripted group (container) (typed FeaturePython)
  n = 3
  ref = N_element
FEATURE [App::DocumentObjectGroupPython] O_element122  label="O_element : 075"  # scripted group (container) (typed FeaturePython)
  n = 5
  ref = O_element
FEATURE [App::DocumentObjectGroupPython] G4_DNA_CYTIDINE  # scripted group (container) (typed FeaturePython)
  Dunit = g/cm3
  Dvalue = 1
  Group = -> [H_element131,C_element141,N_element061,O_element122]
  conduct = 2
  density = 1
  expand = 3
  formula = G4_DNA_CYTIDINE
  name = G4_DNA_CYTIDINE
  specific = 4
FEATURE [App::DocumentObjectGroupPython] H_element132  label="H_element : 079"  # scripted group (container) (typed FeaturePython)
  n = 9
  ref = H_element
FEATURE [App::DocumentObjectGroupPython] C_element142  label="C_element : 087"  # scripted group (container) (typed FeaturePython)
  n = 9
  ref = C_element
FEATURE [App::DocumentObjectGroupPython] N_element062  label="N_element : 034"  # scripted group (container) (typed FeaturePython)
  n = 2
  ref = N_element
FEATURE [App::DocumentObjectGroupPython] O_element123  label="O_element : 076"  # scripted group (container) (typed FeaturePython)
  n = 6
  ref = O_element
FEATURE [App::DocumentObjectGroupPython] G4_DNA_URIDINE  # scripted group (container) (typed FeaturePython)
  Dunit = g/cm3
  Dvalue = 1
  Group = -> [H_element132,C_element142,N_element062,O_element123]
  conduct = 2
  density = 1
  expand = 3
  formula = G4_DNA_URIDINE
  name = G4_DNA_URIDINE
  specific = 4
FEATURE [App::DocumentObjectGroupPython] H_element133  label="H_element : 080"  # scripted group (container) (typed FeaturePython)
  n = 11
  ref = H_element
FEATURE [App::DocumentObjectGroupPython] C_element143  label="C_element : 088"  # scripted group (container) (typed FeaturePython)
  n = 10
  ref = C_element
FEATURE [App::DocumentObjectGroupPython] N_element063  label="N_element : 035"  # scripted group (container) (typed FeaturePython)
  n = 2
  ref = N_element
FEATURE [App::DocumentObjectGroupPython] O_element124  label="O_element : 077"  # scripted group (container) (typed FeaturePython)
  n = 6
  ref = O_element
FEATURE [App::DocumentObjectGroupPython] G4_DNA_METHYLURIDINE  # scripted group (container) (typed FeaturePython)
  Dunit = g/cm3
  Dvalue = 1
  Group = -> [H_element133,C_element143,N_element063,O_element124]
  conduct = 2
  density = 1
  expand = 3
  formula = G4_DNA_METHYLURIDINE
  name = G4_DNA_METHYLURIDINE
  specific = 4
FEATURE [App::DocumentObjectGroupPython] P_element014  label="P_element : 003"  # scripted group (container) (typed FeaturePython)
  n = 1
  ref = P_element
FEATURE [App::DocumentObjectGroupPython] O_element125  label="O_element : 078"  # scripted group (container) (typed FeaturePython)
  n = 3
  ref = O_element
FEATURE [App::DocumentObjectGroupPython] G4_DNA_MONOPHOSPHATE  # scripted group (container) (typed FeaturePython)
  Dunit = g/cm3
  Dvalue = 1
  Group = -> [P_element014,O_element125]
  conduct = 2
  density = 1
  expand = 3
  formula = G4_DNA_MONOPHOSPHATE
  name = G4_DNA_MONOPHOSPHATE
  specific = 4
FEATURE [App::DocumentObjectGroupPython] H_element134  label="H_element : 081"  # scripted group (container) (typed FeaturePython)
  n = 10
  ref = H_element
FEATURE [App::DocumentObjectGroupPython] C_element144  label="C_element : 089"  # scripted group (container) (typed FeaturePython)
  n = 10
  ref = C_element
FEATURE [App::DocumentObjectGroupPython] N_element064  label="N_element : 036"  # scripted group (container) (typed FeaturePython)
  n = 5
  ref = N_element
FEATURE [App::DocumentObjectGroupPython] O_element126  label="O_element : 079"  # scripted group (container) (typed FeaturePython)
  n = 7
  ref = O_element
FEATURE [App::DocumentObjectGroupPython] P_element015  label="P_element : 004"  # scripted group (container) (typed FeaturePython)
  n = 1
  ref = P_element
FEATURE [App::DocumentObjectGroupPython] G4_DNA_A  # scripted group (container) (typed FeaturePython)
  Dunit = g/cm3
  Dvalue = 1
  Group = -> [H_element134,C_element144,N_element064,O_element126,P_element015]
  conduct = 2
  density = 1
  expand = 3
  formula = G4_DNA_A
  name = G4_DNA_A
  specific = 4
FEATURE [App::DocumentObjectGroupPython] H_element135  label="H_element : 082"  # scripted group (container) (typed FeaturePython)
  n = 10
  ref = H_element
FEATURE [App::DocumentObjectGroupPython] C_element145  label="C_element : 090"  # scripted group (container) (typed FeaturePython)
  n = 10
  ref = C_element
FEATURE [App::DocumentObjectGroupPython] N_element065  label="N_element : 037"  # scripted group (container) (typed FeaturePython)
  n = 5
  ref = N_element
FEATURE [App::DocumentObjectGroupPython] O_element127  label="O_element : 8"  # scripted group (container) (typed FeaturePython)
  n = 8
  ref = O_element
FEATURE [App::DocumentObjectGroupPython] P_element016  label="P_element : 005"  # scripted group (container) (typed FeaturePython)
  n = 1
  ref = P_element
FEATURE [App::DocumentObjectGroupPython] G4_DNA_G  # scripted group (container) (typed FeaturePython)
  Dunit = g/cm3
  Dvalue = 1
  Group = -> [H_element135,C_element145,N_element065,O_element127,P_element016]
  conduct = 2
  density = 1
  expand = 3
  formula = G4_DNA_G
  name = G4_DNA_G
  specific = 4
FEATURE [App::DocumentObjectGroupPython] H_element136  label="H_element : 083"  # scripted group (container) (typed FeaturePython)
  n = 10
  ref = H_element
FEATURE [App::DocumentObjectGroupPython] C_element146  label="C_element : 091"  # scripted group (container) (typed FeaturePython)
  n = 9
  ref = C_element
FEATURE [App::DocumentObjectGroupPython] N_element066  label="N_element : 038"  # scripted group (container) (typed FeaturePython)
  n = 3
  ref = N_element
FEATURE [App::DocumentObjectGroupPython] O_element128  label="O_element : 080"  # scripted group (container) (typed FeaturePython)
  n = 8
  ref = O_element
FEATURE [App::DocumentObjectGroupPython] P_element017  label="P_element : 006"  # scripted group (container) (typed FeaturePython)
  n = 1
  ref = P_element
FEATURE [App::DocumentObjectGroupPython] G4_DNA_C  # scripted group (container) (typed FeaturePython)
  Dunit = g/cm3
  Dvalue = 1
  Group = -> [H_element136,C_element146,N_element066,O_element128,P_element017]
  conduct = 2
  density = 1
  expand = 3
  formula = G4_DNA_C
  name = G4_DNA_C
  specific = 4
FEATURE [App::DocumentObjectGroupPython] H_element137  label="H_element : 084"  # scripted group (container) (typed FeaturePython)
  n = 9
  ref = H_element
FEATURE [App::DocumentObjectGroupPython] C_element147  label="C_element : 092"  # scripted group (container) (typed FeaturePython)
  n = 9
  ref = C_element
FEATURE [App::DocumentObjectGroupPython] N_element067  label="N_element : 039"  # scripted group (container) (typed FeaturePython)
  n = 2
  ref = N_element
FEATURE [App::DocumentObjectGroupPython] O_element129  label="O_element : 9"  # scripted group (container) (typed FeaturePython)
  n = 9
  ref = O_element
FEATURE [App::DocumentObjectGroupPython] P_element018  label="P_element : 007"  # scripted group (container) (typed FeaturePython)
  n = 1
  ref = P_element
FEATURE [App::DocumentObjectGroupPython] G4_DNA_U  # scripted group (container) (typed FeaturePython)
  Dunit = g/cm3
  Dvalue = 1
  Group = -> [H_element137,C_element147,N_element067,O_element129,P_element018]
  conduct = 2
  density = 1
  expand = 3
  formula = G4_DNA_U
  name = G4_DNA_U
  specific = 4
FEATURE [App::DocumentObjectGroupPython] H_element138  label="H_element : 085"  # scripted group (container) (typed FeaturePython)
  n = 11
  ref = H_element
FEATURE [App::DocumentObjectGroupPython] C_element148  label="C_element : 093"  # scripted group (container) (typed FeaturePython)
  n = 10
  ref = C_element
FEATURE [App::DocumentObjectGroupPython] N_element068  label="N_element : 040"  # scripted group (container) (typed FeaturePython)
  n = 2
  ref = N_element
FEATURE [App::DocumentObjectGroupPython] O_element130  label="O_element : 081"  # scripted group (container) (typed FeaturePython)
  n = 9
  ref = O_element
FEATURE [App::DocumentObjectGroupPython] P_element019  label="P_element : 008"  # scripted group (container) (typed FeaturePython)
  n = 1
  ref = P_element
FEATURE [App::DocumentObjectGroupPython] G4_DNA_MU  # scripted group (container) (typed FeaturePython)
  Dunit = g/cm3
  Dvalue = 1
  Group = -> [H_element138,C_element148,N_element068,O_element130,P_element019]
  conduct = 2
  density = 1
  expand = 3
  formula = G4_DNA_MU
  name = G4_DNA_MU
  specific = 4
FEATURE [App::DocumentObjectGroupPython] BioChemical  # scripted group (container) (typed FeaturePython)
  Group = -> [G4_CYTOSINE,G4_THYMINE,G4_URACIL,G4_DNA_ADENINE,G4_DNA_GUANINE,G4_DNA_CYTOSINE,G4_DNA_THYMINE,G4_DNA_URACIL,G4_DNA_ADENOSINE,G4_DNA_GUANOSINE,G4_DNA_CYTIDINE,G4_DNA_URIDINE,G4_DNA_METHYLURIDINE,G4_DNA_MONOPHOSPHATE,G4_DNA_A,G4_DNA_G,G4_DNA_C,G4_DNA_U,G4_DNA_MU]
FEATURE [App::DocumentObjectGroupPython] G4Materials  # scripted group (container) (typed FeaturePython)
  Group = -> [NIST,Element,HEP,Space,BioChemical]
  version = 1
FEATURE [App::DocumentObjectGroupPython] Geant4  # scripted group (container) (typed FeaturePython)
  Group = -> [G4Isotopes,G4Elements,G4Materials]
FEATURE [App::DocumentObjectGroupPython] Materials  # scripted group (container) (typed FeaturePython)
  Group = -> [Geant4]
FEATURE [Part::FeaturePython] GDMLBox_WorldBox  # WARN: FeaturePython — macro-defined, semantics opaque (R4)
  lunit = 2
  material = 5
  x = 100
  y = 100
  z = 100
FEATURE [Part::FeaturePython] GDMLBox_Box  # WARN: FeaturePython — macro-defined, semantics opaque (R4)
  lunit = 2
  material = 0
  x = 10
  y = 10
  z = 10
FEATURE [App::Part] LV_Box
  Group = -> [GDMLBox_Box]
  Origin = -> Origin001
FEATURE [App::Part] worldVOL
  Group = -> [GDMLBox_WorldBox,LV_Box]
  Origin = -> Origin
FEATURE [Part::FeaturePython] Array  # Draft array (typed FeaturePython)
  AlwaysSyncPlacement = false
  Angle = 360
  ArrayType = 0
  Axis = (0,0,1)
  Base = -> LV_Box
  Center = (0,0,0)
  Count = 4
  ExpandArray = false
  Fuse = false
  IntervalAxis = (0,0,0)
  IntervalX = (100,0,0)
  IntervalY = (0,100,0)
  IntervalZ = (0,0,100)
  NumberCircles = 3
  NumberPolar = 5
  NumberX = 2
  NumberY = 2
  NumberZ = 1
  PlacementList = 4 placements: [(0,0,0),(0,100,0),(100,0,0),(100,100,0)]
  RadialDistance = 50
  ScaleList = (4) [(1,1,1),(1,1,1),(1,1,1),(1,1,1)]
  Symmetry = 1
  TangentialDistance = 25
